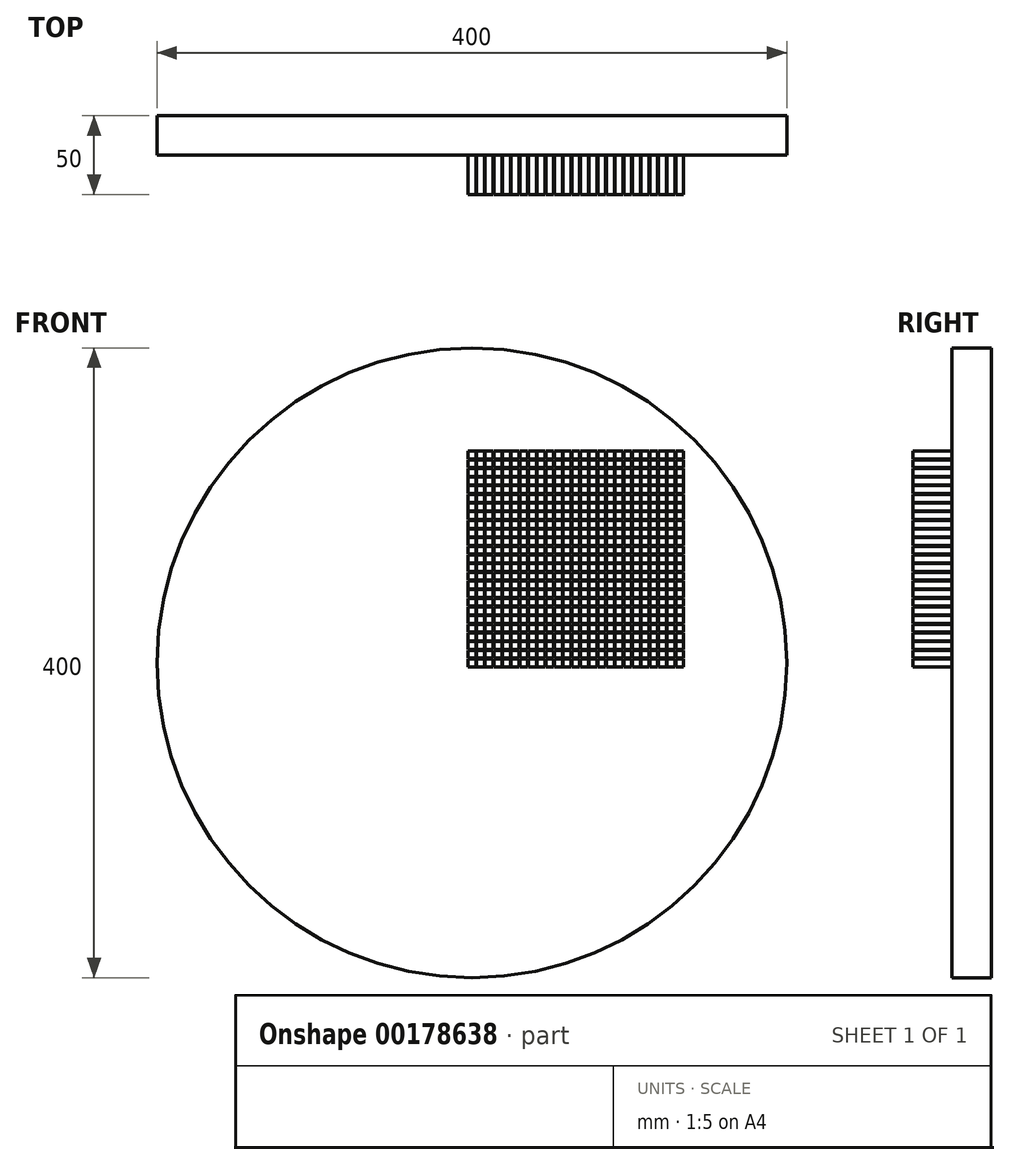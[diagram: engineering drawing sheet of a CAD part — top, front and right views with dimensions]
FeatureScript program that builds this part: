
annotation { "Feature Type Name" : "Feature", "Feature Type Description" : "" }
export const myFeature = defineFeature(function(context is Context, id is Id, definition is map)
    precondition{}
    {
        {
            var Q0;
            Q0=qCreatedBy(makeId("Front.planeOp"),FACE);
            var sketch = newSketch(context, id + "F0", { "sketchPlane" : qUnion([Q0])});
            skCircle(sketch, "E0", {"center": v(0, 0) * mm, "radius": 200 * mm});
            skLineSegment(sketch, "E1.bottom", {"start": v(141.42, 141.42) * mm, "end": v(-141.42, 141.42) * mm});
            skLineSegment(sketch, "E1.top", {"start": v(141.42, -141.42) * mm, "end": v(-141.42, -141.42) * mm});
            skLineSegment(sketch, "E1.left", {"start": v(141.42, 141.42) * mm, "end": v(141.42, -141.42) * mm});
            skLineSegment(sketch, "E1.right", {"start": v(-141.42, 141.42) * mm, "end": v(-141.42, -141.42) * mm});
            skSolve(sketch);
        }
        {
            var Q0;
            {var subQ0=sQuery(id+"F0.wireOp",EDGE,"E1.bottom");Q0=makeQuery(id+"F0.imprint","IMPRINT",FACE,{"disambiguationData":[TD([[makeQuery(id+"F0.imprint","IMPRINT",EDGE,{"derivedFrom":subQ0}),-1.0]])]});}
            var Q1;
            {var subQ0=sQuery(id+"F0.wireOp",EDGE,"E1.right");Q1=makeQuery(id+"F0.imprint","IMPRINT",FACE,{"disambiguationData":[TD([[makeQuery(id+"F0.imprint","IMPRINT",EDGE,{"derivedFrom":subQ0}),-1.0]])]});}
            var Q2;
            {var subQ0=sQuery(id+"F0.wireOp",EDGE,"E1.left");Q2=makeQuery(id+"F0.imprint","IMPRINT",FACE,{"disambiguationData":[TD([[makeQuery(id+"F0.imprint","IMPRINT",EDGE,{"derivedFrom":subQ0}),1.0]])]});}
            var Q3;
            {var subQ0=sQuery(id+"F0.wireOp",EDGE,"E1.top");Q3=makeQuery(id+"F0.imprint","IMPRINT",FACE,{"disambiguationData":[TD([[makeQuery(id+"F0.imprint","IMPRINT",EDGE,{"derivedFrom":subQ0}),1.0]])]});}
            var Q4;
            Q4=makeQuery(id+"F0.imprint","IMPRINT",FACE,{"disambiguationData":[TD([[makeQuery(id+"F0.imprint","IMPRINT",EDGE,{"derivedFrom":sQuery(id+"F0.wireOp",EDGE,"E1.bottom")}),1.0]])]});
            extrude(context, id + "F1", {"entities" : qUnion([Q0, Q1, Q2, Q3, Q4]), "depth" : 25 * mm});
        }
        {
            var Q0;
            Q0=makeQuery(id+"F1.opExtrude","CAP_FACE",FACE,{"disambiguationData":[OSD([sQuery(id+"F0.wireOp",EDGE,"E0")])],"isStart":false});
            var sketch = newSketch(context, id + "F2", { "sketchPlane" : qUnion([Q0])});
            skLineSegment(sketch, "E2.bottom", {"start": v(2.5, 2.5) * mm, "end": v(-2.5, 2.5) * mm});
            skLineSegment(sketch, "E2.top", {"start": v(2.5, -2.5) * mm, "end": v(-2.5, -2.5) * mm});
            skLineSegment(sketch, "E2.left", {"start": v(2.5, 2.5) * mm, "end": v(2.5, -2.5) * mm});
            skLineSegment(sketch, "E2.right", {"start": v(-2.5, 2.5) * mm, "end": v(-2.5, -2.5) * mm});
            skPoint(sketch, "E2.middle", {"position": v(0, 0) * mm});
            skLineSegment(sketch, "E3.0.1.0", {"start": v(2.5, 8) * mm, "end": v(-2.5, 8) * mm});
            skLineSegment(sketch, "E3.0.1.1", {"start": v(2.5, 8) * mm, "end": v(2.5, 3) * mm});
            skLineSegment(sketch, "E3.0.1.2", {"start": v(2.5, 3) * mm, "end": v(-2.5, 3) * mm});
            skLineSegment(sketch, "E3.0.1.3", {"start": v(-2.5, 8) * mm, "end": v(-2.5, 3) * mm});
            skPoint(sketch, "E3.0.1.4", {"position": v(0, 5.5) * mm});
            skLineSegment(sketch, "E3.0.2.0", {"start": v(2.5, 13.5) * mm, "end": v(-2.5, 13.5) * mm});
            skLineSegment(sketch, "E3.0.2.1", {"start": v(2.5, 13.5) * mm, "end": v(2.5, 8.5) * mm});
            skLineSegment(sketch, "E3.0.2.2", {"start": v(2.5, 8.5) * mm, "end": v(-2.5, 8.5) * mm});
            skLineSegment(sketch, "E3.0.2.3", {"start": v(-2.5, 13.5) * mm, "end": v(-2.5, 8.5) * mm});
            skPoint(sketch, "E3.0.2.4", {"position": v(0, 11) * mm});
            skLineSegment(sketch, "E3.0.3.0", {"start": v(2.5, 19) * mm, "end": v(-2.5, 19) * mm});
            skLineSegment(sketch, "E3.0.3.1", {"start": v(2.5, 19) * mm, "end": v(2.5, 14) * mm});
            skLineSegment(sketch, "E3.0.3.2", {"start": v(2.5, 14) * mm, "end": v(-2.5, 14) * mm});
            skLineSegment(sketch, "E3.0.3.3", {"start": v(-2.5, 19) * mm, "end": v(-2.5, 14) * mm});
            skPoint(sketch, "E3.0.3.4", {"position": v(0, 16.5) * mm});
            skLineSegment(sketch, "E3.0.4.0", {"start": v(2.5, 24.5) * mm, "end": v(-2.5, 24.5) * mm});
            skLineSegment(sketch, "E3.0.4.1", {"start": v(2.5, 24.5) * mm, "end": v(2.5, 19.5) * mm});
            skLineSegment(sketch, "E3.0.4.2", {"start": v(2.5, 19.5) * mm, "end": v(-2.5, 19.5) * mm});
            skLineSegment(sketch, "E3.0.4.3", {"start": v(-2.5, 24.5) * mm, "end": v(-2.5, 19.5) * mm});
            skPoint(sketch, "E3.0.4.4", {"position": v(0, 22) * mm});
            skLineSegment(sketch, "E3.0.5.0", {"start": v(2.5, 30) * mm, "end": v(-2.5, 30) * mm});
            skLineSegment(sketch, "E3.0.5.1", {"start": v(2.5, 30) * mm, "end": v(2.5, 25) * mm});
            skLineSegment(sketch, "E3.0.5.2", {"start": v(2.5, 25) * mm, "end": v(-2.5, 25) * mm});
            skLineSegment(sketch, "E3.0.5.3", {"start": v(-2.5, 30) * mm, "end": v(-2.5, 25) * mm});
            skPoint(sketch, "E3.0.5.4", {"position": v(0, 27.5) * mm});
            skLineSegment(sketch, "E3.0.6.0", {"start": v(2.5, 35.5) * mm, "end": v(-2.5, 35.5) * mm});
            skLineSegment(sketch, "E3.0.6.1", {"start": v(2.5, 35.5) * mm, "end": v(2.5, 30.5) * mm});
            skLineSegment(sketch, "E3.0.6.2", {"start": v(2.5, 30.5) * mm, "end": v(-2.5, 30.5) * mm});
            skLineSegment(sketch, "E3.0.6.3", {"start": v(-2.5, 35.5) * mm, "end": v(-2.5, 30.5) * mm});
            skPoint(sketch, "E3.0.6.4", {"position": v(0, 33) * mm});
            skLineSegment(sketch, "E3.0.7.0", {"start": v(2.5, 41) * mm, "end": v(-2.5, 41) * mm});
            skLineSegment(sketch, "E3.0.7.1", {"start": v(2.5, 41) * mm, "end": v(2.5, 36) * mm});
            skLineSegment(sketch, "E3.0.7.2", {"start": v(2.5, 36) * mm, "end": v(-2.5, 36) * mm});
            skLineSegment(sketch, "E3.0.7.3", {"start": v(-2.5, 41) * mm, "end": v(-2.5, 36) * mm});
            skPoint(sketch, "E3.0.7.4", {"position": v(0, 38.5) * mm});
            skLineSegment(sketch, "E3.0.8.0", {"start": v(2.5, 46.5) * mm, "end": v(-2.5, 46.5) * mm});
            skLineSegment(sketch, "E3.0.8.1", {"start": v(2.5, 46.5) * mm, "end": v(2.5, 41.5) * mm});
            skLineSegment(sketch, "E3.0.8.2", {"start": v(2.5, 41.5) * mm, "end": v(-2.5, 41.5) * mm});
            skLineSegment(sketch, "E3.0.8.3", {"start": v(-2.5, 46.5) * mm, "end": v(-2.5, 41.5) * mm});
            skPoint(sketch, "E3.0.8.4", {"position": v(0, 44) * mm});
            skLineSegment(sketch, "E3.0.9.0", {"start": v(2.5, 52) * mm, "end": v(-2.5, 52) * mm});
            skLineSegment(sketch, "E3.0.9.1", {"start": v(2.5, 52) * mm, "end": v(2.5, 47) * mm});
            skLineSegment(sketch, "E3.0.9.2", {"start": v(2.5, 47) * mm, "end": v(-2.5, 47) * mm});
            skLineSegment(sketch, "E3.0.9.3", {"start": v(-2.5, 52) * mm, "end": v(-2.5, 47) * mm});
            skPoint(sketch, "E3.0.9.4", {"position": v(0, 49.5) * mm});
            skLineSegment(sketch, "E3.0.10.0", {"start": v(2.5, 57.5) * mm, "end": v(-2.5, 57.5) * mm});
            skLineSegment(sketch, "E3.0.10.1", {"start": v(2.5, 57.5) * mm, "end": v(2.5, 52.5) * mm});
            skLineSegment(sketch, "E3.0.10.2", {"start": v(2.5, 52.5) * mm, "end": v(-2.5, 52.5) * mm});
            skLineSegment(sketch, "E3.0.10.3", {"start": v(-2.5, 57.5) * mm, "end": v(-2.5, 52.5) * mm});
            skPoint(sketch, "E3.0.10.4", {"position": v(0, 55) * mm});
            skLineSegment(sketch, "E3.0.11.0", {"start": v(2.5, 63) * mm, "end": v(-2.5, 63) * mm});
            skLineSegment(sketch, "E3.0.11.1", {"start": v(2.5, 63) * mm, "end": v(2.5, 58) * mm});
            skLineSegment(sketch, "E3.0.11.2", {"start": v(2.5, 58) * mm, "end": v(-2.5, 58) * mm});
            skLineSegment(sketch, "E3.0.11.3", {"start": v(-2.5, 63) * mm, "end": v(-2.5, 58) * mm});
            skPoint(sketch, "E3.0.11.4", {"position": v(0, 60.5) * mm});
            skLineSegment(sketch, "E3.0.12.0", {"start": v(2.5, 68.5) * mm, "end": v(-2.5, 68.5) * mm});
            skLineSegment(sketch, "E3.0.12.1", {"start": v(2.5, 68.5) * mm, "end": v(2.5, 63.5) * mm});
            skLineSegment(sketch, "E3.0.12.2", {"start": v(2.5, 63.5) * mm, "end": v(-2.5, 63.5) * mm});
            skLineSegment(sketch, "E3.0.12.3", {"start": v(-2.5, 68.5) * mm, "end": v(-2.5, 63.5) * mm});
            skPoint(sketch, "E3.0.12.4", {"position": v(0, 66) * mm});
            skLineSegment(sketch, "E3.0.13.0", {"start": v(2.5, 74) * mm, "end": v(-2.5, 74) * mm});
            skLineSegment(sketch, "E3.0.13.1", {"start": v(2.5, 74) * mm, "end": v(2.5, 69) * mm});
            skLineSegment(sketch, "E3.0.13.2", {"start": v(2.5, 69) * mm, "end": v(-2.5, 69) * mm});
            skLineSegment(sketch, "E3.0.13.3", {"start": v(-2.5, 74) * mm, "end": v(-2.5, 69) * mm});
            skPoint(sketch, "E3.0.13.4", {"position": v(0, 71.5) * mm});
            skLineSegment(sketch, "E3.0.14.0", {"start": v(2.5, 79.5) * mm, "end": v(-2.5, 79.5) * mm});
            skLineSegment(sketch, "E3.0.14.1", {"start": v(2.5, 79.5) * mm, "end": v(2.5, 74.5) * mm});
            skLineSegment(sketch, "E3.0.14.2", {"start": v(2.5, 74.5) * mm, "end": v(-2.5, 74.5) * mm});
            skLineSegment(sketch, "E3.0.14.3", {"start": v(-2.5, 79.5) * mm, "end": v(-2.5, 74.5) * mm});
            skPoint(sketch, "E3.0.14.4", {"position": v(0, 77) * mm});
            skLineSegment(sketch, "E3.0.15.0", {"start": v(2.5, 85) * mm, "end": v(-2.5, 85) * mm});
            skLineSegment(sketch, "E3.0.15.1", {"start": v(2.5, 85) * mm, "end": v(2.5, 80) * mm});
            skLineSegment(sketch, "E3.0.15.2", {"start": v(2.5, 80) * mm, "end": v(-2.5, 80) * mm});
            skLineSegment(sketch, "E3.0.15.3", {"start": v(-2.5, 85) * mm, "end": v(-2.5, 80) * mm});
            skPoint(sketch, "E3.0.15.4", {"position": v(0, 82.5) * mm});
            skLineSegment(sketch, "E3.0.16.0", {"start": v(2.5, 90.5) * mm, "end": v(-2.5, 90.5) * mm});
            skLineSegment(sketch, "E3.0.16.1", {"start": v(2.5, 90.5) * mm, "end": v(2.5, 85.5) * mm});
            skLineSegment(sketch, "E3.0.16.2", {"start": v(2.5, 85.5) * mm, "end": v(-2.5, 85.5) * mm});
            skLineSegment(sketch, "E3.0.16.3", {"start": v(-2.5, 90.5) * mm, "end": v(-2.5, 85.5) * mm});
            skPoint(sketch, "E3.0.16.4", {"position": v(0, 88) * mm});
            skLineSegment(sketch, "E3.0.17.0", {"start": v(2.5, 96) * mm, "end": v(-2.5, 96) * mm});
            skLineSegment(sketch, "E3.0.17.1", {"start": v(2.5, 96) * mm, "end": v(2.5, 91) * mm});
            skLineSegment(sketch, "E3.0.17.2", {"start": v(2.5, 91) * mm, "end": v(-2.5, 91) * mm});
            skLineSegment(sketch, "E3.0.17.3", {"start": v(-2.5, 96) * mm, "end": v(-2.5, 91) * mm});
            skPoint(sketch, "E3.0.17.4", {"position": v(0, 93.5) * mm});
            skLineSegment(sketch, "E3.0.18.0", {"start": v(2.5, 101.5) * mm, "end": v(-2.5, 101.5) * mm});
            skLineSegment(sketch, "E3.0.18.1", {"start": v(2.5, 101.5) * mm, "end": v(2.5, 96.5) * mm});
            skLineSegment(sketch, "E3.0.18.2", {"start": v(2.5, 96.5) * mm, "end": v(-2.5, 96.5) * mm});
            skLineSegment(sketch, "E3.0.18.3", {"start": v(-2.5, 101.5) * mm, "end": v(-2.5, 96.5) * mm});
            skPoint(sketch, "E3.0.18.4", {"position": v(0, 99) * mm});
            skLineSegment(sketch, "E3.0.19.0", {"start": v(2.5, 107) * mm, "end": v(-2.5, 107) * mm});
            skLineSegment(sketch, "E3.0.19.1", {"start": v(2.5, 107) * mm, "end": v(2.5, 102) * mm});
            skLineSegment(sketch, "E3.0.19.2", {"start": v(2.5, 102) * mm, "end": v(-2.5, 102) * mm});
            skLineSegment(sketch, "E3.0.19.3", {"start": v(-2.5, 107) * mm, "end": v(-2.5, 102) * mm});
            skPoint(sketch, "E3.0.19.4", {"position": v(0, 104.5) * mm});
            skLineSegment(sketch, "E3.0.20.0", {"start": v(2.5, 112.5) * mm, "end": v(-2.5, 112.5) * mm});
            skLineSegment(sketch, "E3.0.20.1", {"start": v(2.5, 112.5) * mm, "end": v(2.5, 107.5) * mm});
            skLineSegment(sketch, "E3.0.20.2", {"start": v(2.5, 107.5) * mm, "end": v(-2.5, 107.5) * mm});
            skLineSegment(sketch, "E3.0.20.3", {"start": v(-2.5, 112.5) * mm, "end": v(-2.5, 107.5) * mm});
            skPoint(sketch, "E3.0.20.4", {"position": v(0, 110) * mm});
            skLineSegment(sketch, "E3.0.21.0", {"start": v(2.5, 118) * mm, "end": v(-2.5, 118) * mm});
            skLineSegment(sketch, "E3.0.21.1", {"start": v(2.5, 118) * mm, "end": v(2.5, 113) * mm});
            skLineSegment(sketch, "E3.0.21.2", {"start": v(2.5, 113) * mm, "end": v(-2.5, 113) * mm});
            skLineSegment(sketch, "E3.0.21.3", {"start": v(-2.5, 118) * mm, "end": v(-2.5, 113) * mm});
            skPoint(sketch, "E3.0.21.4", {"position": v(0, 115.5) * mm});
            skLineSegment(sketch, "E3.0.22.0", {"start": v(2.5, 123.5) * mm, "end": v(-2.5, 123.5) * mm});
            skLineSegment(sketch, "E3.0.22.1", {"start": v(2.5, 123.5) * mm, "end": v(2.5, 118.5) * mm});
            skLineSegment(sketch, "E3.0.22.2", {"start": v(2.5, 118.5) * mm, "end": v(-2.5, 118.5) * mm});
            skLineSegment(sketch, "E3.0.22.3", {"start": v(-2.5, 123.5) * mm, "end": v(-2.5, 118.5) * mm});
            skPoint(sketch, "E3.0.22.4", {"position": v(0, 121) * mm});
            skLineSegment(sketch, "E3.0.23.0", {"start": v(2.5, 129) * mm, "end": v(-2.5, 129) * mm});
            skLineSegment(sketch, "E3.0.23.1", {"start": v(2.5, 129) * mm, "end": v(2.5, 124) * mm});
            skLineSegment(sketch, "E3.0.23.2", {"start": v(2.5, 124) * mm, "end": v(-2.5, 124) * mm});
            skLineSegment(sketch, "E3.0.23.3", {"start": v(-2.5, 129) * mm, "end": v(-2.5, 124) * mm});
            skPoint(sketch, "E3.0.23.4", {"position": v(0, 126.5) * mm});
            skLineSegment(sketch, "E3.0.24.0", {"start": v(2.5, 134.5) * mm, "end": v(-2.5, 134.5) * mm});
            skLineSegment(sketch, "E3.0.24.1", {"start": v(2.5, 134.5) * mm, "end": v(2.5, 129.5) * mm});
            skLineSegment(sketch, "E3.0.24.2", {"start": v(2.5, 129.5) * mm, "end": v(-2.5, 129.5) * mm});
            skLineSegment(sketch, "E3.0.24.3", {"start": v(-2.5, 134.5) * mm, "end": v(-2.5, 129.5) * mm});
            skPoint(sketch, "E3.0.24.4", {"position": v(0, 132) * mm});
            skLineSegment(sketch, "E3.1.0.0", {"start": v(8, 2.5) * mm, "end": v(3, 2.5) * mm});
            skLineSegment(sketch, "E3.1.0.1", {"start": v(8, 2.5) * mm, "end": v(8, -2.5) * mm});
            skLineSegment(sketch, "E3.1.0.2", {"start": v(8, -2.5) * mm, "end": v(3, -2.5) * mm});
            skLineSegment(sketch, "E3.1.0.3", {"start": v(3, 2.5) * mm, "end": v(3, -2.5) * mm});
            skPoint(sketch, "E3.1.0.4", {"position": v(5.5, 0) * mm});
            skLineSegment(sketch, "E3.1.1.0", {"start": v(8, 8) * mm, "end": v(3, 8) * mm});
            skLineSegment(sketch, "E3.1.1.1", {"start": v(8, 8) * mm, "end": v(8, 3) * mm});
            skLineSegment(sketch, "E3.1.1.2", {"start": v(8, 3) * mm, "end": v(3, 3) * mm});
            skLineSegment(sketch, "E3.1.1.3", {"start": v(3, 8) * mm, "end": v(3, 3) * mm});
            skPoint(sketch, "E3.1.1.4", {"position": v(5.5, 5.5) * mm});
            skLineSegment(sketch, "E3.1.2.0", {"start": v(8, 13.5) * mm, "end": v(3, 13.5) * mm});
            skLineSegment(sketch, "E3.1.2.1", {"start": v(8, 13.5) * mm, "end": v(8, 8.5) * mm});
            skLineSegment(sketch, "E3.1.2.2", {"start": v(8, 8.5) * mm, "end": v(3, 8.5) * mm});
            skLineSegment(sketch, "E3.1.2.3", {"start": v(3, 13.5) * mm, "end": v(3, 8.5) * mm});
            skPoint(sketch, "E3.1.2.4", {"position": v(5.5, 11) * mm});
            skLineSegment(sketch, "E3.1.3.0", {"start": v(8, 19) * mm, "end": v(3, 19) * mm});
            skLineSegment(sketch, "E3.1.3.1", {"start": v(8, 19) * mm, "end": v(8, 14) * mm});
            skLineSegment(sketch, "E3.1.3.2", {"start": v(8, 14) * mm, "end": v(3, 14) * mm});
            skLineSegment(sketch, "E3.1.3.3", {"start": v(3, 19) * mm, "end": v(3, 14) * mm});
            skPoint(sketch, "E3.1.3.4", {"position": v(5.5, 16.5) * mm});
            skLineSegment(sketch, "E3.1.4.0", {"start": v(8, 24.5) * mm, "end": v(3, 24.5) * mm});
            skLineSegment(sketch, "E3.1.4.1", {"start": v(8, 24.5) * mm, "end": v(8, 19.5) * mm});
            skLineSegment(sketch, "E3.1.4.2", {"start": v(8, 19.5) * mm, "end": v(3, 19.5) * mm});
            skLineSegment(sketch, "E3.1.4.3", {"start": v(3, 24.5) * mm, "end": v(3, 19.5) * mm});
            skPoint(sketch, "E3.1.4.4", {"position": v(5.5, 22) * mm});
            skLineSegment(sketch, "E3.1.5.0", {"start": v(8, 30) * mm, "end": v(3, 30) * mm});
            skLineSegment(sketch, "E3.1.5.1", {"start": v(8, 30) * mm, "end": v(8, 25) * mm});
            skLineSegment(sketch, "E3.1.5.2", {"start": v(8, 25) * mm, "end": v(3, 25) * mm});
            skLineSegment(sketch, "E3.1.5.3", {"start": v(3, 30) * mm, "end": v(3, 25) * mm});
            skPoint(sketch, "E3.1.5.4", {"position": v(5.5, 27.5) * mm});
            skLineSegment(sketch, "E3.1.6.0", {"start": v(8, 35.5) * mm, "end": v(3, 35.5) * mm});
            skLineSegment(sketch, "E3.1.6.1", {"start": v(8, 35.5) * mm, "end": v(8, 30.5) * mm});
            skLineSegment(sketch, "E3.1.6.2", {"start": v(8, 30.5) * mm, "end": v(3, 30.5) * mm});
            skLineSegment(sketch, "E3.1.6.3", {"start": v(3, 35.5) * mm, "end": v(3, 30.5) * mm});
            skPoint(sketch, "E3.1.6.4", {"position": v(5.5, 33) * mm});
            skLineSegment(sketch, "E3.1.7.0", {"start": v(8, 41) * mm, "end": v(3, 41) * mm});
            skLineSegment(sketch, "E3.1.7.1", {"start": v(8, 41) * mm, "end": v(8, 36) * mm});
            skLineSegment(sketch, "E3.1.7.2", {"start": v(8, 36) * mm, "end": v(3, 36) * mm});
            skLineSegment(sketch, "E3.1.7.3", {"start": v(3, 41) * mm, "end": v(3, 36) * mm});
            skPoint(sketch, "E3.1.7.4", {"position": v(5.5, 38.5) * mm});
            skLineSegment(sketch, "E3.1.8.0", {"start": v(8, 46.5) * mm, "end": v(3, 46.5) * mm});
            skLineSegment(sketch, "E3.1.8.1", {"start": v(8, 46.5) * mm, "end": v(8, 41.5) * mm});
            skLineSegment(sketch, "E3.1.8.2", {"start": v(8, 41.5) * mm, "end": v(3, 41.5) * mm});
            skLineSegment(sketch, "E3.1.8.3", {"start": v(3, 46.5) * mm, "end": v(3, 41.5) * mm});
            skPoint(sketch, "E3.1.8.4", {"position": v(5.5, 44) * mm});
            skLineSegment(sketch, "E3.1.9.0", {"start": v(8, 52) * mm, "end": v(3, 52) * mm});
            skLineSegment(sketch, "E3.1.9.1", {"start": v(8, 52) * mm, "end": v(8, 47) * mm});
            skLineSegment(sketch, "E3.1.9.2", {"start": v(8, 47) * mm, "end": v(3, 47) * mm});
            skLineSegment(sketch, "E3.1.9.3", {"start": v(3, 52) * mm, "end": v(3, 47) * mm});
            skPoint(sketch, "E3.1.9.4", {"position": v(5.5, 49.5) * mm});
            skLineSegment(sketch, "E3.1.10.0", {"start": v(8, 57.5) * mm, "end": v(3, 57.5) * mm});
            skLineSegment(sketch, "E3.1.10.1", {"start": v(8, 57.5) * mm, "end": v(8, 52.5) * mm});
            skLineSegment(sketch, "E3.1.10.2", {"start": v(8, 52.5) * mm, "end": v(3, 52.5) * mm});
            skLineSegment(sketch, "E3.1.10.3", {"start": v(3, 57.5) * mm, "end": v(3, 52.5) * mm});
            skPoint(sketch, "E3.1.10.4", {"position": v(5.5, 55) * mm});
            skLineSegment(sketch, "E3.1.11.0", {"start": v(8, 63) * mm, "end": v(3, 63) * mm});
            skLineSegment(sketch, "E3.1.11.1", {"start": v(8, 63) * mm, "end": v(8, 58) * mm});
            skLineSegment(sketch, "E3.1.11.2", {"start": v(8, 58) * mm, "end": v(3, 58) * mm});
            skLineSegment(sketch, "E3.1.11.3", {"start": v(3, 63) * mm, "end": v(3, 58) * mm});
            skPoint(sketch, "E3.1.11.4", {"position": v(5.5, 60.5) * mm});
            skLineSegment(sketch, "E3.1.12.0", {"start": v(8, 68.5) * mm, "end": v(3, 68.5) * mm});
            skLineSegment(sketch, "E3.1.12.1", {"start": v(8, 68.5) * mm, "end": v(8, 63.5) * mm});
            skLineSegment(sketch, "E3.1.12.2", {"start": v(8, 63.5) * mm, "end": v(3, 63.5) * mm});
            skLineSegment(sketch, "E3.1.12.3", {"start": v(3, 68.5) * mm, "end": v(3, 63.5) * mm});
            skPoint(sketch, "E3.1.12.4", {"position": v(5.5, 66) * mm});
            skLineSegment(sketch, "E3.1.13.0", {"start": v(8, 74) * mm, "end": v(3, 74) * mm});
            skLineSegment(sketch, "E3.1.13.1", {"start": v(8, 74) * mm, "end": v(8, 69) * mm});
            skLineSegment(sketch, "E3.1.13.2", {"start": v(8, 69) * mm, "end": v(3, 69) * mm});
            skLineSegment(sketch, "E3.1.13.3", {"start": v(3, 74) * mm, "end": v(3, 69) * mm});
            skPoint(sketch, "E3.1.13.4", {"position": v(5.5, 71.5) * mm});
            skLineSegment(sketch, "E3.1.14.0", {"start": v(8, 79.5) * mm, "end": v(3, 79.5) * mm});
            skLineSegment(sketch, "E3.1.14.1", {"start": v(8, 79.5) * mm, "end": v(8, 74.5) * mm});
            skLineSegment(sketch, "E3.1.14.2", {"start": v(8, 74.5) * mm, "end": v(3, 74.5) * mm});
            skLineSegment(sketch, "E3.1.14.3", {"start": v(3, 79.5) * mm, "end": v(3, 74.5) * mm});
            skPoint(sketch, "E3.1.14.4", {"position": v(5.5, 77) * mm});
            skLineSegment(sketch, "E3.1.15.0", {"start": v(8, 85) * mm, "end": v(3, 85) * mm});
            skLineSegment(sketch, "E3.1.15.1", {"start": v(8, 85) * mm, "end": v(8, 80) * mm});
            skLineSegment(sketch, "E3.1.15.2", {"start": v(8, 80) * mm, "end": v(3, 80) * mm});
            skLineSegment(sketch, "E3.1.15.3", {"start": v(3, 85) * mm, "end": v(3, 80) * mm});
            skPoint(sketch, "E3.1.15.4", {"position": v(5.5, 82.5) * mm});
            skLineSegment(sketch, "E3.1.16.0", {"start": v(8, 90.5) * mm, "end": v(3, 90.5) * mm});
            skLineSegment(sketch, "E3.1.16.1", {"start": v(8, 90.5) * mm, "end": v(8, 85.5) * mm});
            skLineSegment(sketch, "E3.1.16.2", {"start": v(8, 85.5) * mm, "end": v(3, 85.5) * mm});
            skLineSegment(sketch, "E3.1.16.3", {"start": v(3, 90.5) * mm, "end": v(3, 85.5) * mm});
            skPoint(sketch, "E3.1.16.4", {"position": v(5.5, 88) * mm});
            skLineSegment(sketch, "E3.1.17.0", {"start": v(8, 96) * mm, "end": v(3, 96) * mm});
            skLineSegment(sketch, "E3.1.17.1", {"start": v(8, 96) * mm, "end": v(8, 91) * mm});
            skLineSegment(sketch, "E3.1.17.2", {"start": v(8, 91) * mm, "end": v(3, 91) * mm});
            skLineSegment(sketch, "E3.1.17.3", {"start": v(3, 96) * mm, "end": v(3, 91) * mm});
            skPoint(sketch, "E3.1.17.4", {"position": v(5.5, 93.5) * mm});
            skLineSegment(sketch, "E3.1.18.0", {"start": v(8, 101.5) * mm, "end": v(3, 101.5) * mm});
            skLineSegment(sketch, "E3.1.18.1", {"start": v(8, 101.5) * mm, "end": v(8, 96.5) * mm});
            skLineSegment(sketch, "E3.1.18.2", {"start": v(8, 96.5) * mm, "end": v(3, 96.5) * mm});
            skLineSegment(sketch, "E3.1.18.3", {"start": v(3, 101.5) * mm, "end": v(3, 96.5) * mm});
            skPoint(sketch, "E3.1.18.4", {"position": v(5.5, 99) * mm});
            skLineSegment(sketch, "E3.1.19.0", {"start": v(8, 107) * mm, "end": v(3, 107) * mm});
            skLineSegment(sketch, "E3.1.19.1", {"start": v(8, 107) * mm, "end": v(8, 102) * mm});
            skLineSegment(sketch, "E3.1.19.2", {"start": v(8, 102) * mm, "end": v(3, 102) * mm});
            skLineSegment(sketch, "E3.1.19.3", {"start": v(3, 107) * mm, "end": v(3, 102) * mm});
            skPoint(sketch, "E3.1.19.4", {"position": v(5.5, 104.5) * mm});
            skLineSegment(sketch, "E3.1.20.0", {"start": v(8, 112.5) * mm, "end": v(3, 112.5) * mm});
            skLineSegment(sketch, "E3.1.20.1", {"start": v(8, 112.5) * mm, "end": v(8, 107.5) * mm});
            skLineSegment(sketch, "E3.1.20.2", {"start": v(8, 107.5) * mm, "end": v(3, 107.5) * mm});
            skLineSegment(sketch, "E3.1.20.3", {"start": v(3, 112.5) * mm, "end": v(3, 107.5) * mm});
            skPoint(sketch, "E3.1.20.4", {"position": v(5.5, 110) * mm});
            skLineSegment(sketch, "E3.1.21.0", {"start": v(8, 118) * mm, "end": v(3, 118) * mm});
            skLineSegment(sketch, "E3.1.21.1", {"start": v(8, 118) * mm, "end": v(8, 113) * mm});
            skLineSegment(sketch, "E3.1.21.2", {"start": v(8, 113) * mm, "end": v(3, 113) * mm});
            skLineSegment(sketch, "E3.1.21.3", {"start": v(3, 118) * mm, "end": v(3, 113) * mm});
            skPoint(sketch, "E3.1.21.4", {"position": v(5.5, 115.5) * mm});
            skLineSegment(sketch, "E3.1.22.0", {"start": v(8, 123.5) * mm, "end": v(3, 123.5) * mm});
            skLineSegment(sketch, "E3.1.22.1", {"start": v(8, 123.5) * mm, "end": v(8, 118.5) * mm});
            skLineSegment(sketch, "E3.1.22.2", {"start": v(8, 118.5) * mm, "end": v(3, 118.5) * mm});
            skLineSegment(sketch, "E3.1.22.3", {"start": v(3, 123.5) * mm, "end": v(3, 118.5) * mm});
            skPoint(sketch, "E3.1.22.4", {"position": v(5.5, 121) * mm});
            skLineSegment(sketch, "E3.1.23.0", {"start": v(8, 129) * mm, "end": v(3, 129) * mm});
            skLineSegment(sketch, "E3.1.23.1", {"start": v(8, 129) * mm, "end": v(8, 124) * mm});
            skLineSegment(sketch, "E3.1.23.2", {"start": v(8, 124) * mm, "end": v(3, 124) * mm});
            skLineSegment(sketch, "E3.1.23.3", {"start": v(3, 129) * mm, "end": v(3, 124) * mm});
            skPoint(sketch, "E3.1.23.4", {"position": v(5.5, 126.5) * mm});
            skLineSegment(sketch, "E3.1.24.0", {"start": v(8, 134.5) * mm, "end": v(3, 134.5) * mm});
            skLineSegment(sketch, "E3.1.24.1", {"start": v(8, 134.5) * mm, "end": v(8, 129.5) * mm});
            skLineSegment(sketch, "E3.1.24.2", {"start": v(8, 129.5) * mm, "end": v(3, 129.5) * mm});
            skLineSegment(sketch, "E3.1.24.3", {"start": v(3, 134.5) * mm, "end": v(3, 129.5) * mm});
            skPoint(sketch, "E3.1.24.4", {"position": v(5.5, 132) * mm});
            skLineSegment(sketch, "E3.2.0.0", {"start": v(13.5, 2.5) * mm, "end": v(8.5, 2.5) * mm});
            skLineSegment(sketch, "E3.2.0.1", {"start": v(13.5, 2.5) * mm, "end": v(13.5, -2.5) * mm});
            skLineSegment(sketch, "E3.2.0.2", {"start": v(13.5, -2.5) * mm, "end": v(8.5, -2.5) * mm});
            skLineSegment(sketch, "E3.2.0.3", {"start": v(8.5, 2.5) * mm, "end": v(8.5, -2.5) * mm});
            skPoint(sketch, "E3.2.0.4", {"position": v(11, 0) * mm});
            skLineSegment(sketch, "E3.2.1.0", {"start": v(13.5, 8) * mm, "end": v(8.5, 8) * mm});
            skLineSegment(sketch, "E3.2.1.1", {"start": v(13.5, 8) * mm, "end": v(13.5, 3) * mm});
            skLineSegment(sketch, "E3.2.1.2", {"start": v(13.5, 3) * mm, "end": v(8.5, 3) * mm});
            skLineSegment(sketch, "E3.2.1.3", {"start": v(8.5, 8) * mm, "end": v(8.5, 3) * mm});
            skPoint(sketch, "E3.2.1.4", {"position": v(11, 5.5) * mm});
            skLineSegment(sketch, "E3.2.2.0", {"start": v(13.5, 13.5) * mm, "end": v(8.5, 13.5) * mm});
            skLineSegment(sketch, "E3.2.2.1", {"start": v(13.5, 13.5) * mm, "end": v(13.5, 8.5) * mm});
            skLineSegment(sketch, "E3.2.2.2", {"start": v(13.5, 8.5) * mm, "end": v(8.5, 8.5) * mm});
            skLineSegment(sketch, "E3.2.2.3", {"start": v(8.5, 13.5) * mm, "end": v(8.5, 8.5) * mm});
            skPoint(sketch, "E3.2.2.4", {"position": v(11, 11) * mm});
            skLineSegment(sketch, "E3.2.3.0", {"start": v(13.5, 19) * mm, "end": v(8.5, 19) * mm});
            skLineSegment(sketch, "E3.2.3.1", {"start": v(13.5, 19) * mm, "end": v(13.5, 14) * mm});
            skLineSegment(sketch, "E3.2.3.2", {"start": v(13.5, 14) * mm, "end": v(8.5, 14) * mm});
            skLineSegment(sketch, "E3.2.3.3", {"start": v(8.5, 19) * mm, "end": v(8.5, 14) * mm});
            skPoint(sketch, "E3.2.3.4", {"position": v(11, 16.5) * mm});
            skLineSegment(sketch, "E3.2.4.0", {"start": v(13.5, 24.5) * mm, "end": v(8.5, 24.5) * mm});
            skLineSegment(sketch, "E3.2.4.1", {"start": v(13.5, 24.5) * mm, "end": v(13.5, 19.5) * mm});
            skLineSegment(sketch, "E3.2.4.2", {"start": v(13.5, 19.5) * mm, "end": v(8.5, 19.5) * mm});
            skLineSegment(sketch, "E3.2.4.3", {"start": v(8.5, 24.5) * mm, "end": v(8.5, 19.5) * mm});
            skPoint(sketch, "E3.2.4.4", {"position": v(11, 22) * mm});
            skLineSegment(sketch, "E3.2.5.0", {"start": v(13.5, 30) * mm, "end": v(8.5, 30) * mm});
            skLineSegment(sketch, "E3.2.5.1", {"start": v(13.5, 30) * mm, "end": v(13.5, 25) * mm});
            skLineSegment(sketch, "E3.2.5.2", {"start": v(13.5, 25) * mm, "end": v(8.5, 25) * mm});
            skLineSegment(sketch, "E3.2.5.3", {"start": v(8.5, 30) * mm, "end": v(8.5, 25) * mm});
            skPoint(sketch, "E3.2.5.4", {"position": v(11, 27.5) * mm});
            skLineSegment(sketch, "E3.2.6.0", {"start": v(13.5, 35.5) * mm, "end": v(8.5, 35.5) * mm});
            skLineSegment(sketch, "E3.2.6.1", {"start": v(13.5, 35.5) * mm, "end": v(13.5, 30.5) * mm});
            skLineSegment(sketch, "E3.2.6.2", {"start": v(13.5, 30.5) * mm, "end": v(8.5, 30.5) * mm});
            skLineSegment(sketch, "E3.2.6.3", {"start": v(8.5, 35.5) * mm, "end": v(8.5, 30.5) * mm});
            skPoint(sketch, "E3.2.6.4", {"position": v(11, 33) * mm});
            skLineSegment(sketch, "E3.2.7.0", {"start": v(13.5, 41) * mm, "end": v(8.5, 41) * mm});
            skLineSegment(sketch, "E3.2.7.1", {"start": v(13.5, 41) * mm, "end": v(13.5, 36) * mm});
            skLineSegment(sketch, "E3.2.7.2", {"start": v(13.5, 36) * mm, "end": v(8.5, 36) * mm});
            skLineSegment(sketch, "E3.2.7.3", {"start": v(8.5, 41) * mm, "end": v(8.5, 36) * mm});
            skPoint(sketch, "E3.2.7.4", {"position": v(11, 38.5) * mm});
            skLineSegment(sketch, "E3.2.8.0", {"start": v(13.5, 46.5) * mm, "end": v(8.5, 46.5) * mm});
            skLineSegment(sketch, "E3.2.8.1", {"start": v(13.5, 46.5) * mm, "end": v(13.5, 41.5) * mm});
            skLineSegment(sketch, "E3.2.8.2", {"start": v(13.5, 41.5) * mm, "end": v(8.5, 41.5) * mm});
            skLineSegment(sketch, "E3.2.8.3", {"start": v(8.5, 46.5) * mm, "end": v(8.5, 41.5) * mm});
            skPoint(sketch, "E3.2.8.4", {"position": v(11, 44) * mm});
            skLineSegment(sketch, "E3.2.9.0", {"start": v(13.5, 52) * mm, "end": v(8.5, 52) * mm});
            skLineSegment(sketch, "E3.2.9.1", {"start": v(13.5, 52) * mm, "end": v(13.5, 47) * mm});
            skLineSegment(sketch, "E3.2.9.2", {"start": v(13.5, 47) * mm, "end": v(8.5, 47) * mm});
            skLineSegment(sketch, "E3.2.9.3", {"start": v(8.5, 52) * mm, "end": v(8.5, 47) * mm});
            skPoint(sketch, "E3.2.9.4", {"position": v(11, 49.5) * mm});
            skLineSegment(sketch, "E3.2.10.0", {"start": v(13.5, 57.5) * mm, "end": v(8.5, 57.5) * mm});
            skLineSegment(sketch, "E3.2.10.1", {"start": v(13.5, 57.5) * mm, "end": v(13.5, 52.5) * mm});
            skLineSegment(sketch, "E3.2.10.2", {"start": v(13.5, 52.5) * mm, "end": v(8.5, 52.5) * mm});
            skLineSegment(sketch, "E3.2.10.3", {"start": v(8.5, 57.5) * mm, "end": v(8.5, 52.5) * mm});
            skPoint(sketch, "E3.2.10.4", {"position": v(11, 55) * mm});
            skLineSegment(sketch, "E3.2.11.0", {"start": v(13.5, 63) * mm, "end": v(8.5, 63) * mm});
            skLineSegment(sketch, "E3.2.11.1", {"start": v(13.5, 63) * mm, "end": v(13.5, 58) * mm});
            skLineSegment(sketch, "E3.2.11.2", {"start": v(13.5, 58) * mm, "end": v(8.5, 58) * mm});
            skLineSegment(sketch, "E3.2.11.3", {"start": v(8.5, 63) * mm, "end": v(8.5, 58) * mm});
            skPoint(sketch, "E3.2.11.4", {"position": v(11, 60.5) * mm});
            skLineSegment(sketch, "E3.2.12.0", {"start": v(13.5, 68.5) * mm, "end": v(8.5, 68.5) * mm});
            skLineSegment(sketch, "E3.2.12.1", {"start": v(13.5, 68.5) * mm, "end": v(13.5, 63.5) * mm});
            skLineSegment(sketch, "E3.2.12.2", {"start": v(13.5, 63.5) * mm, "end": v(8.5, 63.5) * mm});
            skLineSegment(sketch, "E3.2.12.3", {"start": v(8.5, 68.5) * mm, "end": v(8.5, 63.5) * mm});
            skPoint(sketch, "E3.2.12.4", {"position": v(11, 66) * mm});
            skLineSegment(sketch, "E3.2.13.0", {"start": v(13.5, 74) * mm, "end": v(8.5, 74) * mm});
            skLineSegment(sketch, "E3.2.13.1", {"start": v(13.5, 74) * mm, "end": v(13.5, 69) * mm});
            skLineSegment(sketch, "E3.2.13.2", {"start": v(13.5, 69) * mm, "end": v(8.5, 69) * mm});
            skLineSegment(sketch, "E3.2.13.3", {"start": v(8.5, 74) * mm, "end": v(8.5, 69) * mm});
            skPoint(sketch, "E3.2.13.4", {"position": v(11, 71.5) * mm});
            skLineSegment(sketch, "E3.2.14.0", {"start": v(13.5, 79.5) * mm, "end": v(8.5, 79.5) * mm});
            skLineSegment(sketch, "E3.2.14.1", {"start": v(13.5, 79.5) * mm, "end": v(13.5, 74.5) * mm});
            skLineSegment(sketch, "E3.2.14.2", {"start": v(13.5, 74.5) * mm, "end": v(8.5, 74.5) * mm});
            skLineSegment(sketch, "E3.2.14.3", {"start": v(8.5, 79.5) * mm, "end": v(8.5, 74.5) * mm});
            skPoint(sketch, "E3.2.14.4", {"position": v(11, 77) * mm});
            skLineSegment(sketch, "E3.2.15.0", {"start": v(13.5, 85) * mm, "end": v(8.5, 85) * mm});
            skLineSegment(sketch, "E3.2.15.1", {"start": v(13.5, 85) * mm, "end": v(13.5, 80) * mm});
            skLineSegment(sketch, "E3.2.15.2", {"start": v(13.5, 80) * mm, "end": v(8.5, 80) * mm});
            skLineSegment(sketch, "E3.2.15.3", {"start": v(8.5, 85) * mm, "end": v(8.5, 80) * mm});
            skPoint(sketch, "E3.2.15.4", {"position": v(11, 82.5) * mm});
            skLineSegment(sketch, "E3.2.16.0", {"start": v(13.5, 90.5) * mm, "end": v(8.5, 90.5) * mm});
            skLineSegment(sketch, "E3.2.16.1", {"start": v(13.5, 90.5) * mm, "end": v(13.5, 85.5) * mm});
            skLineSegment(sketch, "E3.2.16.2", {"start": v(13.5, 85.5) * mm, "end": v(8.5, 85.5) * mm});
            skLineSegment(sketch, "E3.2.16.3", {"start": v(8.5, 90.5) * mm, "end": v(8.5, 85.5) * mm});
            skPoint(sketch, "E3.2.16.4", {"position": v(11, 88) * mm});
            skLineSegment(sketch, "E3.2.17.0", {"start": v(13.5, 96) * mm, "end": v(8.5, 96) * mm});
            skLineSegment(sketch, "E3.2.17.1", {"start": v(13.5, 96) * mm, "end": v(13.5, 91) * mm});
            skLineSegment(sketch, "E3.2.17.2", {"start": v(13.5, 91) * mm, "end": v(8.5, 91) * mm});
            skLineSegment(sketch, "E3.2.17.3", {"start": v(8.5, 96) * mm, "end": v(8.5, 91) * mm});
            skPoint(sketch, "E3.2.17.4", {"position": v(11, 93.5) * mm});
            skLineSegment(sketch, "E3.2.18.0", {"start": v(13.5, 101.5) * mm, "end": v(8.5, 101.5) * mm});
            skLineSegment(sketch, "E3.2.18.1", {"start": v(13.5, 101.5) * mm, "end": v(13.5, 96.5) * mm});
            skLineSegment(sketch, "E3.2.18.2", {"start": v(13.5, 96.5) * mm, "end": v(8.5, 96.5) * mm});
            skLineSegment(sketch, "E3.2.18.3", {"start": v(8.5, 101.5) * mm, "end": v(8.5, 96.5) * mm});
            skPoint(sketch, "E3.2.18.4", {"position": v(11, 99) * mm});
            skLineSegment(sketch, "E3.2.19.0", {"start": v(13.5, 107) * mm, "end": v(8.5, 107) * mm});
            skLineSegment(sketch, "E3.2.19.1", {"start": v(13.5, 107) * mm, "end": v(13.5, 102) * mm});
            skLineSegment(sketch, "E3.2.19.2", {"start": v(13.5, 102) * mm, "end": v(8.5, 102) * mm});
            skLineSegment(sketch, "E3.2.19.3", {"start": v(8.5, 107) * mm, "end": v(8.5, 102) * mm});
            skPoint(sketch, "E3.2.19.4", {"position": v(11, 104.5) * mm});
            skLineSegment(sketch, "E3.2.20.0", {"start": v(13.5, 112.5) * mm, "end": v(8.5, 112.5) * mm});
            skLineSegment(sketch, "E3.2.20.1", {"start": v(13.5, 112.5) * mm, "end": v(13.5, 107.5) * mm});
            skLineSegment(sketch, "E3.2.20.2", {"start": v(13.5, 107.5) * mm, "end": v(8.5, 107.5) * mm});
            skLineSegment(sketch, "E3.2.20.3", {"start": v(8.5, 112.5) * mm, "end": v(8.5, 107.5) * mm});
            skPoint(sketch, "E3.2.20.4", {"position": v(11, 110) * mm});
            skLineSegment(sketch, "E3.2.21.0", {"start": v(13.5, 118) * mm, "end": v(8.5, 118) * mm});
            skLineSegment(sketch, "E3.2.21.1", {"start": v(13.5, 118) * mm, "end": v(13.5, 113) * mm});
            skLineSegment(sketch, "E3.2.21.2", {"start": v(13.5, 113) * mm, "end": v(8.5, 113) * mm});
            skLineSegment(sketch, "E3.2.21.3", {"start": v(8.5, 118) * mm, "end": v(8.5, 113) * mm});
            skPoint(sketch, "E3.2.21.4", {"position": v(11, 115.5) * mm});
            skLineSegment(sketch, "E3.2.22.0", {"start": v(13.5, 123.5) * mm, "end": v(8.5, 123.5) * mm});
            skLineSegment(sketch, "E3.2.22.1", {"start": v(13.5, 123.5) * mm, "end": v(13.5, 118.5) * mm});
            skLineSegment(sketch, "E3.2.22.2", {"start": v(13.5, 118.5) * mm, "end": v(8.5, 118.5) * mm});
            skLineSegment(sketch, "E3.2.22.3", {"start": v(8.5, 123.5) * mm, "end": v(8.5, 118.5) * mm});
            skPoint(sketch, "E3.2.22.4", {"position": v(11, 121) * mm});
            skLineSegment(sketch, "E3.2.23.0", {"start": v(13.5, 129) * mm, "end": v(8.5, 129) * mm});
            skLineSegment(sketch, "E3.2.23.1", {"start": v(13.5, 129) * mm, "end": v(13.5, 124) * mm});
            skLineSegment(sketch, "E3.2.23.2", {"start": v(13.5, 124) * mm, "end": v(8.5, 124) * mm});
            skLineSegment(sketch, "E3.2.23.3", {"start": v(8.5, 129) * mm, "end": v(8.5, 124) * mm});
            skPoint(sketch, "E3.2.23.4", {"position": v(11, 126.5) * mm});
            skLineSegment(sketch, "E3.2.24.0", {"start": v(13.5, 134.5) * mm, "end": v(8.5, 134.5) * mm});
            skLineSegment(sketch, "E3.2.24.1", {"start": v(13.5, 134.5) * mm, "end": v(13.5, 129.5) * mm});
            skLineSegment(sketch, "E3.2.24.2", {"start": v(13.5, 129.5) * mm, "end": v(8.5, 129.5) * mm});
            skLineSegment(sketch, "E3.2.24.3", {"start": v(8.5, 134.5) * mm, "end": v(8.5, 129.5) * mm});
            skPoint(sketch, "E3.2.24.4", {"position": v(11, 132) * mm});
            skLineSegment(sketch, "E3.3.0.0", {"start": v(19, 2.5) * mm, "end": v(14, 2.5) * mm});
            skLineSegment(sketch, "E3.3.0.1", {"start": v(19, 2.5) * mm, "end": v(19, -2.5) * mm});
            skLineSegment(sketch, "E3.3.0.2", {"start": v(19, -2.5) * mm, "end": v(14, -2.5) * mm});
            skLineSegment(sketch, "E3.3.0.3", {"start": v(14, 2.5) * mm, "end": v(14, -2.5) * mm});
            skPoint(sketch, "E3.3.0.4", {"position": v(16.5, 0) * mm});
            skLineSegment(sketch, "E3.3.1.0", {"start": v(19, 8) * mm, "end": v(14, 8) * mm});
            skLineSegment(sketch, "E3.3.1.1", {"start": v(19, 8) * mm, "end": v(19, 3) * mm});
            skLineSegment(sketch, "E3.3.1.2", {"start": v(19, 3) * mm, "end": v(14, 3) * mm});
            skLineSegment(sketch, "E3.3.1.3", {"start": v(14, 8) * mm, "end": v(14, 3) * mm});
            skPoint(sketch, "E3.3.1.4", {"position": v(16.5, 5.5) * mm});
            skLineSegment(sketch, "E3.3.2.0", {"start": v(19, 13.5) * mm, "end": v(14, 13.5) * mm});
            skLineSegment(sketch, "E3.3.2.1", {"start": v(19, 13.5) * mm, "end": v(19, 8.5) * mm});
            skLineSegment(sketch, "E3.3.2.2", {"start": v(19, 8.5) * mm, "end": v(14, 8.5) * mm});
            skLineSegment(sketch, "E3.3.2.3", {"start": v(14, 13.5) * mm, "end": v(14, 8.5) * mm});
            skPoint(sketch, "E3.3.2.4", {"position": v(16.5, 11) * mm});
            skLineSegment(sketch, "E3.3.3.0", {"start": v(19, 19) * mm, "end": v(14, 19) * mm});
            skLineSegment(sketch, "E3.3.3.1", {"start": v(19, 19) * mm, "end": v(19, 14) * mm});
            skLineSegment(sketch, "E3.3.3.2", {"start": v(19, 14) * mm, "end": v(14, 14) * mm});
            skLineSegment(sketch, "E3.3.3.3", {"start": v(14, 19) * mm, "end": v(14, 14) * mm});
            skPoint(sketch, "E3.3.3.4", {"position": v(16.5, 16.5) * mm});
            skLineSegment(sketch, "E3.3.4.0", {"start": v(19, 24.5) * mm, "end": v(14, 24.5) * mm});
            skLineSegment(sketch, "E3.3.4.1", {"start": v(19, 24.5) * mm, "end": v(19, 19.5) * mm});
            skLineSegment(sketch, "E3.3.4.2", {"start": v(19, 19.5) * mm, "end": v(14, 19.5) * mm});
            skLineSegment(sketch, "E3.3.4.3", {"start": v(14, 24.5) * mm, "end": v(14, 19.5) * mm});
            skPoint(sketch, "E3.3.4.4", {"position": v(16.5, 22) * mm});
            skLineSegment(sketch, "E3.3.5.0", {"start": v(19, 30) * mm, "end": v(14, 30) * mm});
            skLineSegment(sketch, "E3.3.5.1", {"start": v(19, 30) * mm, "end": v(19, 25) * mm});
            skLineSegment(sketch, "E3.3.5.2", {"start": v(19, 25) * mm, "end": v(14, 25) * mm});
            skLineSegment(sketch, "E3.3.5.3", {"start": v(14, 30) * mm, "end": v(14, 25) * mm});
            skPoint(sketch, "E3.3.5.4", {"position": v(16.5, 27.5) * mm});
            skLineSegment(sketch, "E3.3.6.0", {"start": v(19, 35.5) * mm, "end": v(14, 35.5) * mm});
            skLineSegment(sketch, "E3.3.6.1", {"start": v(19, 35.5) * mm, "end": v(19, 30.5) * mm});
            skLineSegment(sketch, "E3.3.6.2", {"start": v(19, 30.5) * mm, "end": v(14, 30.5) * mm});
            skLineSegment(sketch, "E3.3.6.3", {"start": v(14, 35.5) * mm, "end": v(14, 30.5) * mm});
            skPoint(sketch, "E3.3.6.4", {"position": v(16.5, 33) * mm});
            skLineSegment(sketch, "E3.3.7.0", {"start": v(19, 41) * mm, "end": v(14, 41) * mm});
            skLineSegment(sketch, "E3.3.7.1", {"start": v(19, 41) * mm, "end": v(19, 36) * mm});
            skLineSegment(sketch, "E3.3.7.2", {"start": v(19, 36) * mm, "end": v(14, 36) * mm});
            skLineSegment(sketch, "E3.3.7.3", {"start": v(14, 41) * mm, "end": v(14, 36) * mm});
            skPoint(sketch, "E3.3.7.4", {"position": v(16.5, 38.5) * mm});
            skLineSegment(sketch, "E3.3.8.0", {"start": v(19, 46.5) * mm, "end": v(14, 46.5) * mm});
            skLineSegment(sketch, "E3.3.8.1", {"start": v(19, 46.5) * mm, "end": v(19, 41.5) * mm});
            skLineSegment(sketch, "E3.3.8.2", {"start": v(19, 41.5) * mm, "end": v(14, 41.5) * mm});
            skLineSegment(sketch, "E3.3.8.3", {"start": v(14, 46.5) * mm, "end": v(14, 41.5) * mm});
            skPoint(sketch, "E3.3.8.4", {"position": v(16.5, 44) * mm});
            skLineSegment(sketch, "E3.3.9.0", {"start": v(19, 52) * mm, "end": v(14, 52) * mm});
            skLineSegment(sketch, "E3.3.9.1", {"start": v(19, 52) * mm, "end": v(19, 47) * mm});
            skLineSegment(sketch, "E3.3.9.2", {"start": v(19, 47) * mm, "end": v(14, 47) * mm});
            skLineSegment(sketch, "E3.3.9.3", {"start": v(14, 52) * mm, "end": v(14, 47) * mm});
            skPoint(sketch, "E3.3.9.4", {"position": v(16.5, 49.5) * mm});
            skLineSegment(sketch, "E3.3.10.0", {"start": v(19, 57.5) * mm, "end": v(14, 57.5) * mm});
            skLineSegment(sketch, "E3.3.10.1", {"start": v(19, 57.5) * mm, "end": v(19, 52.5) * mm});
            skLineSegment(sketch, "E3.3.10.2", {"start": v(19, 52.5) * mm, "end": v(14, 52.5) * mm});
            skLineSegment(sketch, "E3.3.10.3", {"start": v(14, 57.5) * mm, "end": v(14, 52.5) * mm});
            skPoint(sketch, "E3.3.10.4", {"position": v(16.5, 55) * mm});
            skLineSegment(sketch, "E3.3.11.0", {"start": v(19, 63) * mm, "end": v(14, 63) * mm});
            skLineSegment(sketch, "E3.3.11.1", {"start": v(19, 63) * mm, "end": v(19, 58) * mm});
            skLineSegment(sketch, "E3.3.11.2", {"start": v(19, 58) * mm, "end": v(14, 58) * mm});
            skLineSegment(sketch, "E3.3.11.3", {"start": v(14, 63) * mm, "end": v(14, 58) * mm});
            skPoint(sketch, "E3.3.11.4", {"position": v(16.5, 60.5) * mm});
            skLineSegment(sketch, "E3.3.12.0", {"start": v(19, 68.5) * mm, "end": v(14, 68.5) * mm});
            skLineSegment(sketch, "E3.3.12.1", {"start": v(19, 68.5) * mm, "end": v(19, 63.5) * mm});
            skLineSegment(sketch, "E3.3.12.2", {"start": v(19, 63.5) * mm, "end": v(14, 63.5) * mm});
            skLineSegment(sketch, "E3.3.12.3", {"start": v(14, 68.5) * mm, "end": v(14, 63.5) * mm});
            skPoint(sketch, "E3.3.12.4", {"position": v(16.5, 66) * mm});
            skLineSegment(sketch, "E3.3.13.0", {"start": v(19, 74) * mm, "end": v(14, 74) * mm});
            skLineSegment(sketch, "E3.3.13.1", {"start": v(19, 74) * mm, "end": v(19, 69) * mm});
            skLineSegment(sketch, "E3.3.13.2", {"start": v(19, 69) * mm, "end": v(14, 69) * mm});
            skLineSegment(sketch, "E3.3.13.3", {"start": v(14, 74) * mm, "end": v(14, 69) * mm});
            skPoint(sketch, "E3.3.13.4", {"position": v(16.5, 71.5) * mm});
            skLineSegment(sketch, "E3.3.14.0", {"start": v(19, 79.5) * mm, "end": v(14, 79.5) * mm});
            skLineSegment(sketch, "E3.3.14.1", {"start": v(19, 79.5) * mm, "end": v(19, 74.5) * mm});
            skLineSegment(sketch, "E3.3.14.2", {"start": v(19, 74.5) * mm, "end": v(14, 74.5) * mm});
            skLineSegment(sketch, "E3.3.14.3", {"start": v(14, 79.5) * mm, "end": v(14, 74.5) * mm});
            skPoint(sketch, "E3.3.14.4", {"position": v(16.5, 77) * mm});
            skLineSegment(sketch, "E3.3.15.0", {"start": v(19, 85) * mm, "end": v(14, 85) * mm});
            skLineSegment(sketch, "E3.3.15.1", {"start": v(19, 85) * mm, "end": v(19, 80) * mm});
            skLineSegment(sketch, "E3.3.15.2", {"start": v(19, 80) * mm, "end": v(14, 80) * mm});
            skLineSegment(sketch, "E3.3.15.3", {"start": v(14, 85) * mm, "end": v(14, 80) * mm});
            skPoint(sketch, "E3.3.15.4", {"position": v(16.5, 82.5) * mm});
            skLineSegment(sketch, "E3.3.16.0", {"start": v(19, 90.5) * mm, "end": v(14, 90.5) * mm});
            skLineSegment(sketch, "E3.3.16.1", {"start": v(19, 90.5) * mm, "end": v(19, 85.5) * mm});
            skLineSegment(sketch, "E3.3.16.2", {"start": v(19, 85.5) * mm, "end": v(14, 85.5) * mm});
            skLineSegment(sketch, "E3.3.16.3", {"start": v(14, 90.5) * mm, "end": v(14, 85.5) * mm});
            skPoint(sketch, "E3.3.16.4", {"position": v(16.5, 88) * mm});
            skLineSegment(sketch, "E3.3.17.0", {"start": v(19, 96) * mm, "end": v(14, 96) * mm});
            skLineSegment(sketch, "E3.3.17.1", {"start": v(19, 96) * mm, "end": v(19, 91) * mm});
            skLineSegment(sketch, "E3.3.17.2", {"start": v(19, 91) * mm, "end": v(14, 91) * mm});
            skLineSegment(sketch, "E3.3.17.3", {"start": v(14, 96) * mm, "end": v(14, 91) * mm});
            skPoint(sketch, "E3.3.17.4", {"position": v(16.5, 93.5) * mm});
            skLineSegment(sketch, "E3.3.18.0", {"start": v(19, 101.5) * mm, "end": v(14, 101.5) * mm});
            skLineSegment(sketch, "E3.3.18.1", {"start": v(19, 101.5) * mm, "end": v(19, 96.5) * mm});
            skLineSegment(sketch, "E3.3.18.2", {"start": v(19, 96.5) * mm, "end": v(14, 96.5) * mm});
            skLineSegment(sketch, "E3.3.18.3", {"start": v(14, 101.5) * mm, "end": v(14, 96.5) * mm});
            skPoint(sketch, "E3.3.18.4", {"position": v(16.5, 99) * mm});
            skLineSegment(sketch, "E3.3.19.0", {"start": v(19, 107) * mm, "end": v(14, 107) * mm});
            skLineSegment(sketch, "E3.3.19.1", {"start": v(19, 107) * mm, "end": v(19, 102) * mm});
            skLineSegment(sketch, "E3.3.19.2", {"start": v(19, 102) * mm, "end": v(14, 102) * mm});
            skLineSegment(sketch, "E3.3.19.3", {"start": v(14, 107) * mm, "end": v(14, 102) * mm});
            skPoint(sketch, "E3.3.19.4", {"position": v(16.5, 104.5) * mm});
            skLineSegment(sketch, "E3.3.20.0", {"start": v(19, 112.5) * mm, "end": v(14, 112.5) * mm});
            skLineSegment(sketch, "E3.3.20.1", {"start": v(19, 112.5) * mm, "end": v(19, 107.5) * mm});
            skLineSegment(sketch, "E3.3.20.2", {"start": v(19, 107.5) * mm, "end": v(14, 107.5) * mm});
            skLineSegment(sketch, "E3.3.20.3", {"start": v(14, 112.5) * mm, "end": v(14, 107.5) * mm});
            skPoint(sketch, "E3.3.20.4", {"position": v(16.5, 110) * mm});
            skLineSegment(sketch, "E3.3.21.0", {"start": v(19, 118) * mm, "end": v(14, 118) * mm});
            skLineSegment(sketch, "E3.3.21.1", {"start": v(19, 118) * mm, "end": v(19, 113) * mm});
            skLineSegment(sketch, "E3.3.21.2", {"start": v(19, 113) * mm, "end": v(14, 113) * mm});
            skLineSegment(sketch, "E3.3.21.3", {"start": v(14, 118) * mm, "end": v(14, 113) * mm});
            skPoint(sketch, "E3.3.21.4", {"position": v(16.5, 115.5) * mm});
            skLineSegment(sketch, "E3.3.22.0", {"start": v(19, 123.5) * mm, "end": v(14, 123.5) * mm});
            skLineSegment(sketch, "E3.3.22.1", {"start": v(19, 123.5) * mm, "end": v(19, 118.5) * mm});
            skLineSegment(sketch, "E3.3.22.2", {"start": v(19, 118.5) * mm, "end": v(14, 118.5) * mm});
            skLineSegment(sketch, "E3.3.22.3", {"start": v(14, 123.5) * mm, "end": v(14, 118.5) * mm});
            skPoint(sketch, "E3.3.22.4", {"position": v(16.5, 121) * mm});
            skLineSegment(sketch, "E3.3.23.0", {"start": v(19, 129) * mm, "end": v(14, 129) * mm});
            skLineSegment(sketch, "E3.3.23.1", {"start": v(19, 129) * mm, "end": v(19, 124) * mm});
            skLineSegment(sketch, "E3.3.23.2", {"start": v(19, 124) * mm, "end": v(14, 124) * mm});
            skLineSegment(sketch, "E3.3.23.3", {"start": v(14, 129) * mm, "end": v(14, 124) * mm});
            skPoint(sketch, "E3.3.23.4", {"position": v(16.5, 126.5) * mm});
            skLineSegment(sketch, "E3.3.24.0", {"start": v(19, 134.5) * mm, "end": v(14, 134.5) * mm});
            skLineSegment(sketch, "E3.3.24.1", {"start": v(19, 134.5) * mm, "end": v(19, 129.5) * mm});
            skLineSegment(sketch, "E3.3.24.2", {"start": v(19, 129.5) * mm, "end": v(14, 129.5) * mm});
            skLineSegment(sketch, "E3.3.24.3", {"start": v(14, 134.5) * mm, "end": v(14, 129.5) * mm});
            skPoint(sketch, "E3.3.24.4", {"position": v(16.5, 132) * mm});
            skLineSegment(sketch, "E3.4.0.0", {"start": v(24.5, 2.5) * mm, "end": v(19.5, 2.5) * mm});
            skLineSegment(sketch, "E3.4.0.1", {"start": v(24.5, 2.5) * mm, "end": v(24.5, -2.5) * mm});
            skLineSegment(sketch, "E3.4.0.2", {"start": v(24.5, -2.5) * mm, "end": v(19.5, -2.5) * mm});
            skLineSegment(sketch, "E3.4.0.3", {"start": v(19.5, 2.5) * mm, "end": v(19.5, -2.5) * mm});
            skPoint(sketch, "E3.4.0.4", {"position": v(22, 0) * mm});
            skLineSegment(sketch, "E3.4.1.0", {"start": v(24.5, 8) * mm, "end": v(19.5, 8) * mm});
            skLineSegment(sketch, "E3.4.1.1", {"start": v(24.5, 8) * mm, "end": v(24.5, 3) * mm});
            skLineSegment(sketch, "E3.4.1.2", {"start": v(24.5, 3) * mm, "end": v(19.5, 3) * mm});
            skLineSegment(sketch, "E3.4.1.3", {"start": v(19.5, 8) * mm, "end": v(19.5, 3) * mm});
            skPoint(sketch, "E3.4.1.4", {"position": v(22, 5.5) * mm});
            skLineSegment(sketch, "E3.4.2.0", {"start": v(24.5, 13.5) * mm, "end": v(19.5, 13.5) * mm});
            skLineSegment(sketch, "E3.4.2.1", {"start": v(24.5, 13.5) * mm, "end": v(24.5, 8.5) * mm});
            skLineSegment(sketch, "E3.4.2.2", {"start": v(24.5, 8.5) * mm, "end": v(19.5, 8.5) * mm});
            skLineSegment(sketch, "E3.4.2.3", {"start": v(19.5, 13.5) * mm, "end": v(19.5, 8.5) * mm});
            skPoint(sketch, "E3.4.2.4", {"position": v(22, 11) * mm});
            skLineSegment(sketch, "E3.4.3.0", {"start": v(24.5, 19) * mm, "end": v(19.5, 19) * mm});
            skLineSegment(sketch, "E3.4.3.1", {"start": v(24.5, 19) * mm, "end": v(24.5, 14) * mm});
            skLineSegment(sketch, "E3.4.3.2", {"start": v(24.5, 14) * mm, "end": v(19.5, 14) * mm});
            skLineSegment(sketch, "E3.4.3.3", {"start": v(19.5, 19) * mm, "end": v(19.5, 14) * mm});
            skPoint(sketch, "E3.4.3.4", {"position": v(22, 16.5) * mm});
            skLineSegment(sketch, "E3.4.4.0", {"start": v(24.5, 24.5) * mm, "end": v(19.5, 24.5) * mm});
            skLineSegment(sketch, "E3.4.4.1", {"start": v(24.5, 24.5) * mm, "end": v(24.5, 19.5) * mm});
            skLineSegment(sketch, "E3.4.4.2", {"start": v(24.5, 19.5) * mm, "end": v(19.5, 19.5) * mm});
            skLineSegment(sketch, "E3.4.4.3", {"start": v(19.5, 24.5) * mm, "end": v(19.5, 19.5) * mm});
            skPoint(sketch, "E3.4.4.4", {"position": v(22, 22) * mm});
            skLineSegment(sketch, "E3.4.5.0", {"start": v(24.5, 30) * mm, "end": v(19.5, 30) * mm});
            skLineSegment(sketch, "E3.4.5.1", {"start": v(24.5, 30) * mm, "end": v(24.5, 25) * mm});
            skLineSegment(sketch, "E3.4.5.2", {"start": v(24.5, 25) * mm, "end": v(19.5, 25) * mm});
            skLineSegment(sketch, "E3.4.5.3", {"start": v(19.5, 30) * mm, "end": v(19.5, 25) * mm});
            skPoint(sketch, "E3.4.5.4", {"position": v(22, 27.5) * mm});
            skLineSegment(sketch, "E3.4.6.0", {"start": v(24.5, 35.5) * mm, "end": v(19.5, 35.5) * mm});
            skLineSegment(sketch, "E3.4.6.1", {"start": v(24.5, 35.5) * mm, "end": v(24.5, 30.5) * mm});
            skLineSegment(sketch, "E3.4.6.2", {"start": v(24.5, 30.5) * mm, "end": v(19.5, 30.5) * mm});
            skLineSegment(sketch, "E3.4.6.3", {"start": v(19.5, 35.5) * mm, "end": v(19.5, 30.5) * mm});
            skPoint(sketch, "E3.4.6.4", {"position": v(22, 33) * mm});
            skLineSegment(sketch, "E3.4.7.0", {"start": v(24.5, 41) * mm, "end": v(19.5, 41) * mm});
            skLineSegment(sketch, "E3.4.7.1", {"start": v(24.5, 41) * mm, "end": v(24.5, 36) * mm});
            skLineSegment(sketch, "E3.4.7.2", {"start": v(24.5, 36) * mm, "end": v(19.5, 36) * mm});
            skLineSegment(sketch, "E3.4.7.3", {"start": v(19.5, 41) * mm, "end": v(19.5, 36) * mm});
            skPoint(sketch, "E3.4.7.4", {"position": v(22, 38.5) * mm});
            skLineSegment(sketch, "E3.4.8.0", {"start": v(24.5, 46.5) * mm, "end": v(19.5, 46.5) * mm});
            skLineSegment(sketch, "E3.4.8.1", {"start": v(24.5, 46.5) * mm, "end": v(24.5, 41.5) * mm});
            skLineSegment(sketch, "E3.4.8.2", {"start": v(24.5, 41.5) * mm, "end": v(19.5, 41.5) * mm});
            skLineSegment(sketch, "E3.4.8.3", {"start": v(19.5, 46.5) * mm, "end": v(19.5, 41.5) * mm});
            skPoint(sketch, "E3.4.8.4", {"position": v(22, 44) * mm});
            skLineSegment(sketch, "E3.4.9.0", {"start": v(24.5, 52) * mm, "end": v(19.5, 52) * mm});
            skLineSegment(sketch, "E3.4.9.1", {"start": v(24.5, 52) * mm, "end": v(24.5, 47) * mm});
            skLineSegment(sketch, "E3.4.9.2", {"start": v(24.5, 47) * mm, "end": v(19.5, 47) * mm});
            skLineSegment(sketch, "E3.4.9.3", {"start": v(19.5, 52) * mm, "end": v(19.5, 47) * mm});
            skPoint(sketch, "E3.4.9.4", {"position": v(22, 49.5) * mm});
            skLineSegment(sketch, "E3.4.10.0", {"start": v(24.5, 57.5) * mm, "end": v(19.5, 57.5) * mm});
            skLineSegment(sketch, "E3.4.10.1", {"start": v(24.5, 57.5) * mm, "end": v(24.5, 52.5) * mm});
            skLineSegment(sketch, "E3.4.10.2", {"start": v(24.5, 52.5) * mm, "end": v(19.5, 52.5) * mm});
            skLineSegment(sketch, "E3.4.10.3", {"start": v(19.5, 57.5) * mm, "end": v(19.5, 52.5) * mm});
            skPoint(sketch, "E3.4.10.4", {"position": v(22, 55) * mm});
            skLineSegment(sketch, "E3.4.11.0", {"start": v(24.5, 63) * mm, "end": v(19.5, 63) * mm});
            skLineSegment(sketch, "E3.4.11.1", {"start": v(24.5, 63) * mm, "end": v(24.5, 58) * mm});
            skLineSegment(sketch, "E3.4.11.2", {"start": v(24.5, 58) * mm, "end": v(19.5, 58) * mm});
            skLineSegment(sketch, "E3.4.11.3", {"start": v(19.5, 63) * mm, "end": v(19.5, 58) * mm});
            skPoint(sketch, "E3.4.11.4", {"position": v(22, 60.5) * mm});
            skLineSegment(sketch, "E3.4.12.0", {"start": v(24.5, 68.5) * mm, "end": v(19.5, 68.5) * mm});
            skLineSegment(sketch, "E3.4.12.1", {"start": v(24.5, 68.5) * mm, "end": v(24.5, 63.5) * mm});
            skLineSegment(sketch, "E3.4.12.2", {"start": v(24.5, 63.5) * mm, "end": v(19.5, 63.5) * mm});
            skLineSegment(sketch, "E3.4.12.3", {"start": v(19.5, 68.5) * mm, "end": v(19.5, 63.5) * mm});
            skPoint(sketch, "E3.4.12.4", {"position": v(22, 66) * mm});
            skLineSegment(sketch, "E3.4.13.0", {"start": v(24.5, 74) * mm, "end": v(19.5, 74) * mm});
            skLineSegment(sketch, "E3.4.13.1", {"start": v(24.5, 74) * mm, "end": v(24.5, 69) * mm});
            skLineSegment(sketch, "E3.4.13.2", {"start": v(24.5, 69) * mm, "end": v(19.5, 69) * mm});
            skLineSegment(sketch, "E3.4.13.3", {"start": v(19.5, 74) * mm, "end": v(19.5, 69) * mm});
            skPoint(sketch, "E3.4.13.4", {"position": v(22, 71.5) * mm});
            skLineSegment(sketch, "E3.4.14.0", {"start": v(24.5, 79.5) * mm, "end": v(19.5, 79.5) * mm});
            skLineSegment(sketch, "E3.4.14.1", {"start": v(24.5, 79.5) * mm, "end": v(24.5, 74.5) * mm});
            skLineSegment(sketch, "E3.4.14.2", {"start": v(24.5, 74.5) * mm, "end": v(19.5, 74.5) * mm});
            skLineSegment(sketch, "E3.4.14.3", {"start": v(19.5, 79.5) * mm, "end": v(19.5, 74.5) * mm});
            skPoint(sketch, "E3.4.14.4", {"position": v(22, 77) * mm});
            skLineSegment(sketch, "E3.4.15.0", {"start": v(24.5, 85) * mm, "end": v(19.5, 85) * mm});
            skLineSegment(sketch, "E3.4.15.1", {"start": v(24.5, 85) * mm, "end": v(24.5, 80) * mm});
            skLineSegment(sketch, "E3.4.15.2", {"start": v(24.5, 80) * mm, "end": v(19.5, 80) * mm});
            skLineSegment(sketch, "E3.4.15.3", {"start": v(19.5, 85) * mm, "end": v(19.5, 80) * mm});
            skPoint(sketch, "E3.4.15.4", {"position": v(22, 82.5) * mm});
            skLineSegment(sketch, "E3.4.16.0", {"start": v(24.5, 90.5) * mm, "end": v(19.5, 90.5) * mm});
            skLineSegment(sketch, "E3.4.16.1", {"start": v(24.5, 90.5) * mm, "end": v(24.5, 85.5) * mm});
            skLineSegment(sketch, "E3.4.16.2", {"start": v(24.5, 85.5) * mm, "end": v(19.5, 85.5) * mm});
            skLineSegment(sketch, "E3.4.16.3", {"start": v(19.5, 90.5) * mm, "end": v(19.5, 85.5) * mm});
            skPoint(sketch, "E3.4.16.4", {"position": v(22, 88) * mm});
            skLineSegment(sketch, "E3.4.17.0", {"start": v(24.5, 96) * mm, "end": v(19.5, 96) * mm});
            skLineSegment(sketch, "E3.4.17.1", {"start": v(24.5, 96) * mm, "end": v(24.5, 91) * mm});
            skLineSegment(sketch, "E3.4.17.2", {"start": v(24.5, 91) * mm, "end": v(19.5, 91) * mm});
            skLineSegment(sketch, "E3.4.17.3", {"start": v(19.5, 96) * mm, "end": v(19.5, 91) * mm});
            skPoint(sketch, "E3.4.17.4", {"position": v(22, 93.5) * mm});
            skLineSegment(sketch, "E3.4.18.0", {"start": v(24.5, 101.5) * mm, "end": v(19.5, 101.5) * mm});
            skLineSegment(sketch, "E3.4.18.1", {"start": v(24.5, 101.5) * mm, "end": v(24.5, 96.5) * mm});
            skLineSegment(sketch, "E3.4.18.2", {"start": v(24.5, 96.5) * mm, "end": v(19.5, 96.5) * mm});
            skLineSegment(sketch, "E3.4.18.3", {"start": v(19.5, 101.5) * mm, "end": v(19.5, 96.5) * mm});
            skPoint(sketch, "E3.4.18.4", {"position": v(22, 99) * mm});
            skLineSegment(sketch, "E3.4.19.0", {"start": v(24.5, 107) * mm, "end": v(19.5, 107) * mm});
            skLineSegment(sketch, "E3.4.19.1", {"start": v(24.5, 107) * mm, "end": v(24.5, 102) * mm});
            skLineSegment(sketch, "E3.4.19.2", {"start": v(24.5, 102) * mm, "end": v(19.5, 102) * mm});
            skLineSegment(sketch, "E3.4.19.3", {"start": v(19.5, 107) * mm, "end": v(19.5, 102) * mm});
            skPoint(sketch, "E3.4.19.4", {"position": v(22, 104.5) * mm});
            skLineSegment(sketch, "E3.4.20.0", {"start": v(24.5, 112.5) * mm, "end": v(19.5, 112.5) * mm});
            skLineSegment(sketch, "E3.4.20.1", {"start": v(24.5, 112.5) * mm, "end": v(24.5, 107.5) * mm});
            skLineSegment(sketch, "E3.4.20.2", {"start": v(24.5, 107.5) * mm, "end": v(19.5, 107.5) * mm});
            skLineSegment(sketch, "E3.4.20.3", {"start": v(19.5, 112.5) * mm, "end": v(19.5, 107.5) * mm});
            skPoint(sketch, "E3.4.20.4", {"position": v(22, 110) * mm});
            skLineSegment(sketch, "E3.4.21.0", {"start": v(24.5, 118) * mm, "end": v(19.5, 118) * mm});
            skLineSegment(sketch, "E3.4.21.1", {"start": v(24.5, 118) * mm, "end": v(24.5, 113) * mm});
            skLineSegment(sketch, "E3.4.21.2", {"start": v(24.5, 113) * mm, "end": v(19.5, 113) * mm});
            skLineSegment(sketch, "E3.4.21.3", {"start": v(19.5, 118) * mm, "end": v(19.5, 113) * mm});
            skPoint(sketch, "E3.4.21.4", {"position": v(22, 115.5) * mm});
            skLineSegment(sketch, "E3.4.22.0", {"start": v(24.5, 123.5) * mm, "end": v(19.5, 123.5) * mm});
            skLineSegment(sketch, "E3.4.22.1", {"start": v(24.5, 123.5) * mm, "end": v(24.5, 118.5) * mm});
            skLineSegment(sketch, "E3.4.22.2", {"start": v(24.5, 118.5) * mm, "end": v(19.5, 118.5) * mm});
            skLineSegment(sketch, "E3.4.22.3", {"start": v(19.5, 123.5) * mm, "end": v(19.5, 118.5) * mm});
            skPoint(sketch, "E3.4.22.4", {"position": v(22, 121) * mm});
            skLineSegment(sketch, "E3.4.23.0", {"start": v(24.5, 129) * mm, "end": v(19.5, 129) * mm});
            skLineSegment(sketch, "E3.4.23.1", {"start": v(24.5, 129) * mm, "end": v(24.5, 124) * mm});
            skLineSegment(sketch, "E3.4.23.2", {"start": v(24.5, 124) * mm, "end": v(19.5, 124) * mm});
            skLineSegment(sketch, "E3.4.23.3", {"start": v(19.5, 129) * mm, "end": v(19.5, 124) * mm});
            skPoint(sketch, "E3.4.23.4", {"position": v(22, 126.5) * mm});
            skLineSegment(sketch, "E3.4.24.0", {"start": v(24.5, 134.5) * mm, "end": v(19.5, 134.5) * mm});
            skLineSegment(sketch, "E3.4.24.1", {"start": v(24.5, 134.5) * mm, "end": v(24.5, 129.5) * mm});
            skLineSegment(sketch, "E3.4.24.2", {"start": v(24.5, 129.5) * mm, "end": v(19.5, 129.5) * mm});
            skLineSegment(sketch, "E3.4.24.3", {"start": v(19.5, 134.5) * mm, "end": v(19.5, 129.5) * mm});
            skPoint(sketch, "E3.4.24.4", {"position": v(22, 132) * mm});
            skLineSegment(sketch, "E3.5.0.0", {"start": v(30, 2.5) * mm, "end": v(25, 2.5) * mm});
            skLineSegment(sketch, "E3.5.0.1", {"start": v(30, 2.5) * mm, "end": v(30, -2.5) * mm});
            skLineSegment(sketch, "E3.5.0.2", {"start": v(30, -2.5) * mm, "end": v(25, -2.5) * mm});
            skLineSegment(sketch, "E3.5.0.3", {"start": v(25, 2.5) * mm, "end": v(25, -2.5) * mm});
            skPoint(sketch, "E3.5.0.4", {"position": v(27.5, 0) * mm});
            skLineSegment(sketch, "E3.5.1.0", {"start": v(30, 8) * mm, "end": v(25, 8) * mm});
            skLineSegment(sketch, "E3.5.1.1", {"start": v(30, 8) * mm, "end": v(30, 3) * mm});
            skLineSegment(sketch, "E3.5.1.2", {"start": v(30, 3) * mm, "end": v(25, 3) * mm});
            skLineSegment(sketch, "E3.5.1.3", {"start": v(25, 8) * mm, "end": v(25, 3) * mm});
            skPoint(sketch, "E3.5.1.4", {"position": v(27.5, 5.5) * mm});
            skLineSegment(sketch, "E3.5.2.0", {"start": v(30, 13.5) * mm, "end": v(25, 13.5) * mm});
            skLineSegment(sketch, "E3.5.2.1", {"start": v(30, 13.5) * mm, "end": v(30, 8.5) * mm});
            skLineSegment(sketch, "E3.5.2.2", {"start": v(30, 8.5) * mm, "end": v(25, 8.5) * mm});
            skLineSegment(sketch, "E3.5.2.3", {"start": v(25, 13.5) * mm, "end": v(25, 8.5) * mm});
            skPoint(sketch, "E3.5.2.4", {"position": v(27.5, 11) * mm});
            skLineSegment(sketch, "E3.5.3.0", {"start": v(30, 19) * mm, "end": v(25, 19) * mm});
            skLineSegment(sketch, "E3.5.3.1", {"start": v(30, 19) * mm, "end": v(30, 14) * mm});
            skLineSegment(sketch, "E3.5.3.2", {"start": v(30, 14) * mm, "end": v(25, 14) * mm});
            skLineSegment(sketch, "E3.5.3.3", {"start": v(25, 19) * mm, "end": v(25, 14) * mm});
            skPoint(sketch, "E3.5.3.4", {"position": v(27.5, 16.5) * mm});
            skLineSegment(sketch, "E3.5.4.0", {"start": v(30, 24.5) * mm, "end": v(25, 24.5) * mm});
            skLineSegment(sketch, "E3.5.4.1", {"start": v(30, 24.5) * mm, "end": v(30, 19.5) * mm});
            skLineSegment(sketch, "E3.5.4.2", {"start": v(30, 19.5) * mm, "end": v(25, 19.5) * mm});
            skLineSegment(sketch, "E3.5.4.3", {"start": v(25, 24.5) * mm, "end": v(25, 19.5) * mm});
            skPoint(sketch, "E3.5.4.4", {"position": v(27.5, 22) * mm});
            skLineSegment(sketch, "E3.5.5.0", {"start": v(30, 30) * mm, "end": v(25, 30) * mm});
            skLineSegment(sketch, "E3.5.5.1", {"start": v(30, 30) * mm, "end": v(30, 25) * mm});
            skLineSegment(sketch, "E3.5.5.2", {"start": v(30, 25) * mm, "end": v(25, 25) * mm});
            skLineSegment(sketch, "E3.5.5.3", {"start": v(25, 30) * mm, "end": v(25, 25) * mm});
            skPoint(sketch, "E3.5.5.4", {"position": v(27.5, 27.5) * mm});
            skLineSegment(sketch, "E3.5.6.0", {"start": v(30, 35.5) * mm, "end": v(25, 35.5) * mm});
            skLineSegment(sketch, "E3.5.6.1", {"start": v(30, 35.5) * mm, "end": v(30, 30.5) * mm});
            skLineSegment(sketch, "E3.5.6.2", {"start": v(30, 30.5) * mm, "end": v(25, 30.5) * mm});
            skLineSegment(sketch, "E3.5.6.3", {"start": v(25, 35.5) * mm, "end": v(25, 30.5) * mm});
            skPoint(sketch, "E3.5.6.4", {"position": v(27.5, 33) * mm});
            skLineSegment(sketch, "E3.5.7.0", {"start": v(30, 41) * mm, "end": v(25, 41) * mm});
            skLineSegment(sketch, "E3.5.7.1", {"start": v(30, 41) * mm, "end": v(30, 36) * mm});
            skLineSegment(sketch, "E3.5.7.2", {"start": v(30, 36) * mm, "end": v(25, 36) * mm});
            skLineSegment(sketch, "E3.5.7.3", {"start": v(25, 41) * mm, "end": v(25, 36) * mm});
            skPoint(sketch, "E3.5.7.4", {"position": v(27.5, 38.5) * mm});
            skLineSegment(sketch, "E3.5.8.0", {"start": v(30, 46.5) * mm, "end": v(25, 46.5) * mm});
            skLineSegment(sketch, "E3.5.8.1", {"start": v(30, 46.5) * mm, "end": v(30, 41.5) * mm});
            skLineSegment(sketch, "E3.5.8.2", {"start": v(30, 41.5) * mm, "end": v(25, 41.5) * mm});
            skLineSegment(sketch, "E3.5.8.3", {"start": v(25, 46.5) * mm, "end": v(25, 41.5) * mm});
            skPoint(sketch, "E3.5.8.4", {"position": v(27.5, 44) * mm});
            skLineSegment(sketch, "E3.5.9.0", {"start": v(30, 52) * mm, "end": v(25, 52) * mm});
            skLineSegment(sketch, "E3.5.9.1", {"start": v(30, 52) * mm, "end": v(30, 47) * mm});
            skLineSegment(sketch, "E3.5.9.2", {"start": v(30, 47) * mm, "end": v(25, 47) * mm});
            skLineSegment(sketch, "E3.5.9.3", {"start": v(25, 52) * mm, "end": v(25, 47) * mm});
            skPoint(sketch, "E3.5.9.4", {"position": v(27.5, 49.5) * mm});
            skLineSegment(sketch, "E3.5.10.0", {"start": v(30, 57.5) * mm, "end": v(25, 57.5) * mm});
            skLineSegment(sketch, "E3.5.10.1", {"start": v(30, 57.5) * mm, "end": v(30, 52.5) * mm});
            skLineSegment(sketch, "E3.5.10.2", {"start": v(30, 52.5) * mm, "end": v(25, 52.5) * mm});
            skLineSegment(sketch, "E3.5.10.3", {"start": v(25, 57.5) * mm, "end": v(25, 52.5) * mm});
            skPoint(sketch, "E3.5.10.4", {"position": v(27.5, 55) * mm});
            skLineSegment(sketch, "E3.5.11.0", {"start": v(30, 63) * mm, "end": v(25, 63) * mm});
            skLineSegment(sketch, "E3.5.11.1", {"start": v(30, 63) * mm, "end": v(30, 58) * mm});
            skLineSegment(sketch, "E3.5.11.2", {"start": v(30, 58) * mm, "end": v(25, 58) * mm});
            skLineSegment(sketch, "E3.5.11.3", {"start": v(25, 63) * mm, "end": v(25, 58) * mm});
            skPoint(sketch, "E3.5.11.4", {"position": v(27.5, 60.5) * mm});
            skLineSegment(sketch, "E3.5.12.0", {"start": v(30, 68.5) * mm, "end": v(25, 68.5) * mm});
            skLineSegment(sketch, "E3.5.12.1", {"start": v(30, 68.5) * mm, "end": v(30, 63.5) * mm});
            skLineSegment(sketch, "E3.5.12.2", {"start": v(30, 63.5) * mm, "end": v(25, 63.5) * mm});
            skLineSegment(sketch, "E3.5.12.3", {"start": v(25, 68.5) * mm, "end": v(25, 63.5) * mm});
            skPoint(sketch, "E3.5.12.4", {"position": v(27.5, 66) * mm});
            skLineSegment(sketch, "E3.5.13.0", {"start": v(30, 74) * mm, "end": v(25, 74) * mm});
            skLineSegment(sketch, "E3.5.13.1", {"start": v(30, 74) * mm, "end": v(30, 69) * mm});
            skLineSegment(sketch, "E3.5.13.2", {"start": v(30, 69) * mm, "end": v(25, 69) * mm});
            skLineSegment(sketch, "E3.5.13.3", {"start": v(25, 74) * mm, "end": v(25, 69) * mm});
            skPoint(sketch, "E3.5.13.4", {"position": v(27.5, 71.5) * mm});
            skLineSegment(sketch, "E3.5.14.0", {"start": v(30, 79.5) * mm, "end": v(25, 79.5) * mm});
            skLineSegment(sketch, "E3.5.14.1", {"start": v(30, 79.5) * mm, "end": v(30, 74.5) * mm});
            skLineSegment(sketch, "E3.5.14.2", {"start": v(30, 74.5) * mm, "end": v(25, 74.5) * mm});
            skLineSegment(sketch, "E3.5.14.3", {"start": v(25, 79.5) * mm, "end": v(25, 74.5) * mm});
            skPoint(sketch, "E3.5.14.4", {"position": v(27.5, 77) * mm});
            skLineSegment(sketch, "E3.5.15.0", {"start": v(30, 85) * mm, "end": v(25, 85) * mm});
            skLineSegment(sketch, "E3.5.15.1", {"start": v(30, 85) * mm, "end": v(30, 80) * mm});
            skLineSegment(sketch, "E3.5.15.2", {"start": v(30, 80) * mm, "end": v(25, 80) * mm});
            skLineSegment(sketch, "E3.5.15.3", {"start": v(25, 85) * mm, "end": v(25, 80) * mm});
            skPoint(sketch, "E3.5.15.4", {"position": v(27.5, 82.5) * mm});
            skLineSegment(sketch, "E3.5.16.0", {"start": v(30, 90.5) * mm, "end": v(25, 90.5) * mm});
            skLineSegment(sketch, "E3.5.16.1", {"start": v(30, 90.5) * mm, "end": v(30, 85.5) * mm});
            skLineSegment(sketch, "E3.5.16.2", {"start": v(30, 85.5) * mm, "end": v(25, 85.5) * mm});
            skLineSegment(sketch, "E3.5.16.3", {"start": v(25, 90.5) * mm, "end": v(25, 85.5) * mm});
            skPoint(sketch, "E3.5.16.4", {"position": v(27.5, 88) * mm});
            skLineSegment(sketch, "E3.5.17.0", {"start": v(30, 96) * mm, "end": v(25, 96) * mm});
            skLineSegment(sketch, "E3.5.17.1", {"start": v(30, 96) * mm, "end": v(30, 91) * mm});
            skLineSegment(sketch, "E3.5.17.2", {"start": v(30, 91) * mm, "end": v(25, 91) * mm});
            skLineSegment(sketch, "E3.5.17.3", {"start": v(25, 96) * mm, "end": v(25, 91) * mm});
            skPoint(sketch, "E3.5.17.4", {"position": v(27.5, 93.5) * mm});
            skLineSegment(sketch, "E3.5.18.0", {"start": v(30, 101.5) * mm, "end": v(25, 101.5) * mm});
            skLineSegment(sketch, "E3.5.18.1", {"start": v(30, 101.5) * mm, "end": v(30, 96.5) * mm});
            skLineSegment(sketch, "E3.5.18.2", {"start": v(30, 96.5) * mm, "end": v(25, 96.5) * mm});
            skLineSegment(sketch, "E3.5.18.3", {"start": v(25, 101.5) * mm, "end": v(25, 96.5) * mm});
            skPoint(sketch, "E3.5.18.4", {"position": v(27.5, 99) * mm});
            skLineSegment(sketch, "E3.5.19.0", {"start": v(30, 107) * mm, "end": v(25, 107) * mm});
            skLineSegment(sketch, "E3.5.19.1", {"start": v(30, 107) * mm, "end": v(30, 102) * mm});
            skLineSegment(sketch, "E3.5.19.2", {"start": v(30, 102) * mm, "end": v(25, 102) * mm});
            skLineSegment(sketch, "E3.5.19.3", {"start": v(25, 107) * mm, "end": v(25, 102) * mm});
            skPoint(sketch, "E3.5.19.4", {"position": v(27.5, 104.5) * mm});
            skLineSegment(sketch, "E3.5.20.0", {"start": v(30, 112.5) * mm, "end": v(25, 112.5) * mm});
            skLineSegment(sketch, "E3.5.20.1", {"start": v(30, 112.5) * mm, "end": v(30, 107.5) * mm});
            skLineSegment(sketch, "E3.5.20.2", {"start": v(30, 107.5) * mm, "end": v(25, 107.5) * mm});
            skLineSegment(sketch, "E3.5.20.3", {"start": v(25, 112.5) * mm, "end": v(25, 107.5) * mm});
            skPoint(sketch, "E3.5.20.4", {"position": v(27.5, 110) * mm});
            skLineSegment(sketch, "E3.5.21.0", {"start": v(30, 118) * mm, "end": v(25, 118) * mm});
            skLineSegment(sketch, "E3.5.21.1", {"start": v(30, 118) * mm, "end": v(30, 113) * mm});
            skLineSegment(sketch, "E3.5.21.2", {"start": v(30, 113) * mm, "end": v(25, 113) * mm});
            skLineSegment(sketch, "E3.5.21.3", {"start": v(25, 118) * mm, "end": v(25, 113) * mm});
            skPoint(sketch, "E3.5.21.4", {"position": v(27.5, 115.5) * mm});
            skLineSegment(sketch, "E3.5.22.0", {"start": v(30, 123.5) * mm, "end": v(25, 123.5) * mm});
            skLineSegment(sketch, "E3.5.22.1", {"start": v(30, 123.5) * mm, "end": v(30, 118.5) * mm});
            skLineSegment(sketch, "E3.5.22.2", {"start": v(30, 118.5) * mm, "end": v(25, 118.5) * mm});
            skLineSegment(sketch, "E3.5.22.3", {"start": v(25, 123.5) * mm, "end": v(25, 118.5) * mm});
            skPoint(sketch, "E3.5.22.4", {"position": v(27.5, 121) * mm});
            skLineSegment(sketch, "E3.5.23.0", {"start": v(30, 129) * mm, "end": v(25, 129) * mm});
            skLineSegment(sketch, "E3.5.23.1", {"start": v(30, 129) * mm, "end": v(30, 124) * mm});
            skLineSegment(sketch, "E3.5.23.2", {"start": v(30, 124) * mm, "end": v(25, 124) * mm});
            skLineSegment(sketch, "E3.5.23.3", {"start": v(25, 129) * mm, "end": v(25, 124) * mm});
            skPoint(sketch, "E3.5.23.4", {"position": v(27.5, 126.5) * mm});
            skLineSegment(sketch, "E3.5.24.0", {"start": v(30, 134.5) * mm, "end": v(25, 134.5) * mm});
            skLineSegment(sketch, "E3.5.24.1", {"start": v(30, 134.5) * mm, "end": v(30, 129.5) * mm});
            skLineSegment(sketch, "E3.5.24.2", {"start": v(30, 129.5) * mm, "end": v(25, 129.5) * mm});
            skLineSegment(sketch, "E3.5.24.3", {"start": v(25, 134.5) * mm, "end": v(25, 129.5) * mm});
            skPoint(sketch, "E3.5.24.4", {"position": v(27.5, 132) * mm});
            skLineSegment(sketch, "E3.6.0.0", {"start": v(35.5, 2.5) * mm, "end": v(30.5, 2.5) * mm});
            skLineSegment(sketch, "E3.6.0.1", {"start": v(35.5, 2.5) * mm, "end": v(35.5, -2.5) * mm});
            skLineSegment(sketch, "E3.6.0.2", {"start": v(35.5, -2.5) * mm, "end": v(30.5, -2.5) * mm});
            skLineSegment(sketch, "E3.6.0.3", {"start": v(30.5, 2.5) * mm, "end": v(30.5, -2.5) * mm});
            skPoint(sketch, "E3.6.0.4", {"position": v(33, 0) * mm});
            skLineSegment(sketch, "E3.6.1.0", {"start": v(35.5, 8) * mm, "end": v(30.5, 8) * mm});
            skLineSegment(sketch, "E3.6.1.1", {"start": v(35.5, 8) * mm, "end": v(35.5, 3) * mm});
            skLineSegment(sketch, "E3.6.1.2", {"start": v(35.5, 3) * mm, "end": v(30.5, 3) * mm});
            skLineSegment(sketch, "E3.6.1.3", {"start": v(30.5, 8) * mm, "end": v(30.5, 3) * mm});
            skPoint(sketch, "E3.6.1.4", {"position": v(33, 5.5) * mm});
            skLineSegment(sketch, "E3.6.2.0", {"start": v(35.5, 13.5) * mm, "end": v(30.5, 13.5) * mm});
            skLineSegment(sketch, "E3.6.2.1", {"start": v(35.5, 13.5) * mm, "end": v(35.5, 8.5) * mm});
            skLineSegment(sketch, "E3.6.2.2", {"start": v(35.5, 8.5) * mm, "end": v(30.5, 8.5) * mm});
            skLineSegment(sketch, "E3.6.2.3", {"start": v(30.5, 13.5) * mm, "end": v(30.5, 8.5) * mm});
            skPoint(sketch, "E3.6.2.4", {"position": v(33, 11) * mm});
            skLineSegment(sketch, "E3.6.3.0", {"start": v(35.5, 19) * mm, "end": v(30.5, 19) * mm});
            skLineSegment(sketch, "E3.6.3.1", {"start": v(35.5, 19) * mm, "end": v(35.5, 14) * mm});
            skLineSegment(sketch, "E3.6.3.2", {"start": v(35.5, 14) * mm, "end": v(30.5, 14) * mm});
            skLineSegment(sketch, "E3.6.3.3", {"start": v(30.5, 19) * mm, "end": v(30.5, 14) * mm});
            skPoint(sketch, "E3.6.3.4", {"position": v(33, 16.5) * mm});
            skLineSegment(sketch, "E3.6.4.0", {"start": v(35.5, 24.5) * mm, "end": v(30.5, 24.5) * mm});
            skLineSegment(sketch, "E3.6.4.1", {"start": v(35.5, 24.5) * mm, "end": v(35.5, 19.5) * mm});
            skLineSegment(sketch, "E3.6.4.2", {"start": v(35.5, 19.5) * mm, "end": v(30.5, 19.5) * mm});
            skLineSegment(sketch, "E3.6.4.3", {"start": v(30.5, 24.5) * mm, "end": v(30.5, 19.5) * mm});
            skPoint(sketch, "E3.6.4.4", {"position": v(33, 22) * mm});
            skLineSegment(sketch, "E3.6.5.0", {"start": v(35.5, 30) * mm, "end": v(30.5, 30) * mm});
            skLineSegment(sketch, "E3.6.5.1", {"start": v(35.5, 30) * mm, "end": v(35.5, 25) * mm});
            skLineSegment(sketch, "E3.6.5.2", {"start": v(35.5, 25) * mm, "end": v(30.5, 25) * mm});
            skLineSegment(sketch, "E3.6.5.3", {"start": v(30.5, 30) * mm, "end": v(30.5, 25) * mm});
            skPoint(sketch, "E3.6.5.4", {"position": v(33, 27.5) * mm});
            skLineSegment(sketch, "E3.6.6.0", {"start": v(35.5, 35.5) * mm, "end": v(30.5, 35.5) * mm});
            skLineSegment(sketch, "E3.6.6.1", {"start": v(35.5, 35.5) * mm, "end": v(35.5, 30.5) * mm});
            skLineSegment(sketch, "E3.6.6.2", {"start": v(35.5, 30.5) * mm, "end": v(30.5, 30.5) * mm});
            skLineSegment(sketch, "E3.6.6.3", {"start": v(30.5, 35.5) * mm, "end": v(30.5, 30.5) * mm});
            skPoint(sketch, "E3.6.6.4", {"position": v(33, 33) * mm});
            skLineSegment(sketch, "E3.6.7.0", {"start": v(35.5, 41) * mm, "end": v(30.5, 41) * mm});
            skLineSegment(sketch, "E3.6.7.1", {"start": v(35.5, 41) * mm, "end": v(35.5, 36) * mm});
            skLineSegment(sketch, "E3.6.7.2", {"start": v(35.5, 36) * mm, "end": v(30.5, 36) * mm});
            skLineSegment(sketch, "E3.6.7.3", {"start": v(30.5, 41) * mm, "end": v(30.5, 36) * mm});
            skPoint(sketch, "E3.6.7.4", {"position": v(33, 38.5) * mm});
            skLineSegment(sketch, "E3.6.8.0", {"start": v(35.5, 46.5) * mm, "end": v(30.5, 46.5) * mm});
            skLineSegment(sketch, "E3.6.8.1", {"start": v(35.5, 46.5) * mm, "end": v(35.5, 41.5) * mm});
            skLineSegment(sketch, "E3.6.8.2", {"start": v(35.5, 41.5) * mm, "end": v(30.5, 41.5) * mm});
            skLineSegment(sketch, "E3.6.8.3", {"start": v(30.5, 46.5) * mm, "end": v(30.5, 41.5) * mm});
            skPoint(sketch, "E3.6.8.4", {"position": v(33, 44) * mm});
            skLineSegment(sketch, "E3.6.9.0", {"start": v(35.5, 52) * mm, "end": v(30.5, 52) * mm});
            skLineSegment(sketch, "E3.6.9.1", {"start": v(35.5, 52) * mm, "end": v(35.5, 47) * mm});
            skLineSegment(sketch, "E3.6.9.2", {"start": v(35.5, 47) * mm, "end": v(30.5, 47) * mm});
            skLineSegment(sketch, "E3.6.9.3", {"start": v(30.5, 52) * mm, "end": v(30.5, 47) * mm});
            skPoint(sketch, "E3.6.9.4", {"position": v(33, 49.5) * mm});
            skLineSegment(sketch, "E3.6.10.0", {"start": v(35.5, 57.5) * mm, "end": v(30.5, 57.5) * mm});
            skLineSegment(sketch, "E3.6.10.1", {"start": v(35.5, 57.5) * mm, "end": v(35.5, 52.5) * mm});
            skLineSegment(sketch, "E3.6.10.2", {"start": v(35.5, 52.5) * mm, "end": v(30.5, 52.5) * mm});
            skLineSegment(sketch, "E3.6.10.3", {"start": v(30.5, 57.5) * mm, "end": v(30.5, 52.5) * mm});
            skPoint(sketch, "E3.6.10.4", {"position": v(33, 55) * mm});
            skLineSegment(sketch, "E3.6.11.0", {"start": v(35.5, 63) * mm, "end": v(30.5, 63) * mm});
            skLineSegment(sketch, "E3.6.11.1", {"start": v(35.5, 63) * mm, "end": v(35.5, 58) * mm});
            skLineSegment(sketch, "E3.6.11.2", {"start": v(35.5, 58) * mm, "end": v(30.5, 58) * mm});
            skLineSegment(sketch, "E3.6.11.3", {"start": v(30.5, 63) * mm, "end": v(30.5, 58) * mm});
            skPoint(sketch, "E3.6.11.4", {"position": v(33, 60.5) * mm});
            skLineSegment(sketch, "E3.6.12.0", {"start": v(35.5, 68.5) * mm, "end": v(30.5, 68.5) * mm});
            skLineSegment(sketch, "E3.6.12.1", {"start": v(35.5, 68.5) * mm, "end": v(35.5, 63.5) * mm});
            skLineSegment(sketch, "E3.6.12.2", {"start": v(35.5, 63.5) * mm, "end": v(30.5, 63.5) * mm});
            skLineSegment(sketch, "E3.6.12.3", {"start": v(30.5, 68.5) * mm, "end": v(30.5, 63.5) * mm});
            skPoint(sketch, "E3.6.12.4", {"position": v(33, 66) * mm});
            skLineSegment(sketch, "E3.6.13.0", {"start": v(35.5, 74) * mm, "end": v(30.5, 74) * mm});
            skLineSegment(sketch, "E3.6.13.1", {"start": v(35.5, 74) * mm, "end": v(35.5, 69) * mm});
            skLineSegment(sketch, "E3.6.13.2", {"start": v(35.5, 69) * mm, "end": v(30.5, 69) * mm});
            skLineSegment(sketch, "E3.6.13.3", {"start": v(30.5, 74) * mm, "end": v(30.5, 69) * mm});
            skPoint(sketch, "E3.6.13.4", {"position": v(33, 71.5) * mm});
            skLineSegment(sketch, "E3.6.14.0", {"start": v(35.5, 79.5) * mm, "end": v(30.5, 79.5) * mm});
            skLineSegment(sketch, "E3.6.14.1", {"start": v(35.5, 79.5) * mm, "end": v(35.5, 74.5) * mm});
            skLineSegment(sketch, "E3.6.14.2", {"start": v(35.5, 74.5) * mm, "end": v(30.5, 74.5) * mm});
            skLineSegment(sketch, "E3.6.14.3", {"start": v(30.5, 79.5) * mm, "end": v(30.5, 74.5) * mm});
            skPoint(sketch, "E3.6.14.4", {"position": v(33, 77) * mm});
            skLineSegment(sketch, "E3.6.15.0", {"start": v(35.5, 85) * mm, "end": v(30.5, 85) * mm});
            skLineSegment(sketch, "E3.6.15.1", {"start": v(35.5, 85) * mm, "end": v(35.5, 80) * mm});
            skLineSegment(sketch, "E3.6.15.2", {"start": v(35.5, 80) * mm, "end": v(30.5, 80) * mm});
            skLineSegment(sketch, "E3.6.15.3", {"start": v(30.5, 85) * mm, "end": v(30.5, 80) * mm});
            skPoint(sketch, "E3.6.15.4", {"position": v(33, 82.5) * mm});
            skLineSegment(sketch, "E3.6.16.0", {"start": v(35.5, 90.5) * mm, "end": v(30.5, 90.5) * mm});
            skLineSegment(sketch, "E3.6.16.1", {"start": v(35.5, 90.5) * mm, "end": v(35.5, 85.5) * mm});
            skLineSegment(sketch, "E3.6.16.2", {"start": v(35.5, 85.5) * mm, "end": v(30.5, 85.5) * mm});
            skLineSegment(sketch, "E3.6.16.3", {"start": v(30.5, 90.5) * mm, "end": v(30.5, 85.5) * mm});
            skPoint(sketch, "E3.6.16.4", {"position": v(33, 88) * mm});
            skLineSegment(sketch, "E3.6.17.0", {"start": v(35.5, 96) * mm, "end": v(30.5, 96) * mm});
            skLineSegment(sketch, "E3.6.17.1", {"start": v(35.5, 96) * mm, "end": v(35.5, 91) * mm});
            skLineSegment(sketch, "E3.6.17.2", {"start": v(35.5, 91) * mm, "end": v(30.5, 91) * mm});
            skLineSegment(sketch, "E3.6.17.3", {"start": v(30.5, 96) * mm, "end": v(30.5, 91) * mm});
            skPoint(sketch, "E3.6.17.4", {"position": v(33, 93.5) * mm});
            skLineSegment(sketch, "E3.6.18.0", {"start": v(35.5, 101.5) * mm, "end": v(30.5, 101.5) * mm});
            skLineSegment(sketch, "E3.6.18.1", {"start": v(35.5, 101.5) * mm, "end": v(35.5, 96.5) * mm});
            skLineSegment(sketch, "E3.6.18.2", {"start": v(35.5, 96.5) * mm, "end": v(30.5, 96.5) * mm});
            skLineSegment(sketch, "E3.6.18.3", {"start": v(30.5, 101.5) * mm, "end": v(30.5, 96.5) * mm});
            skPoint(sketch, "E3.6.18.4", {"position": v(33, 99) * mm});
            skLineSegment(sketch, "E3.6.19.0", {"start": v(35.5, 107) * mm, "end": v(30.5, 107) * mm});
            skLineSegment(sketch, "E3.6.19.1", {"start": v(35.5, 107) * mm, "end": v(35.5, 102) * mm});
            skLineSegment(sketch, "E3.6.19.2", {"start": v(35.5, 102) * mm, "end": v(30.5, 102) * mm});
            skLineSegment(sketch, "E3.6.19.3", {"start": v(30.5, 107) * mm, "end": v(30.5, 102) * mm});
            skPoint(sketch, "E3.6.19.4", {"position": v(33, 104.5) * mm});
            skLineSegment(sketch, "E3.6.20.0", {"start": v(35.5, 112.5) * mm, "end": v(30.5, 112.5) * mm});
            skLineSegment(sketch, "E3.6.20.1", {"start": v(35.5, 112.5) * mm, "end": v(35.5, 107.5) * mm});
            skLineSegment(sketch, "E3.6.20.2", {"start": v(35.5, 107.5) * mm, "end": v(30.5, 107.5) * mm});
            skLineSegment(sketch, "E3.6.20.3", {"start": v(30.5, 112.5) * mm, "end": v(30.5, 107.5) * mm});
            skPoint(sketch, "E3.6.20.4", {"position": v(33, 110) * mm});
            skLineSegment(sketch, "E3.6.21.0", {"start": v(35.5, 118) * mm, "end": v(30.5, 118) * mm});
            skLineSegment(sketch, "E3.6.21.1", {"start": v(35.5, 118) * mm, "end": v(35.5, 113) * mm});
            skLineSegment(sketch, "E3.6.21.2", {"start": v(35.5, 113) * mm, "end": v(30.5, 113) * mm});
            skLineSegment(sketch, "E3.6.21.3", {"start": v(30.5, 118) * mm, "end": v(30.5, 113) * mm});
            skPoint(sketch, "E3.6.21.4", {"position": v(33, 115.5) * mm});
            skLineSegment(sketch, "E3.6.22.0", {"start": v(35.5, 123.5) * mm, "end": v(30.5, 123.5) * mm});
            skLineSegment(sketch, "E3.6.22.1", {"start": v(35.5, 123.5) * mm, "end": v(35.5, 118.5) * mm});
            skLineSegment(sketch, "E3.6.22.2", {"start": v(35.5, 118.5) * mm, "end": v(30.5, 118.5) * mm});
            skLineSegment(sketch, "E3.6.22.3", {"start": v(30.5, 123.5) * mm, "end": v(30.5, 118.5) * mm});
            skPoint(sketch, "E3.6.22.4", {"position": v(33, 121) * mm});
            skLineSegment(sketch, "E3.6.23.0", {"start": v(35.5, 129) * mm, "end": v(30.5, 129) * mm});
            skLineSegment(sketch, "E3.6.23.1", {"start": v(35.5, 129) * mm, "end": v(35.5, 124) * mm});
            skLineSegment(sketch, "E3.6.23.2", {"start": v(35.5, 124) * mm, "end": v(30.5, 124) * mm});
            skLineSegment(sketch, "E3.6.23.3", {"start": v(30.5, 129) * mm, "end": v(30.5, 124) * mm});
            skPoint(sketch, "E3.6.23.4", {"position": v(33, 126.5) * mm});
            skLineSegment(sketch, "E3.6.24.0", {"start": v(35.5, 134.5) * mm, "end": v(30.5, 134.5) * mm});
            skLineSegment(sketch, "E3.6.24.1", {"start": v(35.5, 134.5) * mm, "end": v(35.5, 129.5) * mm});
            skLineSegment(sketch, "E3.6.24.2", {"start": v(35.5, 129.5) * mm, "end": v(30.5, 129.5) * mm});
            skLineSegment(sketch, "E3.6.24.3", {"start": v(30.5, 134.5) * mm, "end": v(30.5, 129.5) * mm});
            skPoint(sketch, "E3.6.24.4", {"position": v(33, 132) * mm});
            skLineSegment(sketch, "E3.7.0.0", {"start": v(41, 2.5) * mm, "end": v(36, 2.5) * mm});
            skLineSegment(sketch, "E3.7.0.1", {"start": v(41, 2.5) * mm, "end": v(41, -2.5) * mm});
            skLineSegment(sketch, "E3.7.0.2", {"start": v(41, -2.5) * mm, "end": v(36, -2.5) * mm});
            skLineSegment(sketch, "E3.7.0.3", {"start": v(36, 2.5) * mm, "end": v(36, -2.5) * mm});
            skPoint(sketch, "E3.7.0.4", {"position": v(38.5, 0) * mm});
            skLineSegment(sketch, "E3.7.1.0", {"start": v(41, 8) * mm, "end": v(36, 8) * mm});
            skLineSegment(sketch, "E3.7.1.1", {"start": v(41, 8) * mm, "end": v(41, 3) * mm});
            skLineSegment(sketch, "E3.7.1.2", {"start": v(41, 3) * mm, "end": v(36, 3) * mm});
            skLineSegment(sketch, "E3.7.1.3", {"start": v(36, 8) * mm, "end": v(36, 3) * mm});
            skPoint(sketch, "E3.7.1.4", {"position": v(38.5, 5.5) * mm});
            skLineSegment(sketch, "E3.7.2.0", {"start": v(41, 13.5) * mm, "end": v(36, 13.5) * mm});
            skLineSegment(sketch, "E3.7.2.1", {"start": v(41, 13.5) * mm, "end": v(41, 8.5) * mm});
            skLineSegment(sketch, "E3.7.2.2", {"start": v(41, 8.5) * mm, "end": v(36, 8.5) * mm});
            skLineSegment(sketch, "E3.7.2.3", {"start": v(36, 13.5) * mm, "end": v(36, 8.5) * mm});
            skPoint(sketch, "E3.7.2.4", {"position": v(38.5, 11) * mm});
            skLineSegment(sketch, "E3.7.3.0", {"start": v(41, 19) * mm, "end": v(36, 19) * mm});
            skLineSegment(sketch, "E3.7.3.1", {"start": v(41, 19) * mm, "end": v(41, 14) * mm});
            skLineSegment(sketch, "E3.7.3.2", {"start": v(41, 14) * mm, "end": v(36, 14) * mm});
            skLineSegment(sketch, "E3.7.3.3", {"start": v(36, 19) * mm, "end": v(36, 14) * mm});
            skPoint(sketch, "E3.7.3.4", {"position": v(38.5, 16.5) * mm});
            skLineSegment(sketch, "E3.7.4.0", {"start": v(41, 24.5) * mm, "end": v(36, 24.5) * mm});
            skLineSegment(sketch, "E3.7.4.1", {"start": v(41, 24.5) * mm, "end": v(41, 19.5) * mm});
            skLineSegment(sketch, "E3.7.4.2", {"start": v(41, 19.5) * mm, "end": v(36, 19.5) * mm});
            skLineSegment(sketch, "E3.7.4.3", {"start": v(36, 24.5) * mm, "end": v(36, 19.5) * mm});
            skPoint(sketch, "E3.7.4.4", {"position": v(38.5, 22) * mm});
            skLineSegment(sketch, "E3.7.5.0", {"start": v(41, 30) * mm, "end": v(36, 30) * mm});
            skLineSegment(sketch, "E3.7.5.1", {"start": v(41, 30) * mm, "end": v(41, 25) * mm});
            skLineSegment(sketch, "E3.7.5.2", {"start": v(41, 25) * mm, "end": v(36, 25) * mm});
            skLineSegment(sketch, "E3.7.5.3", {"start": v(36, 30) * mm, "end": v(36, 25) * mm});
            skPoint(sketch, "E3.7.5.4", {"position": v(38.5, 27.5) * mm});
            skLineSegment(sketch, "E3.7.6.0", {"start": v(41, 35.5) * mm, "end": v(36, 35.5) * mm});
            skLineSegment(sketch, "E3.7.6.1", {"start": v(41, 35.5) * mm, "end": v(41, 30.5) * mm});
            skLineSegment(sketch, "E3.7.6.2", {"start": v(41, 30.5) * mm, "end": v(36, 30.5) * mm});
            skLineSegment(sketch, "E3.7.6.3", {"start": v(36, 35.5) * mm, "end": v(36, 30.5) * mm});
            skPoint(sketch, "E3.7.6.4", {"position": v(38.5, 33) * mm});
            skLineSegment(sketch, "E3.7.7.0", {"start": v(41, 41) * mm, "end": v(36, 41) * mm});
            skLineSegment(sketch, "E3.7.7.1", {"start": v(41, 41) * mm, "end": v(41, 36) * mm});
            skLineSegment(sketch, "E3.7.7.2", {"start": v(41, 36) * mm, "end": v(36, 36) * mm});
            skLineSegment(sketch, "E3.7.7.3", {"start": v(36, 41) * mm, "end": v(36, 36) * mm});
            skPoint(sketch, "E3.7.7.4", {"position": v(38.5, 38.5) * mm});
            skLineSegment(sketch, "E3.7.8.0", {"start": v(41, 46.5) * mm, "end": v(36, 46.5) * mm});
            skLineSegment(sketch, "E3.7.8.1", {"start": v(41, 46.5) * mm, "end": v(41, 41.5) * mm});
            skLineSegment(sketch, "E3.7.8.2", {"start": v(41, 41.5) * mm, "end": v(36, 41.5) * mm});
            skLineSegment(sketch, "E3.7.8.3", {"start": v(36, 46.5) * mm, "end": v(36, 41.5) * mm});
            skPoint(sketch, "E3.7.8.4", {"position": v(38.5, 44) * mm});
            skLineSegment(sketch, "E3.7.9.0", {"start": v(41, 52) * mm, "end": v(36, 52) * mm});
            skLineSegment(sketch, "E3.7.9.1", {"start": v(41, 52) * mm, "end": v(41, 47) * mm});
            skLineSegment(sketch, "E3.7.9.2", {"start": v(41, 47) * mm, "end": v(36, 47) * mm});
            skLineSegment(sketch, "E3.7.9.3", {"start": v(36, 52) * mm, "end": v(36, 47) * mm});
            skPoint(sketch, "E3.7.9.4", {"position": v(38.5, 49.5) * mm});
            skLineSegment(sketch, "E3.7.10.0", {"start": v(41, 57.5) * mm, "end": v(36, 57.5) * mm});
            skLineSegment(sketch, "E3.7.10.1", {"start": v(41, 57.5) * mm, "end": v(41, 52.5) * mm});
            skLineSegment(sketch, "E3.7.10.2", {"start": v(41, 52.5) * mm, "end": v(36, 52.5) * mm});
            skLineSegment(sketch, "E3.7.10.3", {"start": v(36, 57.5) * mm, "end": v(36, 52.5) * mm});
            skPoint(sketch, "E3.7.10.4", {"position": v(38.5, 55) * mm});
            skLineSegment(sketch, "E3.7.11.0", {"start": v(41, 63) * mm, "end": v(36, 63) * mm});
            skLineSegment(sketch, "E3.7.11.1", {"start": v(41, 63) * mm, "end": v(41, 58) * mm});
            skLineSegment(sketch, "E3.7.11.2", {"start": v(41, 58) * mm, "end": v(36, 58) * mm});
            skLineSegment(sketch, "E3.7.11.3", {"start": v(36, 63) * mm, "end": v(36, 58) * mm});
            skPoint(sketch, "E3.7.11.4", {"position": v(38.5, 60.5) * mm});
            skLineSegment(sketch, "E3.7.12.0", {"start": v(41, 68.5) * mm, "end": v(36, 68.5) * mm});
            skLineSegment(sketch, "E3.7.12.1", {"start": v(41, 68.5) * mm, "end": v(41, 63.5) * mm});
            skLineSegment(sketch, "E3.7.12.2", {"start": v(41, 63.5) * mm, "end": v(36, 63.5) * mm});
            skLineSegment(sketch, "E3.7.12.3", {"start": v(36, 68.5) * mm, "end": v(36, 63.5) * mm});
            skPoint(sketch, "E3.7.12.4", {"position": v(38.5, 66) * mm});
            skLineSegment(sketch, "E3.7.13.0", {"start": v(41, 74) * mm, "end": v(36, 74) * mm});
            skLineSegment(sketch, "E3.7.13.1", {"start": v(41, 74) * mm, "end": v(41, 69) * mm});
            skLineSegment(sketch, "E3.7.13.2", {"start": v(41, 69) * mm, "end": v(36, 69) * mm});
            skLineSegment(sketch, "E3.7.13.3", {"start": v(36, 74) * mm, "end": v(36, 69) * mm});
            skPoint(sketch, "E3.7.13.4", {"position": v(38.5, 71.5) * mm});
            skLineSegment(sketch, "E3.7.14.0", {"start": v(41, 79.5) * mm, "end": v(36, 79.5) * mm});
            skLineSegment(sketch, "E3.7.14.1", {"start": v(41, 79.5) * mm, "end": v(41, 74.5) * mm});
            skLineSegment(sketch, "E3.7.14.2", {"start": v(41, 74.5) * mm, "end": v(36, 74.5) * mm});
            skLineSegment(sketch, "E3.7.14.3", {"start": v(36, 79.5) * mm, "end": v(36, 74.5) * mm});
            skPoint(sketch, "E3.7.14.4", {"position": v(38.5, 77) * mm});
            skLineSegment(sketch, "E3.7.15.0", {"start": v(41, 85) * mm, "end": v(36, 85) * mm});
            skLineSegment(sketch, "E3.7.15.1", {"start": v(41, 85) * mm, "end": v(41, 80) * mm});
            skLineSegment(sketch, "E3.7.15.2", {"start": v(41, 80) * mm, "end": v(36, 80) * mm});
            skLineSegment(sketch, "E3.7.15.3", {"start": v(36, 85) * mm, "end": v(36, 80) * mm});
            skPoint(sketch, "E3.7.15.4", {"position": v(38.5, 82.5) * mm});
            skLineSegment(sketch, "E3.7.16.0", {"start": v(41, 90.5) * mm, "end": v(36, 90.5) * mm});
            skLineSegment(sketch, "E3.7.16.1", {"start": v(41, 90.5) * mm, "end": v(41, 85.5) * mm});
            skLineSegment(sketch, "E3.7.16.2", {"start": v(41, 85.5) * mm, "end": v(36, 85.5) * mm});
            skLineSegment(sketch, "E3.7.16.3", {"start": v(36, 90.5) * mm, "end": v(36, 85.5) * mm});
            skPoint(sketch, "E3.7.16.4", {"position": v(38.5, 88) * mm});
            skLineSegment(sketch, "E3.7.17.0", {"start": v(41, 96) * mm, "end": v(36, 96) * mm});
            skLineSegment(sketch, "E3.7.17.1", {"start": v(41, 96) * mm, "end": v(41, 91) * mm});
            skLineSegment(sketch, "E3.7.17.2", {"start": v(41, 91) * mm, "end": v(36, 91) * mm});
            skLineSegment(sketch, "E3.7.17.3", {"start": v(36, 96) * mm, "end": v(36, 91) * mm});
            skPoint(sketch, "E3.7.17.4", {"position": v(38.5, 93.5) * mm});
            skLineSegment(sketch, "E3.7.18.0", {"start": v(41, 101.5) * mm, "end": v(36, 101.5) * mm});
            skLineSegment(sketch, "E3.7.18.1", {"start": v(41, 101.5) * mm, "end": v(41, 96.5) * mm});
            skLineSegment(sketch, "E3.7.18.2", {"start": v(41, 96.5) * mm, "end": v(36, 96.5) * mm});
            skLineSegment(sketch, "E3.7.18.3", {"start": v(36, 101.5) * mm, "end": v(36, 96.5) * mm});
            skPoint(sketch, "E3.7.18.4", {"position": v(38.5, 99) * mm});
            skLineSegment(sketch, "E3.7.19.0", {"start": v(41, 107) * mm, "end": v(36, 107) * mm});
            skLineSegment(sketch, "E3.7.19.1", {"start": v(41, 107) * mm, "end": v(41, 102) * mm});
            skLineSegment(sketch, "E3.7.19.2", {"start": v(41, 102) * mm, "end": v(36, 102) * mm});
            skLineSegment(sketch, "E3.7.19.3", {"start": v(36, 107) * mm, "end": v(36, 102) * mm});
            skPoint(sketch, "E3.7.19.4", {"position": v(38.5, 104.5) * mm});
            skLineSegment(sketch, "E3.7.20.0", {"start": v(41, 112.5) * mm, "end": v(36, 112.5) * mm});
            skLineSegment(sketch, "E3.7.20.1", {"start": v(41, 112.5) * mm, "end": v(41, 107.5) * mm});
            skLineSegment(sketch, "E3.7.20.2", {"start": v(41, 107.5) * mm, "end": v(36, 107.5) * mm});
            skLineSegment(sketch, "E3.7.20.3", {"start": v(36, 112.5) * mm, "end": v(36, 107.5) * mm});
            skPoint(sketch, "E3.7.20.4", {"position": v(38.5, 110) * mm});
            skLineSegment(sketch, "E3.7.21.0", {"start": v(41, 118) * mm, "end": v(36, 118) * mm});
            skLineSegment(sketch, "E3.7.21.1", {"start": v(41, 118) * mm, "end": v(41, 113) * mm});
            skLineSegment(sketch, "E3.7.21.2", {"start": v(41, 113) * mm, "end": v(36, 113) * mm});
            skLineSegment(sketch, "E3.7.21.3", {"start": v(36, 118) * mm, "end": v(36, 113) * mm});
            skPoint(sketch, "E3.7.21.4", {"position": v(38.5, 115.5) * mm});
            skLineSegment(sketch, "E3.7.22.0", {"start": v(41, 123.5) * mm, "end": v(36, 123.5) * mm});
            skLineSegment(sketch, "E3.7.22.1", {"start": v(41, 123.5) * mm, "end": v(41, 118.5) * mm});
            skLineSegment(sketch, "E3.7.22.2", {"start": v(41, 118.5) * mm, "end": v(36, 118.5) * mm});
            skLineSegment(sketch, "E3.7.22.3", {"start": v(36, 123.5) * mm, "end": v(36, 118.5) * mm});
            skPoint(sketch, "E3.7.22.4", {"position": v(38.5, 121) * mm});
            skLineSegment(sketch, "E3.7.23.0", {"start": v(41, 129) * mm, "end": v(36, 129) * mm});
            skLineSegment(sketch, "E3.7.23.1", {"start": v(41, 129) * mm, "end": v(41, 124) * mm});
            skLineSegment(sketch, "E3.7.23.2", {"start": v(41, 124) * mm, "end": v(36, 124) * mm});
            skLineSegment(sketch, "E3.7.23.3", {"start": v(36, 129) * mm, "end": v(36, 124) * mm});
            skPoint(sketch, "E3.7.23.4", {"position": v(38.5, 126.5) * mm});
            skLineSegment(sketch, "E3.7.24.0", {"start": v(41, 134.5) * mm, "end": v(36, 134.5) * mm});
            skLineSegment(sketch, "E3.7.24.1", {"start": v(41, 134.5) * mm, "end": v(41, 129.5) * mm});
            skLineSegment(sketch, "E3.7.24.2", {"start": v(41, 129.5) * mm, "end": v(36, 129.5) * mm});
            skLineSegment(sketch, "E3.7.24.3", {"start": v(36, 134.5) * mm, "end": v(36, 129.5) * mm});
            skPoint(sketch, "E3.7.24.4", {"position": v(38.5, 132) * mm});
            skLineSegment(sketch, "E3.8.0.0", {"start": v(46.5, 2.5) * mm, "end": v(41.5, 2.5) * mm});
            skLineSegment(sketch, "E3.8.0.1", {"start": v(46.5, 2.5) * mm, "end": v(46.5, -2.5) * mm});
            skLineSegment(sketch, "E3.8.0.2", {"start": v(46.5, -2.5) * mm, "end": v(41.5, -2.5) * mm});
            skLineSegment(sketch, "E3.8.0.3", {"start": v(41.5, 2.5) * mm, "end": v(41.5, -2.5) * mm});
            skPoint(sketch, "E3.8.0.4", {"position": v(44, 0) * mm});
            skLineSegment(sketch, "E3.8.1.0", {"start": v(46.5, 8) * mm, "end": v(41.5, 8) * mm});
            skLineSegment(sketch, "E3.8.1.1", {"start": v(46.5, 8) * mm, "end": v(46.5, 3) * mm});
            skLineSegment(sketch, "E3.8.1.2", {"start": v(46.5, 3) * mm, "end": v(41.5, 3) * mm});
            skLineSegment(sketch, "E3.8.1.3", {"start": v(41.5, 8) * mm, "end": v(41.5, 3) * mm});
            skPoint(sketch, "E3.8.1.4", {"position": v(44, 5.5) * mm});
            skLineSegment(sketch, "E3.8.2.0", {"start": v(46.5, 13.5) * mm, "end": v(41.5, 13.5) * mm});
            skLineSegment(sketch, "E3.8.2.1", {"start": v(46.5, 13.5) * mm, "end": v(46.5, 8.5) * mm});
            skLineSegment(sketch, "E3.8.2.2", {"start": v(46.5, 8.5) * mm, "end": v(41.5, 8.5) * mm});
            skLineSegment(sketch, "E3.8.2.3", {"start": v(41.5, 13.5) * mm, "end": v(41.5, 8.5) * mm});
            skPoint(sketch, "E3.8.2.4", {"position": v(44, 11) * mm});
            skLineSegment(sketch, "E3.8.3.0", {"start": v(46.5, 19) * mm, "end": v(41.5, 19) * mm});
            skLineSegment(sketch, "E3.8.3.1", {"start": v(46.5, 19) * mm, "end": v(46.5, 14) * mm});
            skLineSegment(sketch, "E3.8.3.2", {"start": v(46.5, 14) * mm, "end": v(41.5, 14) * mm});
            skLineSegment(sketch, "E3.8.3.3", {"start": v(41.5, 19) * mm, "end": v(41.5, 14) * mm});
            skPoint(sketch, "E3.8.3.4", {"position": v(44, 16.5) * mm});
            skLineSegment(sketch, "E3.8.4.0", {"start": v(46.5, 24.5) * mm, "end": v(41.5, 24.5) * mm});
            skLineSegment(sketch, "E3.8.4.1", {"start": v(46.5, 24.5) * mm, "end": v(46.5, 19.5) * mm});
            skLineSegment(sketch, "E3.8.4.2", {"start": v(46.5, 19.5) * mm, "end": v(41.5, 19.5) * mm});
            skLineSegment(sketch, "E3.8.4.3", {"start": v(41.5, 24.5) * mm, "end": v(41.5, 19.5) * mm});
            skPoint(sketch, "E3.8.4.4", {"position": v(44, 22) * mm});
            skLineSegment(sketch, "E3.8.5.0", {"start": v(46.5, 30) * mm, "end": v(41.5, 30) * mm});
            skLineSegment(sketch, "E3.8.5.1", {"start": v(46.5, 30) * mm, "end": v(46.5, 25) * mm});
            skLineSegment(sketch, "E3.8.5.2", {"start": v(46.5, 25) * mm, "end": v(41.5, 25) * mm});
            skLineSegment(sketch, "E3.8.5.3", {"start": v(41.5, 30) * mm, "end": v(41.5, 25) * mm});
            skPoint(sketch, "E3.8.5.4", {"position": v(44, 27.5) * mm});
            skLineSegment(sketch, "E3.8.6.0", {"start": v(46.5, 35.5) * mm, "end": v(41.5, 35.5) * mm});
            skLineSegment(sketch, "E3.8.6.1", {"start": v(46.5, 35.5) * mm, "end": v(46.5, 30.5) * mm});
            skLineSegment(sketch, "E3.8.6.2", {"start": v(46.5, 30.5) * mm, "end": v(41.5, 30.5) * mm});
            skLineSegment(sketch, "E3.8.6.3", {"start": v(41.5, 35.5) * mm, "end": v(41.5, 30.5) * mm});
            skPoint(sketch, "E3.8.6.4", {"position": v(44, 33) * mm});
            skLineSegment(sketch, "E3.8.7.0", {"start": v(46.5, 41) * mm, "end": v(41.5, 41) * mm});
            skLineSegment(sketch, "E3.8.7.1", {"start": v(46.5, 41) * mm, "end": v(46.5, 36) * mm});
            skLineSegment(sketch, "E3.8.7.2", {"start": v(46.5, 36) * mm, "end": v(41.5, 36) * mm});
            skLineSegment(sketch, "E3.8.7.3", {"start": v(41.5, 41) * mm, "end": v(41.5, 36) * mm});
            skPoint(sketch, "E3.8.7.4", {"position": v(44, 38.5) * mm});
            skLineSegment(sketch, "E3.8.8.0", {"start": v(46.5, 46.5) * mm, "end": v(41.5, 46.5) * mm});
            skLineSegment(sketch, "E3.8.8.1", {"start": v(46.5, 46.5) * mm, "end": v(46.5, 41.5) * mm});
            skLineSegment(sketch, "E3.8.8.2", {"start": v(46.5, 41.5) * mm, "end": v(41.5, 41.5) * mm});
            skLineSegment(sketch, "E3.8.8.3", {"start": v(41.5, 46.5) * mm, "end": v(41.5, 41.5) * mm});
            skPoint(sketch, "E3.8.8.4", {"position": v(44, 44) * mm});
            skLineSegment(sketch, "E3.8.9.0", {"start": v(46.5, 52) * mm, "end": v(41.5, 52) * mm});
            skLineSegment(sketch, "E3.8.9.1", {"start": v(46.5, 52) * mm, "end": v(46.5, 47) * mm});
            skLineSegment(sketch, "E3.8.9.2", {"start": v(46.5, 47) * mm, "end": v(41.5, 47) * mm});
            skLineSegment(sketch, "E3.8.9.3", {"start": v(41.5, 52) * mm, "end": v(41.5, 47) * mm});
            skPoint(sketch, "E3.8.9.4", {"position": v(44, 49.5) * mm});
            skLineSegment(sketch, "E3.8.10.0", {"start": v(46.5, 57.5) * mm, "end": v(41.5, 57.5) * mm});
            skLineSegment(sketch, "E3.8.10.1", {"start": v(46.5, 57.5) * mm, "end": v(46.5, 52.5) * mm});
            skLineSegment(sketch, "E3.8.10.2", {"start": v(46.5, 52.5) * mm, "end": v(41.5, 52.5) * mm});
            skLineSegment(sketch, "E3.8.10.3", {"start": v(41.5, 57.5) * mm, "end": v(41.5, 52.5) * mm});
            skPoint(sketch, "E3.8.10.4", {"position": v(44, 55) * mm});
            skLineSegment(sketch, "E3.8.11.0", {"start": v(46.5, 63) * mm, "end": v(41.5, 63) * mm});
            skLineSegment(sketch, "E3.8.11.1", {"start": v(46.5, 63) * mm, "end": v(46.5, 58) * mm});
            skLineSegment(sketch, "E3.8.11.2", {"start": v(46.5, 58) * mm, "end": v(41.5, 58) * mm});
            skLineSegment(sketch, "E3.8.11.3", {"start": v(41.5, 63) * mm, "end": v(41.5, 58) * mm});
            skPoint(sketch, "E3.8.11.4", {"position": v(44, 60.5) * mm});
            skLineSegment(sketch, "E3.8.12.0", {"start": v(46.5, 68.5) * mm, "end": v(41.5, 68.5) * mm});
            skLineSegment(sketch, "E3.8.12.1", {"start": v(46.5, 68.5) * mm, "end": v(46.5, 63.5) * mm});
            skLineSegment(sketch, "E3.8.12.2", {"start": v(46.5, 63.5) * mm, "end": v(41.5, 63.5) * mm});
            skLineSegment(sketch, "E3.8.12.3", {"start": v(41.5, 68.5) * mm, "end": v(41.5, 63.5) * mm});
            skPoint(sketch, "E3.8.12.4", {"position": v(44, 66) * mm});
            skLineSegment(sketch, "E3.8.13.0", {"start": v(46.5, 74) * mm, "end": v(41.5, 74) * mm});
            skLineSegment(sketch, "E3.8.13.1", {"start": v(46.5, 74) * mm, "end": v(46.5, 69) * mm});
            skLineSegment(sketch, "E3.8.13.2", {"start": v(46.5, 69) * mm, "end": v(41.5, 69) * mm});
            skLineSegment(sketch, "E3.8.13.3", {"start": v(41.5, 74) * mm, "end": v(41.5, 69) * mm});
            skPoint(sketch, "E3.8.13.4", {"position": v(44, 71.5) * mm});
            skLineSegment(sketch, "E3.8.14.0", {"start": v(46.5, 79.5) * mm, "end": v(41.5, 79.5) * mm});
            skLineSegment(sketch, "E3.8.14.1", {"start": v(46.5, 79.5) * mm, "end": v(46.5, 74.5) * mm});
            skLineSegment(sketch, "E3.8.14.2", {"start": v(46.5, 74.5) * mm, "end": v(41.5, 74.5) * mm});
            skLineSegment(sketch, "E3.8.14.3", {"start": v(41.5, 79.5) * mm, "end": v(41.5, 74.5) * mm});
            skPoint(sketch, "E3.8.14.4", {"position": v(44, 77) * mm});
            skLineSegment(sketch, "E3.8.15.0", {"start": v(46.5, 85) * mm, "end": v(41.5, 85) * mm});
            skLineSegment(sketch, "E3.8.15.1", {"start": v(46.5, 85) * mm, "end": v(46.5, 80) * mm});
            skLineSegment(sketch, "E3.8.15.2", {"start": v(46.5, 80) * mm, "end": v(41.5, 80) * mm});
            skLineSegment(sketch, "E3.8.15.3", {"start": v(41.5, 85) * mm, "end": v(41.5, 80) * mm});
            skPoint(sketch, "E3.8.15.4", {"position": v(44, 82.5) * mm});
            skLineSegment(sketch, "E3.8.16.0", {"start": v(46.5, 90.5) * mm, "end": v(41.5, 90.5) * mm});
            skLineSegment(sketch, "E3.8.16.1", {"start": v(46.5, 90.5) * mm, "end": v(46.5, 85.5) * mm});
            skLineSegment(sketch, "E3.8.16.2", {"start": v(46.5, 85.5) * mm, "end": v(41.5, 85.5) * mm});
            skLineSegment(sketch, "E3.8.16.3", {"start": v(41.5, 90.5) * mm, "end": v(41.5, 85.5) * mm});
            skPoint(sketch, "E3.8.16.4", {"position": v(44, 88) * mm});
            skLineSegment(sketch, "E3.8.17.0", {"start": v(46.5, 96) * mm, "end": v(41.5, 96) * mm});
            skLineSegment(sketch, "E3.8.17.1", {"start": v(46.5, 96) * mm, "end": v(46.5, 91) * mm});
            skLineSegment(sketch, "E3.8.17.2", {"start": v(46.5, 91) * mm, "end": v(41.5, 91) * mm});
            skLineSegment(sketch, "E3.8.17.3", {"start": v(41.5, 96) * mm, "end": v(41.5, 91) * mm});
            skPoint(sketch, "E3.8.17.4", {"position": v(44, 93.5) * mm});
            skLineSegment(sketch, "E3.8.18.0", {"start": v(46.5, 101.5) * mm, "end": v(41.5, 101.5) * mm});
            skLineSegment(sketch, "E3.8.18.1", {"start": v(46.5, 101.5) * mm, "end": v(46.5, 96.5) * mm});
            skLineSegment(sketch, "E3.8.18.2", {"start": v(46.5, 96.5) * mm, "end": v(41.5, 96.5) * mm});
            skLineSegment(sketch, "E3.8.18.3", {"start": v(41.5, 101.5) * mm, "end": v(41.5, 96.5) * mm});
            skPoint(sketch, "E3.8.18.4", {"position": v(44, 99) * mm});
            skLineSegment(sketch, "E3.8.19.0", {"start": v(46.5, 107) * mm, "end": v(41.5, 107) * mm});
            skLineSegment(sketch, "E3.8.19.1", {"start": v(46.5, 107) * mm, "end": v(46.5, 102) * mm});
            skLineSegment(sketch, "E3.8.19.2", {"start": v(46.5, 102) * mm, "end": v(41.5, 102) * mm});
            skLineSegment(sketch, "E3.8.19.3", {"start": v(41.5, 107) * mm, "end": v(41.5, 102) * mm});
            skPoint(sketch, "E3.8.19.4", {"position": v(44, 104.5) * mm});
            skLineSegment(sketch, "E3.8.20.0", {"start": v(46.5, 112.5) * mm, "end": v(41.5, 112.5) * mm});
            skLineSegment(sketch, "E3.8.20.1", {"start": v(46.5, 112.5) * mm, "end": v(46.5, 107.5) * mm});
            skLineSegment(sketch, "E3.8.20.2", {"start": v(46.5, 107.5) * mm, "end": v(41.5, 107.5) * mm});
            skLineSegment(sketch, "E3.8.20.3", {"start": v(41.5, 112.5) * mm, "end": v(41.5, 107.5) * mm});
            skPoint(sketch, "E3.8.20.4", {"position": v(44, 110) * mm});
            skLineSegment(sketch, "E3.8.21.0", {"start": v(46.5, 118) * mm, "end": v(41.5, 118) * mm});
            skLineSegment(sketch, "E3.8.21.1", {"start": v(46.5, 118) * mm, "end": v(46.5, 113) * mm});
            skLineSegment(sketch, "E3.8.21.2", {"start": v(46.5, 113) * mm, "end": v(41.5, 113) * mm});
            skLineSegment(sketch, "E3.8.21.3", {"start": v(41.5, 118) * mm, "end": v(41.5, 113) * mm});
            skPoint(sketch, "E3.8.21.4", {"position": v(44, 115.5) * mm});
            skLineSegment(sketch, "E3.8.22.0", {"start": v(46.5, 123.5) * mm, "end": v(41.5, 123.5) * mm});
            skLineSegment(sketch, "E3.8.22.1", {"start": v(46.5, 123.5) * mm, "end": v(46.5, 118.5) * mm});
            skLineSegment(sketch, "E3.8.22.2", {"start": v(46.5, 118.5) * mm, "end": v(41.5, 118.5) * mm});
            skLineSegment(sketch, "E3.8.22.3", {"start": v(41.5, 123.5) * mm, "end": v(41.5, 118.5) * mm});
            skPoint(sketch, "E3.8.22.4", {"position": v(44, 121) * mm});
            skLineSegment(sketch, "E3.8.23.0", {"start": v(46.5, 129) * mm, "end": v(41.5, 129) * mm});
            skLineSegment(sketch, "E3.8.23.1", {"start": v(46.5, 129) * mm, "end": v(46.5, 124) * mm});
            skLineSegment(sketch, "E3.8.23.2", {"start": v(46.5, 124) * mm, "end": v(41.5, 124) * mm});
            skLineSegment(sketch, "E3.8.23.3", {"start": v(41.5, 129) * mm, "end": v(41.5, 124) * mm});
            skPoint(sketch, "E3.8.23.4", {"position": v(44, 126.5) * mm});
            skLineSegment(sketch, "E3.8.24.0", {"start": v(46.5, 134.5) * mm, "end": v(41.5, 134.5) * mm});
            skLineSegment(sketch, "E3.8.24.1", {"start": v(46.5, 134.5) * mm, "end": v(46.5, 129.5) * mm});
            skLineSegment(sketch, "E3.8.24.2", {"start": v(46.5, 129.5) * mm, "end": v(41.5, 129.5) * mm});
            skLineSegment(sketch, "E3.8.24.3", {"start": v(41.5, 134.5) * mm, "end": v(41.5, 129.5) * mm});
            skPoint(sketch, "E3.8.24.4", {"position": v(44, 132) * mm});
            skLineSegment(sketch, "E3.9.0.0", {"start": v(52, 2.5) * mm, "end": v(47, 2.5) * mm});
            skLineSegment(sketch, "E3.9.0.1", {"start": v(52, 2.5) * mm, "end": v(52, -2.5) * mm});
            skLineSegment(sketch, "E3.9.0.2", {"start": v(52, -2.5) * mm, "end": v(47, -2.5) * mm});
            skLineSegment(sketch, "E3.9.0.3", {"start": v(47, 2.5) * mm, "end": v(47, -2.5) * mm});
            skPoint(sketch, "E3.9.0.4", {"position": v(49.5, 0) * mm});
            skLineSegment(sketch, "E3.9.1.0", {"start": v(52, 8) * mm, "end": v(47, 8) * mm});
            skLineSegment(sketch, "E3.9.1.1", {"start": v(52, 8) * mm, "end": v(52, 3) * mm});
            skLineSegment(sketch, "E3.9.1.2", {"start": v(52, 3) * mm, "end": v(47, 3) * mm});
            skLineSegment(sketch, "E3.9.1.3", {"start": v(47, 8) * mm, "end": v(47, 3) * mm});
            skPoint(sketch, "E3.9.1.4", {"position": v(49.5, 5.5) * mm});
            skLineSegment(sketch, "E3.9.2.0", {"start": v(52, 13.5) * mm, "end": v(47, 13.5) * mm});
            skLineSegment(sketch, "E3.9.2.1", {"start": v(52, 13.5) * mm, "end": v(52, 8.5) * mm});
            skLineSegment(sketch, "E3.9.2.2", {"start": v(52, 8.5) * mm, "end": v(47, 8.5) * mm});
            skLineSegment(sketch, "E3.9.2.3", {"start": v(47, 13.5) * mm, "end": v(47, 8.5) * mm});
            skPoint(sketch, "E3.9.2.4", {"position": v(49.5, 11) * mm});
            skLineSegment(sketch, "E3.9.3.0", {"start": v(52, 19) * mm, "end": v(47, 19) * mm});
            skLineSegment(sketch, "E3.9.3.1", {"start": v(52, 19) * mm, "end": v(52, 14) * mm});
            skLineSegment(sketch, "E3.9.3.2", {"start": v(52, 14) * mm, "end": v(47, 14) * mm});
            skLineSegment(sketch, "E3.9.3.3", {"start": v(47, 19) * mm, "end": v(47, 14) * mm});
            skPoint(sketch, "E3.9.3.4", {"position": v(49.5, 16.5) * mm});
            skLineSegment(sketch, "E3.9.4.0", {"start": v(52, 24.5) * mm, "end": v(47, 24.5) * mm});
            skLineSegment(sketch, "E3.9.4.1", {"start": v(52, 24.5) * mm, "end": v(52, 19.5) * mm});
            skLineSegment(sketch, "E3.9.4.2", {"start": v(52, 19.5) * mm, "end": v(47, 19.5) * mm});
            skLineSegment(sketch, "E3.9.4.3", {"start": v(47, 24.5) * mm, "end": v(47, 19.5) * mm});
            skPoint(sketch, "E3.9.4.4", {"position": v(49.5, 22) * mm});
            skLineSegment(sketch, "E3.9.5.0", {"start": v(52, 30) * mm, "end": v(47, 30) * mm});
            skLineSegment(sketch, "E3.9.5.1", {"start": v(52, 30) * mm, "end": v(52, 25) * mm});
            skLineSegment(sketch, "E3.9.5.2", {"start": v(52, 25) * mm, "end": v(47, 25) * mm});
            skLineSegment(sketch, "E3.9.5.3", {"start": v(47, 30) * mm, "end": v(47, 25) * mm});
            skPoint(sketch, "E3.9.5.4", {"position": v(49.5, 27.5) * mm});
            skLineSegment(sketch, "E3.9.6.0", {"start": v(52, 35.5) * mm, "end": v(47, 35.5) * mm});
            skLineSegment(sketch, "E3.9.6.1", {"start": v(52, 35.5) * mm, "end": v(52, 30.5) * mm});
            skLineSegment(sketch, "E3.9.6.2", {"start": v(52, 30.5) * mm, "end": v(47, 30.5) * mm});
            skLineSegment(sketch, "E3.9.6.3", {"start": v(47, 35.5) * mm, "end": v(47, 30.5) * mm});
            skPoint(sketch, "E3.9.6.4", {"position": v(49.5, 33) * mm});
            skLineSegment(sketch, "E3.9.7.0", {"start": v(52, 41) * mm, "end": v(47, 41) * mm});
            skLineSegment(sketch, "E3.9.7.1", {"start": v(52, 41) * mm, "end": v(52, 36) * mm});
            skLineSegment(sketch, "E3.9.7.2", {"start": v(52, 36) * mm, "end": v(47, 36) * mm});
            skLineSegment(sketch, "E3.9.7.3", {"start": v(47, 41) * mm, "end": v(47, 36) * mm});
            skPoint(sketch, "E3.9.7.4", {"position": v(49.5, 38.5) * mm});
            skLineSegment(sketch, "E3.9.8.0", {"start": v(52, 46.5) * mm, "end": v(47, 46.5) * mm});
            skLineSegment(sketch, "E3.9.8.1", {"start": v(52, 46.5) * mm, "end": v(52, 41.5) * mm});
            skLineSegment(sketch, "E3.9.8.2", {"start": v(52, 41.5) * mm, "end": v(47, 41.5) * mm});
            skLineSegment(sketch, "E3.9.8.3", {"start": v(47, 46.5) * mm, "end": v(47, 41.5) * mm});
            skPoint(sketch, "E3.9.8.4", {"position": v(49.5, 44) * mm});
            skLineSegment(sketch, "E3.9.9.0", {"start": v(52, 52) * mm, "end": v(47, 52) * mm});
            skLineSegment(sketch, "E3.9.9.1", {"start": v(52, 52) * mm, "end": v(52, 47) * mm});
            skLineSegment(sketch, "E3.9.9.2", {"start": v(52, 47) * mm, "end": v(47, 47) * mm});
            skLineSegment(sketch, "E3.9.9.3", {"start": v(47, 52) * mm, "end": v(47, 47) * mm});
            skPoint(sketch, "E3.9.9.4", {"position": v(49.5, 49.5) * mm});
            skLineSegment(sketch, "E3.9.10.0", {"start": v(52, 57.5) * mm, "end": v(47, 57.5) * mm});
            skLineSegment(sketch, "E3.9.10.1", {"start": v(52, 57.5) * mm, "end": v(52, 52.5) * mm});
            skLineSegment(sketch, "E3.9.10.2", {"start": v(52, 52.5) * mm, "end": v(47, 52.5) * mm});
            skLineSegment(sketch, "E3.9.10.3", {"start": v(47, 57.5) * mm, "end": v(47, 52.5) * mm});
            skPoint(sketch, "E3.9.10.4", {"position": v(49.5, 55) * mm});
            skLineSegment(sketch, "E3.9.11.0", {"start": v(52, 63) * mm, "end": v(47, 63) * mm});
            skLineSegment(sketch, "E3.9.11.1", {"start": v(52, 63) * mm, "end": v(52, 58) * mm});
            skLineSegment(sketch, "E3.9.11.2", {"start": v(52, 58) * mm, "end": v(47, 58) * mm});
            skLineSegment(sketch, "E3.9.11.3", {"start": v(47, 63) * mm, "end": v(47, 58) * mm});
            skPoint(sketch, "E3.9.11.4", {"position": v(49.5, 60.5) * mm});
            skLineSegment(sketch, "E3.9.12.0", {"start": v(52, 68.5) * mm, "end": v(47, 68.5) * mm});
            skLineSegment(sketch, "E3.9.12.1", {"start": v(52, 68.5) * mm, "end": v(52, 63.5) * mm});
            skLineSegment(sketch, "E3.9.12.2", {"start": v(52, 63.5) * mm, "end": v(47, 63.5) * mm});
            skLineSegment(sketch, "E3.9.12.3", {"start": v(47, 68.5) * mm, "end": v(47, 63.5) * mm});
            skPoint(sketch, "E3.9.12.4", {"position": v(49.5, 66) * mm});
            skLineSegment(sketch, "E3.9.13.0", {"start": v(52, 74) * mm, "end": v(47, 74) * mm});
            skLineSegment(sketch, "E3.9.13.1", {"start": v(52, 74) * mm, "end": v(52, 69) * mm});
            skLineSegment(sketch, "E3.9.13.2", {"start": v(52, 69) * mm, "end": v(47, 69) * mm});
            skLineSegment(sketch, "E3.9.13.3", {"start": v(47, 74) * mm, "end": v(47, 69) * mm});
            skPoint(sketch, "E3.9.13.4", {"position": v(49.5, 71.5) * mm});
            skLineSegment(sketch, "E3.9.14.0", {"start": v(52, 79.5) * mm, "end": v(47, 79.5) * mm});
            skLineSegment(sketch, "E3.9.14.1", {"start": v(52, 79.5) * mm, "end": v(52, 74.5) * mm});
            skLineSegment(sketch, "E3.9.14.2", {"start": v(52, 74.5) * mm, "end": v(47, 74.5) * mm});
            skLineSegment(sketch, "E3.9.14.3", {"start": v(47, 79.5) * mm, "end": v(47, 74.5) * mm});
            skPoint(sketch, "E3.9.14.4", {"position": v(49.5, 77) * mm});
            skLineSegment(sketch, "E3.9.15.0", {"start": v(52, 85) * mm, "end": v(47, 85) * mm});
            skLineSegment(sketch, "E3.9.15.1", {"start": v(52, 85) * mm, "end": v(52, 80) * mm});
            skLineSegment(sketch, "E3.9.15.2", {"start": v(52, 80) * mm, "end": v(47, 80) * mm});
            skLineSegment(sketch, "E3.9.15.3", {"start": v(47, 85) * mm, "end": v(47, 80) * mm});
            skPoint(sketch, "E3.9.15.4", {"position": v(49.5, 82.5) * mm});
            skLineSegment(sketch, "E3.9.16.0", {"start": v(52, 90.5) * mm, "end": v(47, 90.5) * mm});
            skLineSegment(sketch, "E3.9.16.1", {"start": v(52, 90.5) * mm, "end": v(52, 85.5) * mm});
            skLineSegment(sketch, "E3.9.16.2", {"start": v(52, 85.5) * mm, "end": v(47, 85.5) * mm});
            skLineSegment(sketch, "E3.9.16.3", {"start": v(47, 90.5) * mm, "end": v(47, 85.5) * mm});
            skPoint(sketch, "E3.9.16.4", {"position": v(49.5, 88) * mm});
            skLineSegment(sketch, "E3.9.17.0", {"start": v(52, 96) * mm, "end": v(47, 96) * mm});
            skLineSegment(sketch, "E3.9.17.1", {"start": v(52, 96) * mm, "end": v(52, 91) * mm});
            skLineSegment(sketch, "E3.9.17.2", {"start": v(52, 91) * mm, "end": v(47, 91) * mm});
            skLineSegment(sketch, "E3.9.17.3", {"start": v(47, 96) * mm, "end": v(47, 91) * mm});
            skPoint(sketch, "E3.9.17.4", {"position": v(49.5, 93.5) * mm});
            skLineSegment(sketch, "E3.9.18.0", {"start": v(52, 101.5) * mm, "end": v(47, 101.5) * mm});
            skLineSegment(sketch, "E3.9.18.1", {"start": v(52, 101.5) * mm, "end": v(52, 96.5) * mm});
            skLineSegment(sketch, "E3.9.18.2", {"start": v(52, 96.5) * mm, "end": v(47, 96.5) * mm});
            skLineSegment(sketch, "E3.9.18.3", {"start": v(47, 101.5) * mm, "end": v(47, 96.5) * mm});
            skPoint(sketch, "E3.9.18.4", {"position": v(49.5, 99) * mm});
            skLineSegment(sketch, "E3.9.19.0", {"start": v(52, 107) * mm, "end": v(47, 107) * mm});
            skLineSegment(sketch, "E3.9.19.1", {"start": v(52, 107) * mm, "end": v(52, 102) * mm});
            skLineSegment(sketch, "E3.9.19.2", {"start": v(52, 102) * mm, "end": v(47, 102) * mm});
            skLineSegment(sketch, "E3.9.19.3", {"start": v(47, 107) * mm, "end": v(47, 102) * mm});
            skPoint(sketch, "E3.9.19.4", {"position": v(49.5, 104.5) * mm});
            skLineSegment(sketch, "E3.9.20.0", {"start": v(52, 112.5) * mm, "end": v(47, 112.5) * mm});
            skLineSegment(sketch, "E3.9.20.1", {"start": v(52, 112.5) * mm, "end": v(52, 107.5) * mm});
            skLineSegment(sketch, "E3.9.20.2", {"start": v(52, 107.5) * mm, "end": v(47, 107.5) * mm});
            skLineSegment(sketch, "E3.9.20.3", {"start": v(47, 112.5) * mm, "end": v(47, 107.5) * mm});
            skPoint(sketch, "E3.9.20.4", {"position": v(49.5, 110) * mm});
            skLineSegment(sketch, "E3.9.21.0", {"start": v(52, 118) * mm, "end": v(47, 118) * mm});
            skLineSegment(sketch, "E3.9.21.1", {"start": v(52, 118) * mm, "end": v(52, 113) * mm});
            skLineSegment(sketch, "E3.9.21.2", {"start": v(52, 113) * mm, "end": v(47, 113) * mm});
            skLineSegment(sketch, "E3.9.21.3", {"start": v(47, 118) * mm, "end": v(47, 113) * mm});
            skPoint(sketch, "E3.9.21.4", {"position": v(49.5, 115.5) * mm});
            skLineSegment(sketch, "E3.9.22.0", {"start": v(52, 123.5) * mm, "end": v(47, 123.5) * mm});
            skLineSegment(sketch, "E3.9.22.1", {"start": v(52, 123.5) * mm, "end": v(52, 118.5) * mm});
            skLineSegment(sketch, "E3.9.22.2", {"start": v(52, 118.5) * mm, "end": v(47, 118.5) * mm});
            skLineSegment(sketch, "E3.9.22.3", {"start": v(47, 123.5) * mm, "end": v(47, 118.5) * mm});
            skPoint(sketch, "E3.9.22.4", {"position": v(49.5, 121) * mm});
            skLineSegment(sketch, "E3.9.23.0", {"start": v(52, 129) * mm, "end": v(47, 129) * mm});
            skLineSegment(sketch, "E3.9.23.1", {"start": v(52, 129) * mm, "end": v(52, 124) * mm});
            skLineSegment(sketch, "E3.9.23.2", {"start": v(52, 124) * mm, "end": v(47, 124) * mm});
            skLineSegment(sketch, "E3.9.23.3", {"start": v(47, 129) * mm, "end": v(47, 124) * mm});
            skPoint(sketch, "E3.9.23.4", {"position": v(49.5, 126.5) * mm});
            skLineSegment(sketch, "E3.9.24.0", {"start": v(52, 134.5) * mm, "end": v(47, 134.5) * mm});
            skLineSegment(sketch, "E3.9.24.1", {"start": v(52, 134.5) * mm, "end": v(52, 129.5) * mm});
            skLineSegment(sketch, "E3.9.24.2", {"start": v(52, 129.5) * mm, "end": v(47, 129.5) * mm});
            skLineSegment(sketch, "E3.9.24.3", {"start": v(47, 134.5) * mm, "end": v(47, 129.5) * mm});
            skPoint(sketch, "E3.9.24.4", {"position": v(49.5, 132) * mm});
            skLineSegment(sketch, "E3.10.0.0", {"start": v(57.5, 2.5) * mm, "end": v(52.5, 2.5) * mm});
            skLineSegment(sketch, "E3.10.0.1", {"start": v(57.5, 2.5) * mm, "end": v(57.5, -2.5) * mm});
            skLineSegment(sketch, "E3.10.0.2", {"start": v(57.5, -2.5) * mm, "end": v(52.5, -2.5) * mm});
            skLineSegment(sketch, "E3.10.0.3", {"start": v(52.5, 2.5) * mm, "end": v(52.5, -2.5) * mm});
            skPoint(sketch, "E3.10.0.4", {"position": v(55, 0) * mm});
            skLineSegment(sketch, "E3.10.1.0", {"start": v(57.5, 8) * mm, "end": v(52.5, 8) * mm});
            skLineSegment(sketch, "E3.10.1.1", {"start": v(57.5, 8) * mm, "end": v(57.5, 3) * mm});
            skLineSegment(sketch, "E3.10.1.2", {"start": v(57.5, 3) * mm, "end": v(52.5, 3) * mm});
            skLineSegment(sketch, "E3.10.1.3", {"start": v(52.5, 8) * mm, "end": v(52.5, 3) * mm});
            skPoint(sketch, "E3.10.1.4", {"position": v(55, 5.5) * mm});
            skLineSegment(sketch, "E3.10.2.0", {"start": v(57.5, 13.5) * mm, "end": v(52.5, 13.5) * mm});
            skLineSegment(sketch, "E3.10.2.1", {"start": v(57.5, 13.5) * mm, "end": v(57.5, 8.5) * mm});
            skLineSegment(sketch, "E3.10.2.2", {"start": v(57.5, 8.5) * mm, "end": v(52.5, 8.5) * mm});
            skLineSegment(sketch, "E3.10.2.3", {"start": v(52.5, 13.5) * mm, "end": v(52.5, 8.5) * mm});
            skPoint(sketch, "E3.10.2.4", {"position": v(55, 11) * mm});
            skLineSegment(sketch, "E3.10.3.0", {"start": v(57.5, 19) * mm, "end": v(52.5, 19) * mm});
            skLineSegment(sketch, "E3.10.3.1", {"start": v(57.5, 19) * mm, "end": v(57.5, 14) * mm});
            skLineSegment(sketch, "E3.10.3.2", {"start": v(57.5, 14) * mm, "end": v(52.5, 14) * mm});
            skLineSegment(sketch, "E3.10.3.3", {"start": v(52.5, 19) * mm, "end": v(52.5, 14) * mm});
            skPoint(sketch, "E3.10.3.4", {"position": v(55, 16.5) * mm});
            skLineSegment(sketch, "E3.10.4.0", {"start": v(57.5, 24.5) * mm, "end": v(52.5, 24.5) * mm});
            skLineSegment(sketch, "E3.10.4.1", {"start": v(57.5, 24.5) * mm, "end": v(57.5, 19.5) * mm});
            skLineSegment(sketch, "E3.10.4.2", {"start": v(57.5, 19.5) * mm, "end": v(52.5, 19.5) * mm});
            skLineSegment(sketch, "E3.10.4.3", {"start": v(52.5, 24.5) * mm, "end": v(52.5, 19.5) * mm});
            skPoint(sketch, "E3.10.4.4", {"position": v(55, 22) * mm});
            skLineSegment(sketch, "E3.10.5.0", {"start": v(57.5, 30) * mm, "end": v(52.5, 30) * mm});
            skLineSegment(sketch, "E3.10.5.1", {"start": v(57.5, 30) * mm, "end": v(57.5, 25) * mm});
            skLineSegment(sketch, "E3.10.5.2", {"start": v(57.5, 25) * mm, "end": v(52.5, 25) * mm});
            skLineSegment(sketch, "E3.10.5.3", {"start": v(52.5, 30) * mm, "end": v(52.5, 25) * mm});
            skPoint(sketch, "E3.10.5.4", {"position": v(55, 27.5) * mm});
            skLineSegment(sketch, "E3.10.6.0", {"start": v(57.5, 35.5) * mm, "end": v(52.5, 35.5) * mm});
            skLineSegment(sketch, "E3.10.6.1", {"start": v(57.5, 35.5) * mm, "end": v(57.5, 30.5) * mm});
            skLineSegment(sketch, "E3.10.6.2", {"start": v(57.5, 30.5) * mm, "end": v(52.5, 30.5) * mm});
            skLineSegment(sketch, "E3.10.6.3", {"start": v(52.5, 35.5) * mm, "end": v(52.5, 30.5) * mm});
            skPoint(sketch, "E3.10.6.4", {"position": v(55, 33) * mm});
            skLineSegment(sketch, "E3.10.7.0", {"start": v(57.5, 41) * mm, "end": v(52.5, 41) * mm});
            skLineSegment(sketch, "E3.10.7.1", {"start": v(57.5, 41) * mm, "end": v(57.5, 36) * mm});
            skLineSegment(sketch, "E3.10.7.2", {"start": v(57.5, 36) * mm, "end": v(52.5, 36) * mm});
            skLineSegment(sketch, "E3.10.7.3", {"start": v(52.5, 41) * mm, "end": v(52.5, 36) * mm});
            skPoint(sketch, "E3.10.7.4", {"position": v(55, 38.5) * mm});
            skLineSegment(sketch, "E3.10.8.0", {"start": v(57.5, 46.5) * mm, "end": v(52.5, 46.5) * mm});
            skLineSegment(sketch, "E3.10.8.1", {"start": v(57.5, 46.5) * mm, "end": v(57.5, 41.5) * mm});
            skLineSegment(sketch, "E3.10.8.2", {"start": v(57.5, 41.5) * mm, "end": v(52.5, 41.5) * mm});
            skLineSegment(sketch, "E3.10.8.3", {"start": v(52.5, 46.5) * mm, "end": v(52.5, 41.5) * mm});
            skPoint(sketch, "E3.10.8.4", {"position": v(55, 44) * mm});
            skLineSegment(sketch, "E3.10.9.0", {"start": v(57.5, 52) * mm, "end": v(52.5, 52) * mm});
            skLineSegment(sketch, "E3.10.9.1", {"start": v(57.5, 52) * mm, "end": v(57.5, 47) * mm});
            skLineSegment(sketch, "E3.10.9.2", {"start": v(57.5, 47) * mm, "end": v(52.5, 47) * mm});
            skLineSegment(sketch, "E3.10.9.3", {"start": v(52.5, 52) * mm, "end": v(52.5, 47) * mm});
            skPoint(sketch, "E3.10.9.4", {"position": v(55, 49.5) * mm});
            skLineSegment(sketch, "E3.10.10.0", {"start": v(57.5, 57.5) * mm, "end": v(52.5, 57.5) * mm});
            skLineSegment(sketch, "E3.10.10.1", {"start": v(57.5, 57.5) * mm, "end": v(57.5, 52.5) * mm});
            skLineSegment(sketch, "E3.10.10.2", {"start": v(57.5, 52.5) * mm, "end": v(52.5, 52.5) * mm});
            skLineSegment(sketch, "E3.10.10.3", {"start": v(52.5, 57.5) * mm, "end": v(52.5, 52.5) * mm});
            skPoint(sketch, "E3.10.10.4", {"position": v(55, 55) * mm});
            skLineSegment(sketch, "E3.10.11.0", {"start": v(57.5, 63) * mm, "end": v(52.5, 63) * mm});
            skLineSegment(sketch, "E3.10.11.1", {"start": v(57.5, 63) * mm, "end": v(57.5, 58) * mm});
            skLineSegment(sketch, "E3.10.11.2", {"start": v(57.5, 58) * mm, "end": v(52.5, 58) * mm});
            skLineSegment(sketch, "E3.10.11.3", {"start": v(52.5, 63) * mm, "end": v(52.5, 58) * mm});
            skPoint(sketch, "E3.10.11.4", {"position": v(55, 60.5) * mm});
            skLineSegment(sketch, "E3.10.12.0", {"start": v(57.5, 68.5) * mm, "end": v(52.5, 68.5) * mm});
            skLineSegment(sketch, "E3.10.12.1", {"start": v(57.5, 68.5) * mm, "end": v(57.5, 63.5) * mm});
            skLineSegment(sketch, "E3.10.12.2", {"start": v(57.5, 63.5) * mm, "end": v(52.5, 63.5) * mm});
            skLineSegment(sketch, "E3.10.12.3", {"start": v(52.5, 68.5) * mm, "end": v(52.5, 63.5) * mm});
            skPoint(sketch, "E3.10.12.4", {"position": v(55, 66) * mm});
            skLineSegment(sketch, "E3.10.13.0", {"start": v(57.5, 74) * mm, "end": v(52.5, 74) * mm});
            skLineSegment(sketch, "E3.10.13.1", {"start": v(57.5, 74) * mm, "end": v(57.5, 69) * mm});
            skLineSegment(sketch, "E3.10.13.2", {"start": v(57.5, 69) * mm, "end": v(52.5, 69) * mm});
            skLineSegment(sketch, "E3.10.13.3", {"start": v(52.5, 74) * mm, "end": v(52.5, 69) * mm});
            skPoint(sketch, "E3.10.13.4", {"position": v(55, 71.5) * mm});
            skLineSegment(sketch, "E3.10.14.0", {"start": v(57.5, 79.5) * mm, "end": v(52.5, 79.5) * mm});
            skLineSegment(sketch, "E3.10.14.1", {"start": v(57.5, 79.5) * mm, "end": v(57.5, 74.5) * mm});
            skLineSegment(sketch, "E3.10.14.2", {"start": v(57.5, 74.5) * mm, "end": v(52.5, 74.5) * mm});
            skLineSegment(sketch, "E3.10.14.3", {"start": v(52.5, 79.5) * mm, "end": v(52.5, 74.5) * mm});
            skPoint(sketch, "E3.10.14.4", {"position": v(55, 77) * mm});
            skLineSegment(sketch, "E3.10.15.0", {"start": v(57.5, 85) * mm, "end": v(52.5, 85) * mm});
            skLineSegment(sketch, "E3.10.15.1", {"start": v(57.5, 85) * mm, "end": v(57.5, 80) * mm});
            skLineSegment(sketch, "E3.10.15.2", {"start": v(57.5, 80) * mm, "end": v(52.5, 80) * mm});
            skLineSegment(sketch, "E3.10.15.3", {"start": v(52.5, 85) * mm, "end": v(52.5, 80) * mm});
            skPoint(sketch, "E3.10.15.4", {"position": v(55, 82.5) * mm});
            skLineSegment(sketch, "E3.10.16.0", {"start": v(57.5, 90.5) * mm, "end": v(52.5, 90.5) * mm});
            skLineSegment(sketch, "E3.10.16.1", {"start": v(57.5, 90.5) * mm, "end": v(57.5, 85.5) * mm});
            skLineSegment(sketch, "E3.10.16.2", {"start": v(57.5, 85.5) * mm, "end": v(52.5, 85.5) * mm});
            skLineSegment(sketch, "E3.10.16.3", {"start": v(52.5, 90.5) * mm, "end": v(52.5, 85.5) * mm});
            skPoint(sketch, "E3.10.16.4", {"position": v(55, 88) * mm});
            skLineSegment(sketch, "E3.10.17.0", {"start": v(57.5, 96) * mm, "end": v(52.5, 96) * mm});
            skLineSegment(sketch, "E3.10.17.1", {"start": v(57.5, 96) * mm, "end": v(57.5, 91) * mm});
            skLineSegment(sketch, "E3.10.17.2", {"start": v(57.5, 91) * mm, "end": v(52.5, 91) * mm});
            skLineSegment(sketch, "E3.10.17.3", {"start": v(52.5, 96) * mm, "end": v(52.5, 91) * mm});
            skPoint(sketch, "E3.10.17.4", {"position": v(55, 93.5) * mm});
            skLineSegment(sketch, "E3.10.18.0", {"start": v(57.5, 101.5) * mm, "end": v(52.5, 101.5) * mm});
            skLineSegment(sketch, "E3.10.18.1", {"start": v(57.5, 101.5) * mm, "end": v(57.5, 96.5) * mm});
            skLineSegment(sketch, "E3.10.18.2", {"start": v(57.5, 96.5) * mm, "end": v(52.5, 96.5) * mm});
            skLineSegment(sketch, "E3.10.18.3", {"start": v(52.5, 101.5) * mm, "end": v(52.5, 96.5) * mm});
            skPoint(sketch, "E3.10.18.4", {"position": v(55, 99) * mm});
            skLineSegment(sketch, "E3.10.19.0", {"start": v(57.5, 107) * mm, "end": v(52.5, 107) * mm});
            skLineSegment(sketch, "E3.10.19.1", {"start": v(57.5, 107) * mm, "end": v(57.5, 102) * mm});
            skLineSegment(sketch, "E3.10.19.2", {"start": v(57.5, 102) * mm, "end": v(52.5, 102) * mm});
            skLineSegment(sketch, "E3.10.19.3", {"start": v(52.5, 107) * mm, "end": v(52.5, 102) * mm});
            skPoint(sketch, "E3.10.19.4", {"position": v(55, 104.5) * mm});
            skLineSegment(sketch, "E3.10.20.0", {"start": v(57.5, 112.5) * mm, "end": v(52.5, 112.5) * mm});
            skLineSegment(sketch, "E3.10.20.1", {"start": v(57.5, 112.5) * mm, "end": v(57.5, 107.5) * mm});
            skLineSegment(sketch, "E3.10.20.2", {"start": v(57.5, 107.5) * mm, "end": v(52.5, 107.5) * mm});
            skLineSegment(sketch, "E3.10.20.3", {"start": v(52.5, 112.5) * mm, "end": v(52.5, 107.5) * mm});
            skPoint(sketch, "E3.10.20.4", {"position": v(55, 110) * mm});
            skLineSegment(sketch, "E3.10.21.0", {"start": v(57.5, 118) * mm, "end": v(52.5, 118) * mm});
            skLineSegment(sketch, "E3.10.21.1", {"start": v(57.5, 118) * mm, "end": v(57.5, 113) * mm});
            skLineSegment(sketch, "E3.10.21.2", {"start": v(57.5, 113) * mm, "end": v(52.5, 113) * mm});
            skLineSegment(sketch, "E3.10.21.3", {"start": v(52.5, 118) * mm, "end": v(52.5, 113) * mm});
            skPoint(sketch, "E3.10.21.4", {"position": v(55, 115.5) * mm});
            skLineSegment(sketch, "E3.10.22.0", {"start": v(57.5, 123.5) * mm, "end": v(52.5, 123.5) * mm});
            skLineSegment(sketch, "E3.10.22.1", {"start": v(57.5, 123.5) * mm, "end": v(57.5, 118.5) * mm});
            skLineSegment(sketch, "E3.10.22.2", {"start": v(57.5, 118.5) * mm, "end": v(52.5, 118.5) * mm});
            skLineSegment(sketch, "E3.10.22.3", {"start": v(52.5, 123.5) * mm, "end": v(52.5, 118.5) * mm});
            skPoint(sketch, "E3.10.22.4", {"position": v(55, 121) * mm});
            skLineSegment(sketch, "E3.10.23.0", {"start": v(57.5, 129) * mm, "end": v(52.5, 129) * mm});
            skLineSegment(sketch, "E3.10.23.1", {"start": v(57.5, 129) * mm, "end": v(57.5, 124) * mm});
            skLineSegment(sketch, "E3.10.23.2", {"start": v(57.5, 124) * mm, "end": v(52.5, 124) * mm});
            skLineSegment(sketch, "E3.10.23.3", {"start": v(52.5, 129) * mm, "end": v(52.5, 124) * mm});
            skPoint(sketch, "E3.10.23.4", {"position": v(55, 126.5) * mm});
            skLineSegment(sketch, "E3.10.24.0", {"start": v(57.5, 134.5) * mm, "end": v(52.5, 134.5) * mm});
            skLineSegment(sketch, "E3.10.24.1", {"start": v(57.5, 134.5) * mm, "end": v(57.5, 129.5) * mm});
            skLineSegment(sketch, "E3.10.24.2", {"start": v(57.5, 129.5) * mm, "end": v(52.5, 129.5) * mm});
            skLineSegment(sketch, "E3.10.24.3", {"start": v(52.5, 134.5) * mm, "end": v(52.5, 129.5) * mm});
            skPoint(sketch, "E3.10.24.4", {"position": v(55, 132) * mm});
            skLineSegment(sketch, "E3.11.0.0", {"start": v(63, 2.5) * mm, "end": v(58, 2.5) * mm});
            skLineSegment(sketch, "E3.11.0.1", {"start": v(63, 2.5) * mm, "end": v(63, -2.5) * mm});
            skLineSegment(sketch, "E3.11.0.2", {"start": v(63, -2.5) * mm, "end": v(58, -2.5) * mm});
            skLineSegment(sketch, "E3.11.0.3", {"start": v(58, 2.5) * mm, "end": v(58, -2.5) * mm});
            skPoint(sketch, "E3.11.0.4", {"position": v(60.5, 0) * mm});
            skLineSegment(sketch, "E3.11.1.0", {"start": v(63, 8) * mm, "end": v(58, 8) * mm});
            skLineSegment(sketch, "E3.11.1.1", {"start": v(63, 8) * mm, "end": v(63, 3) * mm});
            skLineSegment(sketch, "E3.11.1.2", {"start": v(63, 3) * mm, "end": v(58, 3) * mm});
            skLineSegment(sketch, "E3.11.1.3", {"start": v(58, 8) * mm, "end": v(58, 3) * mm});
            skPoint(sketch, "E3.11.1.4", {"position": v(60.5, 5.5) * mm});
            skLineSegment(sketch, "E3.11.2.0", {"start": v(63, 13.5) * mm, "end": v(58, 13.5) * mm});
            skLineSegment(sketch, "E3.11.2.1", {"start": v(63, 13.5) * mm, "end": v(63, 8.5) * mm});
            skLineSegment(sketch, "E3.11.2.2", {"start": v(63, 8.5) * mm, "end": v(58, 8.5) * mm});
            skLineSegment(sketch, "E3.11.2.3", {"start": v(58, 13.5) * mm, "end": v(58, 8.5) * mm});
            skPoint(sketch, "E3.11.2.4", {"position": v(60.5, 11) * mm});
            skLineSegment(sketch, "E3.11.3.0", {"start": v(63, 19) * mm, "end": v(58, 19) * mm});
            skLineSegment(sketch, "E3.11.3.1", {"start": v(63, 19) * mm, "end": v(63, 14) * mm});
            skLineSegment(sketch, "E3.11.3.2", {"start": v(63, 14) * mm, "end": v(58, 14) * mm});
            skLineSegment(sketch, "E3.11.3.3", {"start": v(58, 19) * mm, "end": v(58, 14) * mm});
            skPoint(sketch, "E3.11.3.4", {"position": v(60.5, 16.5) * mm});
            skLineSegment(sketch, "E3.11.4.0", {"start": v(63, 24.5) * mm, "end": v(58, 24.5) * mm});
            skLineSegment(sketch, "E3.11.4.1", {"start": v(63, 24.5) * mm, "end": v(63, 19.5) * mm});
            skLineSegment(sketch, "E3.11.4.2", {"start": v(63, 19.5) * mm, "end": v(58, 19.5) * mm});
            skLineSegment(sketch, "E3.11.4.3", {"start": v(58, 24.5) * mm, "end": v(58, 19.5) * mm});
            skPoint(sketch, "E3.11.4.4", {"position": v(60.5, 22) * mm});
            skLineSegment(sketch, "E3.11.5.0", {"start": v(63, 30) * mm, "end": v(58, 30) * mm});
            skLineSegment(sketch, "E3.11.5.1", {"start": v(63, 30) * mm, "end": v(63, 25) * mm});
            skLineSegment(sketch, "E3.11.5.2", {"start": v(63, 25) * mm, "end": v(58, 25) * mm});
            skLineSegment(sketch, "E3.11.5.3", {"start": v(58, 30) * mm, "end": v(58, 25) * mm});
            skPoint(sketch, "E3.11.5.4", {"position": v(60.5, 27.5) * mm});
            skLineSegment(sketch, "E3.11.6.0", {"start": v(63, 35.5) * mm, "end": v(58, 35.5) * mm});
            skLineSegment(sketch, "E3.11.6.1", {"start": v(63, 35.5) * mm, "end": v(63, 30.5) * mm});
            skLineSegment(sketch, "E3.11.6.2", {"start": v(63, 30.5) * mm, "end": v(58, 30.5) * mm});
            skLineSegment(sketch, "E3.11.6.3", {"start": v(58, 35.5) * mm, "end": v(58, 30.5) * mm});
            skPoint(sketch, "E3.11.6.4", {"position": v(60.5, 33) * mm});
            skLineSegment(sketch, "E3.11.7.0", {"start": v(63, 41) * mm, "end": v(58, 41) * mm});
            skLineSegment(sketch, "E3.11.7.1", {"start": v(63, 41) * mm, "end": v(63, 36) * mm});
            skLineSegment(sketch, "E3.11.7.2", {"start": v(63, 36) * mm, "end": v(58, 36) * mm});
            skLineSegment(sketch, "E3.11.7.3", {"start": v(58, 41) * mm, "end": v(58, 36) * mm});
            skPoint(sketch, "E3.11.7.4", {"position": v(60.5, 38.5) * mm});
            skLineSegment(sketch, "E3.11.8.0", {"start": v(63, 46.5) * mm, "end": v(58, 46.5) * mm});
            skLineSegment(sketch, "E3.11.8.1", {"start": v(63, 46.5) * mm, "end": v(63, 41.5) * mm});
            skLineSegment(sketch, "E3.11.8.2", {"start": v(63, 41.5) * mm, "end": v(58, 41.5) * mm});
            skLineSegment(sketch, "E3.11.8.3", {"start": v(58, 46.5) * mm, "end": v(58, 41.5) * mm});
            skPoint(sketch, "E3.11.8.4", {"position": v(60.5, 44) * mm});
            skLineSegment(sketch, "E3.11.9.0", {"start": v(63, 52) * mm, "end": v(58, 52) * mm});
            skLineSegment(sketch, "E3.11.9.1", {"start": v(63, 52) * mm, "end": v(63, 47) * mm});
            skLineSegment(sketch, "E3.11.9.2", {"start": v(63, 47) * mm, "end": v(58, 47) * mm});
            skLineSegment(sketch, "E3.11.9.3", {"start": v(58, 52) * mm, "end": v(58, 47) * mm});
            skPoint(sketch, "E3.11.9.4", {"position": v(60.5, 49.5) * mm});
            skLineSegment(sketch, "E3.11.10.0", {"start": v(63, 57.5) * mm, "end": v(58, 57.5) * mm});
            skLineSegment(sketch, "E3.11.10.1", {"start": v(63, 57.5) * mm, "end": v(63, 52.5) * mm});
            skLineSegment(sketch, "E3.11.10.2", {"start": v(63, 52.5) * mm, "end": v(58, 52.5) * mm});
            skLineSegment(sketch, "E3.11.10.3", {"start": v(58, 57.5) * mm, "end": v(58, 52.5) * mm});
            skPoint(sketch, "E3.11.10.4", {"position": v(60.5, 55) * mm});
            skLineSegment(sketch, "E3.11.11.0", {"start": v(63, 63) * mm, "end": v(58, 63) * mm});
            skLineSegment(sketch, "E3.11.11.1", {"start": v(63, 63) * mm, "end": v(63, 58) * mm});
            skLineSegment(sketch, "E3.11.11.2", {"start": v(63, 58) * mm, "end": v(58, 58) * mm});
            skLineSegment(sketch, "E3.11.11.3", {"start": v(58, 63) * mm, "end": v(58, 58) * mm});
            skPoint(sketch, "E3.11.11.4", {"position": v(60.5, 60.5) * mm});
            skLineSegment(sketch, "E3.11.12.0", {"start": v(63, 68.5) * mm, "end": v(58, 68.5) * mm});
            skLineSegment(sketch, "E3.11.12.1", {"start": v(63, 68.5) * mm, "end": v(63, 63.5) * mm});
            skLineSegment(sketch, "E3.11.12.2", {"start": v(63, 63.5) * mm, "end": v(58, 63.5) * mm});
            skLineSegment(sketch, "E3.11.12.3", {"start": v(58, 68.5) * mm, "end": v(58, 63.5) * mm});
            skPoint(sketch, "E3.11.12.4", {"position": v(60.5, 66) * mm});
            skLineSegment(sketch, "E3.11.13.0", {"start": v(63, 74) * mm, "end": v(58, 74) * mm});
            skLineSegment(sketch, "E3.11.13.1", {"start": v(63, 74) * mm, "end": v(63, 69) * mm});
            skLineSegment(sketch, "E3.11.13.2", {"start": v(63, 69) * mm, "end": v(58, 69) * mm});
            skLineSegment(sketch, "E3.11.13.3", {"start": v(58, 74) * mm, "end": v(58, 69) * mm});
            skPoint(sketch, "E3.11.13.4", {"position": v(60.5, 71.5) * mm});
            skLineSegment(sketch, "E3.11.14.0", {"start": v(63, 79.5) * mm, "end": v(58, 79.5) * mm});
            skLineSegment(sketch, "E3.11.14.1", {"start": v(63, 79.5) * mm, "end": v(63, 74.5) * mm});
            skLineSegment(sketch, "E3.11.14.2", {"start": v(63, 74.5) * mm, "end": v(58, 74.5) * mm});
            skLineSegment(sketch, "E3.11.14.3", {"start": v(58, 79.5) * mm, "end": v(58, 74.5) * mm});
            skPoint(sketch, "E3.11.14.4", {"position": v(60.5, 77) * mm});
            skLineSegment(sketch, "E3.11.15.0", {"start": v(63, 85) * mm, "end": v(58, 85) * mm});
            skLineSegment(sketch, "E3.11.15.1", {"start": v(63, 85) * mm, "end": v(63, 80) * mm});
            skLineSegment(sketch, "E3.11.15.2", {"start": v(63, 80) * mm, "end": v(58, 80) * mm});
            skLineSegment(sketch, "E3.11.15.3", {"start": v(58, 85) * mm, "end": v(58, 80) * mm});
            skPoint(sketch, "E3.11.15.4", {"position": v(60.5, 82.5) * mm});
            skLineSegment(sketch, "E3.11.16.0", {"start": v(63, 90.5) * mm, "end": v(58, 90.5) * mm});
            skLineSegment(sketch, "E3.11.16.1", {"start": v(63, 90.5) * mm, "end": v(63, 85.5) * mm});
            skLineSegment(sketch, "E3.11.16.2", {"start": v(63, 85.5) * mm, "end": v(58, 85.5) * mm});
            skLineSegment(sketch, "E3.11.16.3", {"start": v(58, 90.5) * mm, "end": v(58, 85.5) * mm});
            skPoint(sketch, "E3.11.16.4", {"position": v(60.5, 88) * mm});
            skLineSegment(sketch, "E3.11.17.0", {"start": v(63, 96) * mm, "end": v(58, 96) * mm});
            skLineSegment(sketch, "E3.11.17.1", {"start": v(63, 96) * mm, "end": v(63, 91) * mm});
            skLineSegment(sketch, "E3.11.17.2", {"start": v(63, 91) * mm, "end": v(58, 91) * mm});
            skLineSegment(sketch, "E3.11.17.3", {"start": v(58, 96) * mm, "end": v(58, 91) * mm});
            skPoint(sketch, "E3.11.17.4", {"position": v(60.5, 93.5) * mm});
            skLineSegment(sketch, "E3.11.18.0", {"start": v(63, 101.5) * mm, "end": v(58, 101.5) * mm});
            skLineSegment(sketch, "E3.11.18.1", {"start": v(63, 101.5) * mm, "end": v(63, 96.5) * mm});
            skLineSegment(sketch, "E3.11.18.2", {"start": v(63, 96.5) * mm, "end": v(58, 96.5) * mm});
            skLineSegment(sketch, "E3.11.18.3", {"start": v(58, 101.5) * mm, "end": v(58, 96.5) * mm});
            skPoint(sketch, "E3.11.18.4", {"position": v(60.5, 99) * mm});
            skLineSegment(sketch, "E3.11.19.0", {"start": v(63, 107) * mm, "end": v(58, 107) * mm});
            skLineSegment(sketch, "E3.11.19.1", {"start": v(63, 107) * mm, "end": v(63, 102) * mm});
            skLineSegment(sketch, "E3.11.19.2", {"start": v(63, 102) * mm, "end": v(58, 102) * mm});
            skLineSegment(sketch, "E3.11.19.3", {"start": v(58, 107) * mm, "end": v(58, 102) * mm});
            skPoint(sketch, "E3.11.19.4", {"position": v(60.5, 104.5) * mm});
            skLineSegment(sketch, "E3.11.20.0", {"start": v(63, 112.5) * mm, "end": v(58, 112.5) * mm});
            skLineSegment(sketch, "E3.11.20.1", {"start": v(63, 112.5) * mm, "end": v(63, 107.5) * mm});
            skLineSegment(sketch, "E3.11.20.2", {"start": v(63, 107.5) * mm, "end": v(58, 107.5) * mm});
            skLineSegment(sketch, "E3.11.20.3", {"start": v(58, 112.5) * mm, "end": v(58, 107.5) * mm});
            skPoint(sketch, "E3.11.20.4", {"position": v(60.5, 110) * mm});
            skLineSegment(sketch, "E3.11.21.0", {"start": v(63, 118) * mm, "end": v(58, 118) * mm});
            skLineSegment(sketch, "E3.11.21.1", {"start": v(63, 118) * mm, "end": v(63, 113) * mm});
            skLineSegment(sketch, "E3.11.21.2", {"start": v(63, 113) * mm, "end": v(58, 113) * mm});
            skLineSegment(sketch, "E3.11.21.3", {"start": v(58, 118) * mm, "end": v(58, 113) * mm});
            skPoint(sketch, "E3.11.21.4", {"position": v(60.5, 115.5) * mm});
            skLineSegment(sketch, "E3.11.22.0", {"start": v(63, 123.5) * mm, "end": v(58, 123.5) * mm});
            skLineSegment(sketch, "E3.11.22.1", {"start": v(63, 123.5) * mm, "end": v(63, 118.5) * mm});
            skLineSegment(sketch, "E3.11.22.2", {"start": v(63, 118.5) * mm, "end": v(58, 118.5) * mm});
            skLineSegment(sketch, "E3.11.22.3", {"start": v(58, 123.5) * mm, "end": v(58, 118.5) * mm});
            skPoint(sketch, "E3.11.22.4", {"position": v(60.5, 121) * mm});
            skLineSegment(sketch, "E3.11.23.0", {"start": v(63, 129) * mm, "end": v(58, 129) * mm});
            skLineSegment(sketch, "E3.11.23.1", {"start": v(63, 129) * mm, "end": v(63, 124) * mm});
            skLineSegment(sketch, "E3.11.23.2", {"start": v(63, 124) * mm, "end": v(58, 124) * mm});
            skLineSegment(sketch, "E3.11.23.3", {"start": v(58, 129) * mm, "end": v(58, 124) * mm});
            skPoint(sketch, "E3.11.23.4", {"position": v(60.5, 126.5) * mm});
            skLineSegment(sketch, "E3.11.24.0", {"start": v(63, 134.5) * mm, "end": v(58, 134.5) * mm});
            skLineSegment(sketch, "E3.11.24.1", {"start": v(63, 134.5) * mm, "end": v(63, 129.5) * mm});
            skLineSegment(sketch, "E3.11.24.2", {"start": v(63, 129.5) * mm, "end": v(58, 129.5) * mm});
            skLineSegment(sketch, "E3.11.24.3", {"start": v(58, 134.5) * mm, "end": v(58, 129.5) * mm});
            skPoint(sketch, "E3.11.24.4", {"position": v(60.5, 132) * mm});
            skLineSegment(sketch, "E3.12.0.0", {"start": v(68.5, 2.5) * mm, "end": v(63.5, 2.5) * mm});
            skLineSegment(sketch, "E3.12.0.1", {"start": v(68.5, 2.5) * mm, "end": v(68.5, -2.5) * mm});
            skLineSegment(sketch, "E3.12.0.2", {"start": v(68.5, -2.5) * mm, "end": v(63.5, -2.5) * mm});
            skLineSegment(sketch, "E3.12.0.3", {"start": v(63.5, 2.5) * mm, "end": v(63.5, -2.5) * mm});
            skPoint(sketch, "E3.12.0.4", {"position": v(66, 0) * mm});
            skLineSegment(sketch, "E3.12.1.0", {"start": v(68.5, 8) * mm, "end": v(63.5, 8) * mm});
            skLineSegment(sketch, "E3.12.1.1", {"start": v(68.5, 8) * mm, "end": v(68.5, 3) * mm});
            skLineSegment(sketch, "E3.12.1.2", {"start": v(68.5, 3) * mm, "end": v(63.5, 3) * mm});
            skLineSegment(sketch, "E3.12.1.3", {"start": v(63.5, 8) * mm, "end": v(63.5, 3) * mm});
            skPoint(sketch, "E3.12.1.4", {"position": v(66, 5.5) * mm});
            skLineSegment(sketch, "E3.12.2.0", {"start": v(68.5, 13.5) * mm, "end": v(63.5, 13.5) * mm});
            skLineSegment(sketch, "E3.12.2.1", {"start": v(68.5, 13.5) * mm, "end": v(68.5, 8.5) * mm});
            skLineSegment(sketch, "E3.12.2.2", {"start": v(68.5, 8.5) * mm, "end": v(63.5, 8.5) * mm});
            skLineSegment(sketch, "E3.12.2.3", {"start": v(63.5, 13.5) * mm, "end": v(63.5, 8.5) * mm});
            skPoint(sketch, "E3.12.2.4", {"position": v(66, 11) * mm});
            skLineSegment(sketch, "E3.12.3.0", {"start": v(68.5, 19) * mm, "end": v(63.5, 19) * mm});
            skLineSegment(sketch, "E3.12.3.1", {"start": v(68.5, 19) * mm, "end": v(68.5, 14) * mm});
            skLineSegment(sketch, "E3.12.3.2", {"start": v(68.5, 14) * mm, "end": v(63.5, 14) * mm});
            skLineSegment(sketch, "E3.12.3.3", {"start": v(63.5, 19) * mm, "end": v(63.5, 14) * mm});
            skPoint(sketch, "E3.12.3.4", {"position": v(66, 16.5) * mm});
            skLineSegment(sketch, "E3.12.4.0", {"start": v(68.5, 24.5) * mm, "end": v(63.5, 24.5) * mm});
            skLineSegment(sketch, "E3.12.4.1", {"start": v(68.5, 24.5) * mm, "end": v(68.5, 19.5) * mm});
            skLineSegment(sketch, "E3.12.4.2", {"start": v(68.5, 19.5) * mm, "end": v(63.5, 19.5) * mm});
            skLineSegment(sketch, "E3.12.4.3", {"start": v(63.5, 24.5) * mm, "end": v(63.5, 19.5) * mm});
            skPoint(sketch, "E3.12.4.4", {"position": v(66, 22) * mm});
            skLineSegment(sketch, "E3.12.5.0", {"start": v(68.5, 30) * mm, "end": v(63.5, 30) * mm});
            skLineSegment(sketch, "E3.12.5.1", {"start": v(68.5, 30) * mm, "end": v(68.5, 25) * mm});
            skLineSegment(sketch, "E3.12.5.2", {"start": v(68.5, 25) * mm, "end": v(63.5, 25) * mm});
            skLineSegment(sketch, "E3.12.5.3", {"start": v(63.5, 30) * mm, "end": v(63.5, 25) * mm});
            skPoint(sketch, "E3.12.5.4", {"position": v(66, 27.5) * mm});
            skLineSegment(sketch, "E3.12.6.0", {"start": v(68.5, 35.5) * mm, "end": v(63.5, 35.5) * mm});
            skLineSegment(sketch, "E3.12.6.1", {"start": v(68.5, 35.5) * mm, "end": v(68.5, 30.5) * mm});
            skLineSegment(sketch, "E3.12.6.2", {"start": v(68.5, 30.5) * mm, "end": v(63.5, 30.5) * mm});
            skLineSegment(sketch, "E3.12.6.3", {"start": v(63.5, 35.5) * mm, "end": v(63.5, 30.5) * mm});
            skPoint(sketch, "E3.12.6.4", {"position": v(66, 33) * mm});
            skLineSegment(sketch, "E3.12.7.0", {"start": v(68.5, 41) * mm, "end": v(63.5, 41) * mm});
            skLineSegment(sketch, "E3.12.7.1", {"start": v(68.5, 41) * mm, "end": v(68.5, 36) * mm});
            skLineSegment(sketch, "E3.12.7.2", {"start": v(68.5, 36) * mm, "end": v(63.5, 36) * mm});
            skLineSegment(sketch, "E3.12.7.3", {"start": v(63.5, 41) * mm, "end": v(63.5, 36) * mm});
            skPoint(sketch, "E3.12.7.4", {"position": v(66, 38.5) * mm});
            skLineSegment(sketch, "E3.12.8.0", {"start": v(68.5, 46.5) * mm, "end": v(63.5, 46.5) * mm});
            skLineSegment(sketch, "E3.12.8.1", {"start": v(68.5, 46.5) * mm, "end": v(68.5, 41.5) * mm});
            skLineSegment(sketch, "E3.12.8.2", {"start": v(68.5, 41.5) * mm, "end": v(63.5, 41.5) * mm});
            skLineSegment(sketch, "E3.12.8.3", {"start": v(63.5, 46.5) * mm, "end": v(63.5, 41.5) * mm});
            skPoint(sketch, "E3.12.8.4", {"position": v(66, 44) * mm});
            skLineSegment(sketch, "E3.12.9.0", {"start": v(68.5, 52) * mm, "end": v(63.5, 52) * mm});
            skLineSegment(sketch, "E3.12.9.1", {"start": v(68.5, 52) * mm, "end": v(68.5, 47) * mm});
            skLineSegment(sketch, "E3.12.9.2", {"start": v(68.5, 47) * mm, "end": v(63.5, 47) * mm});
            skLineSegment(sketch, "E3.12.9.3", {"start": v(63.5, 52) * mm, "end": v(63.5, 47) * mm});
            skPoint(sketch, "E3.12.9.4", {"position": v(66, 49.5) * mm});
            skLineSegment(sketch, "E3.12.10.0", {"start": v(68.5, 57.5) * mm, "end": v(63.5, 57.5) * mm});
            skLineSegment(sketch, "E3.12.10.1", {"start": v(68.5, 57.5) * mm, "end": v(68.5, 52.5) * mm});
            skLineSegment(sketch, "E3.12.10.2", {"start": v(68.5, 52.5) * mm, "end": v(63.5, 52.5) * mm});
            skLineSegment(sketch, "E3.12.10.3", {"start": v(63.5, 57.5) * mm, "end": v(63.5, 52.5) * mm});
            skPoint(sketch, "E3.12.10.4", {"position": v(66, 55) * mm});
            skLineSegment(sketch, "E3.12.11.0", {"start": v(68.5, 63) * mm, "end": v(63.5, 63) * mm});
            skLineSegment(sketch, "E3.12.11.1", {"start": v(68.5, 63) * mm, "end": v(68.5, 58) * mm});
            skLineSegment(sketch, "E3.12.11.2", {"start": v(68.5, 58) * mm, "end": v(63.5, 58) * mm});
            skLineSegment(sketch, "E3.12.11.3", {"start": v(63.5, 63) * mm, "end": v(63.5, 58) * mm});
            skPoint(sketch, "E3.12.11.4", {"position": v(66, 60.5) * mm});
            skLineSegment(sketch, "E3.12.12.0", {"start": v(68.5, 68.5) * mm, "end": v(63.5, 68.5) * mm});
            skLineSegment(sketch, "E3.12.12.1", {"start": v(68.5, 68.5) * mm, "end": v(68.5, 63.5) * mm});
            skLineSegment(sketch, "E3.12.12.2", {"start": v(68.5, 63.5) * mm, "end": v(63.5, 63.5) * mm});
            skLineSegment(sketch, "E3.12.12.3", {"start": v(63.5, 68.5) * mm, "end": v(63.5, 63.5) * mm});
            skPoint(sketch, "E3.12.12.4", {"position": v(66, 66) * mm});
            skLineSegment(sketch, "E3.12.13.0", {"start": v(68.5, 74) * mm, "end": v(63.5, 74) * mm});
            skLineSegment(sketch, "E3.12.13.1", {"start": v(68.5, 74) * mm, "end": v(68.5, 69) * mm});
            skLineSegment(sketch, "E3.12.13.2", {"start": v(68.5, 69) * mm, "end": v(63.5, 69) * mm});
            skLineSegment(sketch, "E3.12.13.3", {"start": v(63.5, 74) * mm, "end": v(63.5, 69) * mm});
            skPoint(sketch, "E3.12.13.4", {"position": v(66, 71.5) * mm});
            skLineSegment(sketch, "E3.12.14.0", {"start": v(68.5, 79.5) * mm, "end": v(63.5, 79.5) * mm});
            skLineSegment(sketch, "E3.12.14.1", {"start": v(68.5, 79.5) * mm, "end": v(68.5, 74.5) * mm});
            skLineSegment(sketch, "E3.12.14.2", {"start": v(68.5, 74.5) * mm, "end": v(63.5, 74.5) * mm});
            skLineSegment(sketch, "E3.12.14.3", {"start": v(63.5, 79.5) * mm, "end": v(63.5, 74.5) * mm});
            skPoint(sketch, "E3.12.14.4", {"position": v(66, 77) * mm});
            skLineSegment(sketch, "E3.12.15.0", {"start": v(68.5, 85) * mm, "end": v(63.5, 85) * mm});
            skLineSegment(sketch, "E3.12.15.1", {"start": v(68.5, 85) * mm, "end": v(68.5, 80) * mm});
            skLineSegment(sketch, "E3.12.15.2", {"start": v(68.5, 80) * mm, "end": v(63.5, 80) * mm});
            skLineSegment(sketch, "E3.12.15.3", {"start": v(63.5, 85) * mm, "end": v(63.5, 80) * mm});
            skPoint(sketch, "E3.12.15.4", {"position": v(66, 82.5) * mm});
            skLineSegment(sketch, "E3.12.16.0", {"start": v(68.5, 90.5) * mm, "end": v(63.5, 90.5) * mm});
            skLineSegment(sketch, "E3.12.16.1", {"start": v(68.5, 90.5) * mm, "end": v(68.5, 85.5) * mm});
            skLineSegment(sketch, "E3.12.16.2", {"start": v(68.5, 85.5) * mm, "end": v(63.5, 85.5) * mm});
            skLineSegment(sketch, "E3.12.16.3", {"start": v(63.5, 90.5) * mm, "end": v(63.5, 85.5) * mm});
            skPoint(sketch, "E3.12.16.4", {"position": v(66, 88) * mm});
            skLineSegment(sketch, "E3.12.17.0", {"start": v(68.5, 96) * mm, "end": v(63.5, 96) * mm});
            skLineSegment(sketch, "E3.12.17.1", {"start": v(68.5, 96) * mm, "end": v(68.5, 91) * mm});
            skLineSegment(sketch, "E3.12.17.2", {"start": v(68.5, 91) * mm, "end": v(63.5, 91) * mm});
            skLineSegment(sketch, "E3.12.17.3", {"start": v(63.5, 96) * mm, "end": v(63.5, 91) * mm});
            skPoint(sketch, "E3.12.17.4", {"position": v(66, 93.5) * mm});
            skLineSegment(sketch, "E3.12.18.0", {"start": v(68.5, 101.5) * mm, "end": v(63.5, 101.5) * mm});
            skLineSegment(sketch, "E3.12.18.1", {"start": v(68.5, 101.5) * mm, "end": v(68.5, 96.5) * mm});
            skLineSegment(sketch, "E3.12.18.2", {"start": v(68.5, 96.5) * mm, "end": v(63.5, 96.5) * mm});
            skLineSegment(sketch, "E3.12.18.3", {"start": v(63.5, 101.5) * mm, "end": v(63.5, 96.5) * mm});
            skPoint(sketch, "E3.12.18.4", {"position": v(66, 99) * mm});
            skLineSegment(sketch, "E3.12.19.0", {"start": v(68.5, 107) * mm, "end": v(63.5, 107) * mm});
            skLineSegment(sketch, "E3.12.19.1", {"start": v(68.5, 107) * mm, "end": v(68.5, 102) * mm});
            skLineSegment(sketch, "E3.12.19.2", {"start": v(68.5, 102) * mm, "end": v(63.5, 102) * mm});
            skLineSegment(sketch, "E3.12.19.3", {"start": v(63.5, 107) * mm, "end": v(63.5, 102) * mm});
            skPoint(sketch, "E3.12.19.4", {"position": v(66, 104.5) * mm});
            skLineSegment(sketch, "E3.12.20.0", {"start": v(68.5, 112.5) * mm, "end": v(63.5, 112.5) * mm});
            skLineSegment(sketch, "E3.12.20.1", {"start": v(68.5, 112.5) * mm, "end": v(68.5, 107.5) * mm});
            skLineSegment(sketch, "E3.12.20.2", {"start": v(68.5, 107.5) * mm, "end": v(63.5, 107.5) * mm});
            skLineSegment(sketch, "E3.12.20.3", {"start": v(63.5, 112.5) * mm, "end": v(63.5, 107.5) * mm});
            skPoint(sketch, "E3.12.20.4", {"position": v(66, 110) * mm});
            skLineSegment(sketch, "E3.12.21.0", {"start": v(68.5, 118) * mm, "end": v(63.5, 118) * mm});
            skLineSegment(sketch, "E3.12.21.1", {"start": v(68.5, 118) * mm, "end": v(68.5, 113) * mm});
            skLineSegment(sketch, "E3.12.21.2", {"start": v(68.5, 113) * mm, "end": v(63.5, 113) * mm});
            skLineSegment(sketch, "E3.12.21.3", {"start": v(63.5, 118) * mm, "end": v(63.5, 113) * mm});
            skPoint(sketch, "E3.12.21.4", {"position": v(66, 115.5) * mm});
            skLineSegment(sketch, "E3.12.22.0", {"start": v(68.5, 123.5) * mm, "end": v(63.5, 123.5) * mm});
            skLineSegment(sketch, "E3.12.22.1", {"start": v(68.5, 123.5) * mm, "end": v(68.5, 118.5) * mm});
            skLineSegment(sketch, "E3.12.22.2", {"start": v(68.5, 118.5) * mm, "end": v(63.5, 118.5) * mm});
            skLineSegment(sketch, "E3.12.22.3", {"start": v(63.5, 123.5) * mm, "end": v(63.5, 118.5) * mm});
            skPoint(sketch, "E3.12.22.4", {"position": v(66, 121) * mm});
            skLineSegment(sketch, "E3.12.23.0", {"start": v(68.5, 129) * mm, "end": v(63.5, 129) * mm});
            skLineSegment(sketch, "E3.12.23.1", {"start": v(68.5, 129) * mm, "end": v(68.5, 124) * mm});
            skLineSegment(sketch, "E3.12.23.2", {"start": v(68.5, 124) * mm, "end": v(63.5, 124) * mm});
            skLineSegment(sketch, "E3.12.23.3", {"start": v(63.5, 129) * mm, "end": v(63.5, 124) * mm});
            skPoint(sketch, "E3.12.23.4", {"position": v(66, 126.5) * mm});
            skLineSegment(sketch, "E3.12.24.0", {"start": v(68.5, 134.5) * mm, "end": v(63.5, 134.5) * mm});
            skLineSegment(sketch, "E3.12.24.1", {"start": v(68.5, 134.5) * mm, "end": v(68.5, 129.5) * mm});
            skLineSegment(sketch, "E3.12.24.2", {"start": v(68.5, 129.5) * mm, "end": v(63.5, 129.5) * mm});
            skLineSegment(sketch, "E3.12.24.3", {"start": v(63.5, 134.5) * mm, "end": v(63.5, 129.5) * mm});
            skPoint(sketch, "E3.12.24.4", {"position": v(66, 132) * mm});
            skLineSegment(sketch, "E3.13.0.0", {"start": v(74, 2.5) * mm, "end": v(69, 2.5) * mm});
            skLineSegment(sketch, "E3.13.0.1", {"start": v(74, 2.5) * mm, "end": v(74, -2.5) * mm});
            skLineSegment(sketch, "E3.13.0.2", {"start": v(74, -2.5) * mm, "end": v(69, -2.5) * mm});
            skLineSegment(sketch, "E3.13.0.3", {"start": v(69, 2.5) * mm, "end": v(69, -2.5) * mm});
            skPoint(sketch, "E3.13.0.4", {"position": v(71.5, 0) * mm});
            skLineSegment(sketch, "E3.13.1.0", {"start": v(74, 8) * mm, "end": v(69, 8) * mm});
            skLineSegment(sketch, "E3.13.1.1", {"start": v(74, 8) * mm, "end": v(74, 3) * mm});
            skLineSegment(sketch, "E3.13.1.2", {"start": v(74, 3) * mm, "end": v(69, 3) * mm});
            skLineSegment(sketch, "E3.13.1.3", {"start": v(69, 8) * mm, "end": v(69, 3) * mm});
            skPoint(sketch, "E3.13.1.4", {"position": v(71.5, 5.5) * mm});
            skLineSegment(sketch, "E3.13.2.0", {"start": v(74, 13.5) * mm, "end": v(69, 13.5) * mm});
            skLineSegment(sketch, "E3.13.2.1", {"start": v(74, 13.5) * mm, "end": v(74, 8.5) * mm});
            skLineSegment(sketch, "E3.13.2.2", {"start": v(74, 8.5) * mm, "end": v(69, 8.5) * mm});
            skLineSegment(sketch, "E3.13.2.3", {"start": v(69, 13.5) * mm, "end": v(69, 8.5) * mm});
            skPoint(sketch, "E3.13.2.4", {"position": v(71.5, 11) * mm});
            skLineSegment(sketch, "E3.13.3.0", {"start": v(74, 19) * mm, "end": v(69, 19) * mm});
            skLineSegment(sketch, "E3.13.3.1", {"start": v(74, 19) * mm, "end": v(74, 14) * mm});
            skLineSegment(sketch, "E3.13.3.2", {"start": v(74, 14) * mm, "end": v(69, 14) * mm});
            skLineSegment(sketch, "E3.13.3.3", {"start": v(69, 19) * mm, "end": v(69, 14) * mm});
            skPoint(sketch, "E3.13.3.4", {"position": v(71.5, 16.5) * mm});
            skLineSegment(sketch, "E3.13.4.0", {"start": v(74, 24.5) * mm, "end": v(69, 24.5) * mm});
            skLineSegment(sketch, "E3.13.4.1", {"start": v(74, 24.5) * mm, "end": v(74, 19.5) * mm});
            skLineSegment(sketch, "E3.13.4.2", {"start": v(74, 19.5) * mm, "end": v(69, 19.5) * mm});
            skLineSegment(sketch, "E3.13.4.3", {"start": v(69, 24.5) * mm, "end": v(69, 19.5) * mm});
            skPoint(sketch, "E3.13.4.4", {"position": v(71.5, 22) * mm});
            skLineSegment(sketch, "E3.13.5.0", {"start": v(74, 30) * mm, "end": v(69, 30) * mm});
            skLineSegment(sketch, "E3.13.5.1", {"start": v(74, 30) * mm, "end": v(74, 25) * mm});
            skLineSegment(sketch, "E3.13.5.2", {"start": v(74, 25) * mm, "end": v(69, 25) * mm});
            skLineSegment(sketch, "E3.13.5.3", {"start": v(69, 30) * mm, "end": v(69, 25) * mm});
            skPoint(sketch, "E3.13.5.4", {"position": v(71.5, 27.5) * mm});
            skLineSegment(sketch, "E3.13.6.0", {"start": v(74, 35.5) * mm, "end": v(69, 35.5) * mm});
            skLineSegment(sketch, "E3.13.6.1", {"start": v(74, 35.5) * mm, "end": v(74, 30.5) * mm});
            skLineSegment(sketch, "E3.13.6.2", {"start": v(74, 30.5) * mm, "end": v(69, 30.5) * mm});
            skLineSegment(sketch, "E3.13.6.3", {"start": v(69, 35.5) * mm, "end": v(69, 30.5) * mm});
            skPoint(sketch, "E3.13.6.4", {"position": v(71.5, 33) * mm});
            skLineSegment(sketch, "E3.13.7.0", {"start": v(74, 41) * mm, "end": v(69, 41) * mm});
            skLineSegment(sketch, "E3.13.7.1", {"start": v(74, 41) * mm, "end": v(74, 36) * mm});
            skLineSegment(sketch, "E3.13.7.2", {"start": v(74, 36) * mm, "end": v(69, 36) * mm});
            skLineSegment(sketch, "E3.13.7.3", {"start": v(69, 41) * mm, "end": v(69, 36) * mm});
            skPoint(sketch, "E3.13.7.4", {"position": v(71.5, 38.5) * mm});
            skLineSegment(sketch, "E3.13.8.0", {"start": v(74, 46.5) * mm, "end": v(69, 46.5) * mm});
            skLineSegment(sketch, "E3.13.8.1", {"start": v(74, 46.5) * mm, "end": v(74, 41.5) * mm});
            skLineSegment(sketch, "E3.13.8.2", {"start": v(74, 41.5) * mm, "end": v(69, 41.5) * mm});
            skLineSegment(sketch, "E3.13.8.3", {"start": v(69, 46.5) * mm, "end": v(69, 41.5) * mm});
            skPoint(sketch, "E3.13.8.4", {"position": v(71.5, 44) * mm});
            skLineSegment(sketch, "E3.13.9.0", {"start": v(74, 52) * mm, "end": v(69, 52) * mm});
            skLineSegment(sketch, "E3.13.9.1", {"start": v(74, 52) * mm, "end": v(74, 47) * mm});
            skLineSegment(sketch, "E3.13.9.2", {"start": v(74, 47) * mm, "end": v(69, 47) * mm});
            skLineSegment(sketch, "E3.13.9.3", {"start": v(69, 52) * mm, "end": v(69, 47) * mm});
            skPoint(sketch, "E3.13.9.4", {"position": v(71.5, 49.5) * mm});
            skLineSegment(sketch, "E3.13.10.0", {"start": v(74, 57.5) * mm, "end": v(69, 57.5) * mm});
            skLineSegment(sketch, "E3.13.10.1", {"start": v(74, 57.5) * mm, "end": v(74, 52.5) * mm});
            skLineSegment(sketch, "E3.13.10.2", {"start": v(74, 52.5) * mm, "end": v(69, 52.5) * mm});
            skLineSegment(sketch, "E3.13.10.3", {"start": v(69, 57.5) * mm, "end": v(69, 52.5) * mm});
            skPoint(sketch, "E3.13.10.4", {"position": v(71.5, 55) * mm});
            skLineSegment(sketch, "E3.13.11.0", {"start": v(74, 63) * mm, "end": v(69, 63) * mm});
            skLineSegment(sketch, "E3.13.11.1", {"start": v(74, 63) * mm, "end": v(74, 58) * mm});
            skLineSegment(sketch, "E3.13.11.2", {"start": v(74, 58) * mm, "end": v(69, 58) * mm});
            skLineSegment(sketch, "E3.13.11.3", {"start": v(69, 63) * mm, "end": v(69, 58) * mm});
            skPoint(sketch, "E3.13.11.4", {"position": v(71.5, 60.5) * mm});
            skLineSegment(sketch, "E3.13.12.0", {"start": v(74, 68.5) * mm, "end": v(69, 68.5) * mm});
            skLineSegment(sketch, "E3.13.12.1", {"start": v(74, 68.5) * mm, "end": v(74, 63.5) * mm});
            skLineSegment(sketch, "E3.13.12.2", {"start": v(74, 63.5) * mm, "end": v(69, 63.5) * mm});
            skLineSegment(sketch, "E3.13.12.3", {"start": v(69, 68.5) * mm, "end": v(69, 63.5) * mm});
            skPoint(sketch, "E3.13.12.4", {"position": v(71.5, 66) * mm});
            skLineSegment(sketch, "E3.13.13.0", {"start": v(74, 74) * mm, "end": v(69, 74) * mm});
            skLineSegment(sketch, "E3.13.13.1", {"start": v(74, 74) * mm, "end": v(74, 69) * mm});
            skLineSegment(sketch, "E3.13.13.2", {"start": v(74, 69) * mm, "end": v(69, 69) * mm});
            skLineSegment(sketch, "E3.13.13.3", {"start": v(69, 74) * mm, "end": v(69, 69) * mm});
            skPoint(sketch, "E3.13.13.4", {"position": v(71.5, 71.5) * mm});
            skLineSegment(sketch, "E3.13.14.0", {"start": v(74, 79.5) * mm, "end": v(69, 79.5) * mm});
            skLineSegment(sketch, "E3.13.14.1", {"start": v(74, 79.5) * mm, "end": v(74, 74.5) * mm});
            skLineSegment(sketch, "E3.13.14.2", {"start": v(74, 74.5) * mm, "end": v(69, 74.5) * mm});
            skLineSegment(sketch, "E3.13.14.3", {"start": v(69, 79.5) * mm, "end": v(69, 74.5) * mm});
            skPoint(sketch, "E3.13.14.4", {"position": v(71.5, 77) * mm});
            skLineSegment(sketch, "E3.13.15.0", {"start": v(74, 85) * mm, "end": v(69, 85) * mm});
            skLineSegment(sketch, "E3.13.15.1", {"start": v(74, 85) * mm, "end": v(74, 80) * mm});
            skLineSegment(sketch, "E3.13.15.2", {"start": v(74, 80) * mm, "end": v(69, 80) * mm});
            skLineSegment(sketch, "E3.13.15.3", {"start": v(69, 85) * mm, "end": v(69, 80) * mm});
            skPoint(sketch, "E3.13.15.4", {"position": v(71.5, 82.5) * mm});
            skLineSegment(sketch, "E3.13.16.0", {"start": v(74, 90.5) * mm, "end": v(69, 90.5) * mm});
            skLineSegment(sketch, "E3.13.16.1", {"start": v(74, 90.5) * mm, "end": v(74, 85.5) * mm});
            skLineSegment(sketch, "E3.13.16.2", {"start": v(74, 85.5) * mm, "end": v(69, 85.5) * mm});
            skLineSegment(sketch, "E3.13.16.3", {"start": v(69, 90.5) * mm, "end": v(69, 85.5) * mm});
            skPoint(sketch, "E3.13.16.4", {"position": v(71.5, 88) * mm});
            skLineSegment(sketch, "E3.13.17.0", {"start": v(74, 96) * mm, "end": v(69, 96) * mm});
            skLineSegment(sketch, "E3.13.17.1", {"start": v(74, 96) * mm, "end": v(74, 91) * mm});
            skLineSegment(sketch, "E3.13.17.2", {"start": v(74, 91) * mm, "end": v(69, 91) * mm});
            skLineSegment(sketch, "E3.13.17.3", {"start": v(69, 96) * mm, "end": v(69, 91) * mm});
            skPoint(sketch, "E3.13.17.4", {"position": v(71.5, 93.5) * mm});
            skLineSegment(sketch, "E3.13.18.0", {"start": v(74, 101.5) * mm, "end": v(69, 101.5) * mm});
            skLineSegment(sketch, "E3.13.18.1", {"start": v(74, 101.5) * mm, "end": v(74, 96.5) * mm});
            skLineSegment(sketch, "E3.13.18.2", {"start": v(74, 96.5) * mm, "end": v(69, 96.5) * mm});
            skLineSegment(sketch, "E3.13.18.3", {"start": v(69, 101.5) * mm, "end": v(69, 96.5) * mm});
            skPoint(sketch, "E3.13.18.4", {"position": v(71.5, 99) * mm});
            skLineSegment(sketch, "E3.13.19.0", {"start": v(74, 107) * mm, "end": v(69, 107) * mm});
            skLineSegment(sketch, "E3.13.19.1", {"start": v(74, 107) * mm, "end": v(74, 102) * mm});
            skLineSegment(sketch, "E3.13.19.2", {"start": v(74, 102) * mm, "end": v(69, 102) * mm});
            skLineSegment(sketch, "E3.13.19.3", {"start": v(69, 107) * mm, "end": v(69, 102) * mm});
            skPoint(sketch, "E3.13.19.4", {"position": v(71.5, 104.5) * mm});
            skLineSegment(sketch, "E3.13.20.0", {"start": v(74, 112.5) * mm, "end": v(69, 112.5) * mm});
            skLineSegment(sketch, "E3.13.20.1", {"start": v(74, 112.5) * mm, "end": v(74, 107.5) * mm});
            skLineSegment(sketch, "E3.13.20.2", {"start": v(74, 107.5) * mm, "end": v(69, 107.5) * mm});
            skLineSegment(sketch, "E3.13.20.3", {"start": v(69, 112.5) * mm, "end": v(69, 107.5) * mm});
            skPoint(sketch, "E3.13.20.4", {"position": v(71.5, 110) * mm});
            skLineSegment(sketch, "E3.13.21.0", {"start": v(74, 118) * mm, "end": v(69, 118) * mm});
            skLineSegment(sketch, "E3.13.21.1", {"start": v(74, 118) * mm, "end": v(74, 113) * mm});
            skLineSegment(sketch, "E3.13.21.2", {"start": v(74, 113) * mm, "end": v(69, 113) * mm});
            skLineSegment(sketch, "E3.13.21.3", {"start": v(69, 118) * mm, "end": v(69, 113) * mm});
            skPoint(sketch, "E3.13.21.4", {"position": v(71.5, 115.5) * mm});
            skLineSegment(sketch, "E3.13.22.0", {"start": v(74, 123.5) * mm, "end": v(69, 123.5) * mm});
            skLineSegment(sketch, "E3.13.22.1", {"start": v(74, 123.5) * mm, "end": v(74, 118.5) * mm});
            skLineSegment(sketch, "E3.13.22.2", {"start": v(74, 118.5) * mm, "end": v(69, 118.5) * mm});
            skLineSegment(sketch, "E3.13.22.3", {"start": v(69, 123.5) * mm, "end": v(69, 118.5) * mm});
            skPoint(sketch, "E3.13.22.4", {"position": v(71.5, 121) * mm});
            skLineSegment(sketch, "E3.13.23.0", {"start": v(74, 129) * mm, "end": v(69, 129) * mm});
            skLineSegment(sketch, "E3.13.23.1", {"start": v(74, 129) * mm, "end": v(74, 124) * mm});
            skLineSegment(sketch, "E3.13.23.2", {"start": v(74, 124) * mm, "end": v(69, 124) * mm});
            skLineSegment(sketch, "E3.13.23.3", {"start": v(69, 129) * mm, "end": v(69, 124) * mm});
            skPoint(sketch, "E3.13.23.4", {"position": v(71.5, 126.5) * mm});
            skLineSegment(sketch, "E3.13.24.0", {"start": v(74, 134.5) * mm, "end": v(69, 134.5) * mm});
            skLineSegment(sketch, "E3.13.24.1", {"start": v(74, 134.5) * mm, "end": v(74, 129.5) * mm});
            skLineSegment(sketch, "E3.13.24.2", {"start": v(74, 129.5) * mm, "end": v(69, 129.5) * mm});
            skLineSegment(sketch, "E3.13.24.3", {"start": v(69, 134.5) * mm, "end": v(69, 129.5) * mm});
            skPoint(sketch, "E3.13.24.4", {"position": v(71.5, 132) * mm});
            skLineSegment(sketch, "E3.14.0.0", {"start": v(79.5, 2.5) * mm, "end": v(74.5, 2.5) * mm});
            skLineSegment(sketch, "E3.14.0.1", {"start": v(79.5, 2.5) * mm, "end": v(79.5, -2.5) * mm});
            skLineSegment(sketch, "E3.14.0.2", {"start": v(79.5, -2.5) * mm, "end": v(74.5, -2.5) * mm});
            skLineSegment(sketch, "E3.14.0.3", {"start": v(74.5, 2.5) * mm, "end": v(74.5, -2.5) * mm});
            skPoint(sketch, "E3.14.0.4", {"position": v(77, 0) * mm});
            skLineSegment(sketch, "E3.14.1.0", {"start": v(79.5, 8) * mm, "end": v(74.5, 8) * mm});
            skLineSegment(sketch, "E3.14.1.1", {"start": v(79.5, 8) * mm, "end": v(79.5, 3) * mm});
            skLineSegment(sketch, "E3.14.1.2", {"start": v(79.5, 3) * mm, "end": v(74.5, 3) * mm});
            skLineSegment(sketch, "E3.14.1.3", {"start": v(74.5, 8) * mm, "end": v(74.5, 3) * mm});
            skPoint(sketch, "E3.14.1.4", {"position": v(77, 5.5) * mm});
            skLineSegment(sketch, "E3.14.2.0", {"start": v(79.5, 13.5) * mm, "end": v(74.5, 13.5) * mm});
            skLineSegment(sketch, "E3.14.2.1", {"start": v(79.5, 13.5) * mm, "end": v(79.5, 8.5) * mm});
            skLineSegment(sketch, "E3.14.2.2", {"start": v(79.5, 8.5) * mm, "end": v(74.5, 8.5) * mm});
            skLineSegment(sketch, "E3.14.2.3", {"start": v(74.5, 13.5) * mm, "end": v(74.5, 8.5) * mm});
            skPoint(sketch, "E3.14.2.4", {"position": v(77, 11) * mm});
            skLineSegment(sketch, "E3.14.3.0", {"start": v(79.5, 19) * mm, "end": v(74.5, 19) * mm});
            skLineSegment(sketch, "E3.14.3.1", {"start": v(79.5, 19) * mm, "end": v(79.5, 14) * mm});
            skLineSegment(sketch, "E3.14.3.2", {"start": v(79.5, 14) * mm, "end": v(74.5, 14) * mm});
            skLineSegment(sketch, "E3.14.3.3", {"start": v(74.5, 19) * mm, "end": v(74.5, 14) * mm});
            skPoint(sketch, "E3.14.3.4", {"position": v(77, 16.5) * mm});
            skLineSegment(sketch, "E3.14.4.0", {"start": v(79.5, 24.5) * mm, "end": v(74.5, 24.5) * mm});
            skLineSegment(sketch, "E3.14.4.1", {"start": v(79.5, 24.5) * mm, "end": v(79.5, 19.5) * mm});
            skLineSegment(sketch, "E3.14.4.2", {"start": v(79.5, 19.5) * mm, "end": v(74.5, 19.5) * mm});
            skLineSegment(sketch, "E3.14.4.3", {"start": v(74.5, 24.5) * mm, "end": v(74.5, 19.5) * mm});
            skPoint(sketch, "E3.14.4.4", {"position": v(77, 22) * mm});
            skLineSegment(sketch, "E3.14.5.0", {"start": v(79.5, 30) * mm, "end": v(74.5, 30) * mm});
            skLineSegment(sketch, "E3.14.5.1", {"start": v(79.5, 30) * mm, "end": v(79.5, 25) * mm});
            skLineSegment(sketch, "E3.14.5.2", {"start": v(79.5, 25) * mm, "end": v(74.5, 25) * mm});
            skLineSegment(sketch, "E3.14.5.3", {"start": v(74.5, 30) * mm, "end": v(74.5, 25) * mm});
            skPoint(sketch, "E3.14.5.4", {"position": v(77, 27.5) * mm});
            skLineSegment(sketch, "E3.14.6.0", {"start": v(79.5, 35.5) * mm, "end": v(74.5, 35.5) * mm});
            skLineSegment(sketch, "E3.14.6.1", {"start": v(79.5, 35.5) * mm, "end": v(79.5, 30.5) * mm});
            skLineSegment(sketch, "E3.14.6.2", {"start": v(79.5, 30.5) * mm, "end": v(74.5, 30.5) * mm});
            skLineSegment(sketch, "E3.14.6.3", {"start": v(74.5, 35.5) * mm, "end": v(74.5, 30.5) * mm});
            skPoint(sketch, "E3.14.6.4", {"position": v(77, 33) * mm});
            skLineSegment(sketch, "E3.14.7.0", {"start": v(79.5, 41) * mm, "end": v(74.5, 41) * mm});
            skLineSegment(sketch, "E3.14.7.1", {"start": v(79.5, 41) * mm, "end": v(79.5, 36) * mm});
            skLineSegment(sketch, "E3.14.7.2", {"start": v(79.5, 36) * mm, "end": v(74.5, 36) * mm});
            skLineSegment(sketch, "E3.14.7.3", {"start": v(74.5, 41) * mm, "end": v(74.5, 36) * mm});
            skPoint(sketch, "E3.14.7.4", {"position": v(77, 38.5) * mm});
            skLineSegment(sketch, "E3.14.8.0", {"start": v(79.5, 46.5) * mm, "end": v(74.5, 46.5) * mm});
            skLineSegment(sketch, "E3.14.8.1", {"start": v(79.5, 46.5) * mm, "end": v(79.5, 41.5) * mm});
            skLineSegment(sketch, "E3.14.8.2", {"start": v(79.5, 41.5) * mm, "end": v(74.5, 41.5) * mm});
            skLineSegment(sketch, "E3.14.8.3", {"start": v(74.5, 46.5) * mm, "end": v(74.5, 41.5) * mm});
            skPoint(sketch, "E3.14.8.4", {"position": v(77, 44) * mm});
            skLineSegment(sketch, "E3.14.9.0", {"start": v(79.5, 52) * mm, "end": v(74.5, 52) * mm});
            skLineSegment(sketch, "E3.14.9.1", {"start": v(79.5, 52) * mm, "end": v(79.5, 47) * mm});
            skLineSegment(sketch, "E3.14.9.2", {"start": v(79.5, 47) * mm, "end": v(74.5, 47) * mm});
            skLineSegment(sketch, "E3.14.9.3", {"start": v(74.5, 52) * mm, "end": v(74.5, 47) * mm});
            skPoint(sketch, "E3.14.9.4", {"position": v(77, 49.5) * mm});
            skLineSegment(sketch, "E3.14.10.0", {"start": v(79.5, 57.5) * mm, "end": v(74.5, 57.5) * mm});
            skLineSegment(sketch, "E3.14.10.1", {"start": v(79.5, 57.5) * mm, "end": v(79.5, 52.5) * mm});
            skLineSegment(sketch, "E3.14.10.2", {"start": v(79.5, 52.5) * mm, "end": v(74.5, 52.5) * mm});
            skLineSegment(sketch, "E3.14.10.3", {"start": v(74.5, 57.5) * mm, "end": v(74.5, 52.5) * mm});
            skPoint(sketch, "E3.14.10.4", {"position": v(77, 55) * mm});
            skLineSegment(sketch, "E3.14.11.0", {"start": v(79.5, 63) * mm, "end": v(74.5, 63) * mm});
            skLineSegment(sketch, "E3.14.11.1", {"start": v(79.5, 63) * mm, "end": v(79.5, 58) * mm});
            skLineSegment(sketch, "E3.14.11.2", {"start": v(79.5, 58) * mm, "end": v(74.5, 58) * mm});
            skLineSegment(sketch, "E3.14.11.3", {"start": v(74.5, 63) * mm, "end": v(74.5, 58) * mm});
            skPoint(sketch, "E3.14.11.4", {"position": v(77, 60.5) * mm});
            skLineSegment(sketch, "E3.14.12.0", {"start": v(79.5, 68.5) * mm, "end": v(74.5, 68.5) * mm});
            skLineSegment(sketch, "E3.14.12.1", {"start": v(79.5, 68.5) * mm, "end": v(79.5, 63.5) * mm});
            skLineSegment(sketch, "E3.14.12.2", {"start": v(79.5, 63.5) * mm, "end": v(74.5, 63.5) * mm});
            skLineSegment(sketch, "E3.14.12.3", {"start": v(74.5, 68.5) * mm, "end": v(74.5, 63.5) * mm});
            skPoint(sketch, "E3.14.12.4", {"position": v(77, 66) * mm});
            skLineSegment(sketch, "E3.14.13.0", {"start": v(79.5, 74) * mm, "end": v(74.5, 74) * mm});
            skLineSegment(sketch, "E3.14.13.1", {"start": v(79.5, 74) * mm, "end": v(79.5, 69) * mm});
            skLineSegment(sketch, "E3.14.13.2", {"start": v(79.5, 69) * mm, "end": v(74.5, 69) * mm});
            skLineSegment(sketch, "E3.14.13.3", {"start": v(74.5, 74) * mm, "end": v(74.5, 69) * mm});
            skPoint(sketch, "E3.14.13.4", {"position": v(77, 71.5) * mm});
            skLineSegment(sketch, "E3.14.14.0", {"start": v(79.5, 79.5) * mm, "end": v(74.5, 79.5) * mm});
            skLineSegment(sketch, "E3.14.14.1", {"start": v(79.5, 79.5) * mm, "end": v(79.5, 74.5) * mm});
            skLineSegment(sketch, "E3.14.14.2", {"start": v(79.5, 74.5) * mm, "end": v(74.5, 74.5) * mm});
            skLineSegment(sketch, "E3.14.14.3", {"start": v(74.5, 79.5) * mm, "end": v(74.5, 74.5) * mm});
            skPoint(sketch, "E3.14.14.4", {"position": v(77, 77) * mm});
            skLineSegment(sketch, "E3.14.15.0", {"start": v(79.5, 85) * mm, "end": v(74.5, 85) * mm});
            skLineSegment(sketch, "E3.14.15.1", {"start": v(79.5, 85) * mm, "end": v(79.5, 80) * mm});
            skLineSegment(sketch, "E3.14.15.2", {"start": v(79.5, 80) * mm, "end": v(74.5, 80) * mm});
            skLineSegment(sketch, "E3.14.15.3", {"start": v(74.5, 85) * mm, "end": v(74.5, 80) * mm});
            skPoint(sketch, "E3.14.15.4", {"position": v(77, 82.5) * mm});
            skLineSegment(sketch, "E3.14.16.0", {"start": v(79.5, 90.5) * mm, "end": v(74.5, 90.5) * mm});
            skLineSegment(sketch, "E3.14.16.1", {"start": v(79.5, 90.5) * mm, "end": v(79.5, 85.5) * mm});
            skLineSegment(sketch, "E3.14.16.2", {"start": v(79.5, 85.5) * mm, "end": v(74.5, 85.5) * mm});
            skLineSegment(sketch, "E3.14.16.3", {"start": v(74.5, 90.5) * mm, "end": v(74.5, 85.5) * mm});
            skPoint(sketch, "E3.14.16.4", {"position": v(77, 88) * mm});
            skLineSegment(sketch, "E3.14.17.0", {"start": v(79.5, 96) * mm, "end": v(74.5, 96) * mm});
            skLineSegment(sketch, "E3.14.17.1", {"start": v(79.5, 96) * mm, "end": v(79.5, 91) * mm});
            skLineSegment(sketch, "E3.14.17.2", {"start": v(79.5, 91) * mm, "end": v(74.5, 91) * mm});
            skLineSegment(sketch, "E3.14.17.3", {"start": v(74.5, 96) * mm, "end": v(74.5, 91) * mm});
            skPoint(sketch, "E3.14.17.4", {"position": v(77, 93.5) * mm});
            skLineSegment(sketch, "E3.14.18.0", {"start": v(79.5, 101.5) * mm, "end": v(74.5, 101.5) * mm});
            skLineSegment(sketch, "E3.14.18.1", {"start": v(79.5, 101.5) * mm, "end": v(79.5, 96.5) * mm});
            skLineSegment(sketch, "E3.14.18.2", {"start": v(79.5, 96.5) * mm, "end": v(74.5, 96.5) * mm});
            skLineSegment(sketch, "E3.14.18.3", {"start": v(74.5, 101.5) * mm, "end": v(74.5, 96.5) * mm});
            skPoint(sketch, "E3.14.18.4", {"position": v(77, 99) * mm});
            skLineSegment(sketch, "E3.14.19.0", {"start": v(79.5, 107) * mm, "end": v(74.5, 107) * mm});
            skLineSegment(sketch, "E3.14.19.1", {"start": v(79.5, 107) * mm, "end": v(79.5, 102) * mm});
            skLineSegment(sketch, "E3.14.19.2", {"start": v(79.5, 102) * mm, "end": v(74.5, 102) * mm});
            skLineSegment(sketch, "E3.14.19.3", {"start": v(74.5, 107) * mm, "end": v(74.5, 102) * mm});
            skPoint(sketch, "E3.14.19.4", {"position": v(77, 104.5) * mm});
            skLineSegment(sketch, "E3.14.20.0", {"start": v(79.5, 112.5) * mm, "end": v(74.5, 112.5) * mm});
            skLineSegment(sketch, "E3.14.20.1", {"start": v(79.5, 112.5) * mm, "end": v(79.5, 107.5) * mm});
            skLineSegment(sketch, "E3.14.20.2", {"start": v(79.5, 107.5) * mm, "end": v(74.5, 107.5) * mm});
            skLineSegment(sketch, "E3.14.20.3", {"start": v(74.5, 112.5) * mm, "end": v(74.5, 107.5) * mm});
            skPoint(sketch, "E3.14.20.4", {"position": v(77, 110) * mm});
            skLineSegment(sketch, "E3.14.21.0", {"start": v(79.5, 118) * mm, "end": v(74.5, 118) * mm});
            skLineSegment(sketch, "E3.14.21.1", {"start": v(79.5, 118) * mm, "end": v(79.5, 113) * mm});
            skLineSegment(sketch, "E3.14.21.2", {"start": v(79.5, 113) * mm, "end": v(74.5, 113) * mm});
            skLineSegment(sketch, "E3.14.21.3", {"start": v(74.5, 118) * mm, "end": v(74.5, 113) * mm});
            skPoint(sketch, "E3.14.21.4", {"position": v(77, 115.5) * mm});
            skLineSegment(sketch, "E3.14.22.0", {"start": v(79.5, 123.5) * mm, "end": v(74.5, 123.5) * mm});
            skLineSegment(sketch, "E3.14.22.1", {"start": v(79.5, 123.5) * mm, "end": v(79.5, 118.5) * mm});
            skLineSegment(sketch, "E3.14.22.2", {"start": v(79.5, 118.5) * mm, "end": v(74.5, 118.5) * mm});
            skLineSegment(sketch, "E3.14.22.3", {"start": v(74.5, 123.5) * mm, "end": v(74.5, 118.5) * mm});
            skPoint(sketch, "E3.14.22.4", {"position": v(77, 121) * mm});
            skLineSegment(sketch, "E3.14.23.0", {"start": v(79.5, 129) * mm, "end": v(74.5, 129) * mm});
            skLineSegment(sketch, "E3.14.23.1", {"start": v(79.5, 129) * mm, "end": v(79.5, 124) * mm});
            skLineSegment(sketch, "E3.14.23.2", {"start": v(79.5, 124) * mm, "end": v(74.5, 124) * mm});
            skLineSegment(sketch, "E3.14.23.3", {"start": v(74.5, 129) * mm, "end": v(74.5, 124) * mm});
            skPoint(sketch, "E3.14.23.4", {"position": v(77, 126.5) * mm});
            skLineSegment(sketch, "E3.14.24.0", {"start": v(79.5, 134.5) * mm, "end": v(74.5, 134.5) * mm});
            skLineSegment(sketch, "E3.14.24.1", {"start": v(79.5, 134.5) * mm, "end": v(79.5, 129.5) * mm});
            skLineSegment(sketch, "E3.14.24.2", {"start": v(79.5, 129.5) * mm, "end": v(74.5, 129.5) * mm});
            skLineSegment(sketch, "E3.14.24.3", {"start": v(74.5, 134.5) * mm, "end": v(74.5, 129.5) * mm});
            skPoint(sketch, "E3.14.24.4", {"position": v(77, 132) * mm});
            skLineSegment(sketch, "E3.15.0.0", {"start": v(85, 2.5) * mm, "end": v(80, 2.5) * mm});
            skLineSegment(sketch, "E3.15.0.1", {"start": v(85, 2.5) * mm, "end": v(85, -2.5) * mm});
            skLineSegment(sketch, "E3.15.0.2", {"start": v(85, -2.5) * mm, "end": v(80, -2.5) * mm});
            skLineSegment(sketch, "E3.15.0.3", {"start": v(80, 2.5) * mm, "end": v(80, -2.5) * mm});
            skPoint(sketch, "E3.15.0.4", {"position": v(82.5, 0) * mm});
            skLineSegment(sketch, "E3.15.1.0", {"start": v(85, 8) * mm, "end": v(80, 8) * mm});
            skLineSegment(sketch, "E3.15.1.1", {"start": v(85, 8) * mm, "end": v(85, 3) * mm});
            skLineSegment(sketch, "E3.15.1.2", {"start": v(85, 3) * mm, "end": v(80, 3) * mm});
            skLineSegment(sketch, "E3.15.1.3", {"start": v(80, 8) * mm, "end": v(80, 3) * mm});
            skPoint(sketch, "E3.15.1.4", {"position": v(82.5, 5.5) * mm});
            skLineSegment(sketch, "E3.15.2.0", {"start": v(85, 13.5) * mm, "end": v(80, 13.5) * mm});
            skLineSegment(sketch, "E3.15.2.1", {"start": v(85, 13.5) * mm, "end": v(85, 8.5) * mm});
            skLineSegment(sketch, "E3.15.2.2", {"start": v(85, 8.5) * mm, "end": v(80, 8.5) * mm});
            skLineSegment(sketch, "E3.15.2.3", {"start": v(80, 13.5) * mm, "end": v(80, 8.5) * mm});
            skPoint(sketch, "E3.15.2.4", {"position": v(82.5, 11) * mm});
            skLineSegment(sketch, "E3.15.3.0", {"start": v(85, 19) * mm, "end": v(80, 19) * mm});
            skLineSegment(sketch, "E3.15.3.1", {"start": v(85, 19) * mm, "end": v(85, 14) * mm});
            skLineSegment(sketch, "E3.15.3.2", {"start": v(85, 14) * mm, "end": v(80, 14) * mm});
            skLineSegment(sketch, "E3.15.3.3", {"start": v(80, 19) * mm, "end": v(80, 14) * mm});
            skPoint(sketch, "E3.15.3.4", {"position": v(82.5, 16.5) * mm});
            skLineSegment(sketch, "E3.15.4.0", {"start": v(85, 24.5) * mm, "end": v(80, 24.5) * mm});
            skLineSegment(sketch, "E3.15.4.1", {"start": v(85, 24.5) * mm, "end": v(85, 19.5) * mm});
            skLineSegment(sketch, "E3.15.4.2", {"start": v(85, 19.5) * mm, "end": v(80, 19.5) * mm});
            skLineSegment(sketch, "E3.15.4.3", {"start": v(80, 24.5) * mm, "end": v(80, 19.5) * mm});
            skPoint(sketch, "E3.15.4.4", {"position": v(82.5, 22) * mm});
            skLineSegment(sketch, "E3.15.5.0", {"start": v(85, 30) * mm, "end": v(80, 30) * mm});
            skLineSegment(sketch, "E3.15.5.1", {"start": v(85, 30) * mm, "end": v(85, 25) * mm});
            skLineSegment(sketch, "E3.15.5.2", {"start": v(85, 25) * mm, "end": v(80, 25) * mm});
            skLineSegment(sketch, "E3.15.5.3", {"start": v(80, 30) * mm, "end": v(80, 25) * mm});
            skPoint(sketch, "E3.15.5.4", {"position": v(82.5, 27.5) * mm});
            skLineSegment(sketch, "E3.15.6.0", {"start": v(85, 35.5) * mm, "end": v(80, 35.5) * mm});
            skLineSegment(sketch, "E3.15.6.1", {"start": v(85, 35.5) * mm, "end": v(85, 30.5) * mm});
            skLineSegment(sketch, "E3.15.6.2", {"start": v(85, 30.5) * mm, "end": v(80, 30.5) * mm});
            skLineSegment(sketch, "E3.15.6.3", {"start": v(80, 35.5) * mm, "end": v(80, 30.5) * mm});
            skPoint(sketch, "E3.15.6.4", {"position": v(82.5, 33) * mm});
            skLineSegment(sketch, "E3.15.7.0", {"start": v(85, 41) * mm, "end": v(80, 41) * mm});
            skLineSegment(sketch, "E3.15.7.1", {"start": v(85, 41) * mm, "end": v(85, 36) * mm});
            skLineSegment(sketch, "E3.15.7.2", {"start": v(85, 36) * mm, "end": v(80, 36) * mm});
            skLineSegment(sketch, "E3.15.7.3", {"start": v(80, 41) * mm, "end": v(80, 36) * mm});
            skPoint(sketch, "E3.15.7.4", {"position": v(82.5, 38.5) * mm});
            skLineSegment(sketch, "E3.15.8.0", {"start": v(85, 46.5) * mm, "end": v(80, 46.5) * mm});
            skLineSegment(sketch, "E3.15.8.1", {"start": v(85, 46.5) * mm, "end": v(85, 41.5) * mm});
            skLineSegment(sketch, "E3.15.8.2", {"start": v(85, 41.5) * mm, "end": v(80, 41.5) * mm});
            skLineSegment(sketch, "E3.15.8.3", {"start": v(80, 46.5) * mm, "end": v(80, 41.5) * mm});
            skPoint(sketch, "E3.15.8.4", {"position": v(82.5, 44) * mm});
            skLineSegment(sketch, "E3.15.9.0", {"start": v(85, 52) * mm, "end": v(80, 52) * mm});
            skLineSegment(sketch, "E3.15.9.1", {"start": v(85, 52) * mm, "end": v(85, 47) * mm});
            skLineSegment(sketch, "E3.15.9.2", {"start": v(85, 47) * mm, "end": v(80, 47) * mm});
            skLineSegment(sketch, "E3.15.9.3", {"start": v(80, 52) * mm, "end": v(80, 47) * mm});
            skPoint(sketch, "E3.15.9.4", {"position": v(82.5, 49.5) * mm});
            skLineSegment(sketch, "E3.15.10.0", {"start": v(85, 57.5) * mm, "end": v(80, 57.5) * mm});
            skLineSegment(sketch, "E3.15.10.1", {"start": v(85, 57.5) * mm, "end": v(85, 52.5) * mm});
            skLineSegment(sketch, "E3.15.10.2", {"start": v(85, 52.5) * mm, "end": v(80, 52.5) * mm});
            skLineSegment(sketch, "E3.15.10.3", {"start": v(80, 57.5) * mm, "end": v(80, 52.5) * mm});
            skPoint(sketch, "E3.15.10.4", {"position": v(82.5, 55) * mm});
            skLineSegment(sketch, "E3.15.11.0", {"start": v(85, 63) * mm, "end": v(80, 63) * mm});
            skLineSegment(sketch, "E3.15.11.1", {"start": v(85, 63) * mm, "end": v(85, 58) * mm});
            skLineSegment(sketch, "E3.15.11.2", {"start": v(85, 58) * mm, "end": v(80, 58) * mm});
            skLineSegment(sketch, "E3.15.11.3", {"start": v(80, 63) * mm, "end": v(80, 58) * mm});
            skPoint(sketch, "E3.15.11.4", {"position": v(82.5, 60.5) * mm});
            skLineSegment(sketch, "E3.15.12.0", {"start": v(85, 68.5) * mm, "end": v(80, 68.5) * mm});
            skLineSegment(sketch, "E3.15.12.1", {"start": v(85, 68.5) * mm, "end": v(85, 63.5) * mm});
            skLineSegment(sketch, "E3.15.12.2", {"start": v(85, 63.5) * mm, "end": v(80, 63.5) * mm});
            skLineSegment(sketch, "E3.15.12.3", {"start": v(80, 68.5) * mm, "end": v(80, 63.5) * mm});
            skPoint(sketch, "E3.15.12.4", {"position": v(82.5, 66) * mm});
            skLineSegment(sketch, "E3.15.13.0", {"start": v(85, 74) * mm, "end": v(80, 74) * mm});
            skLineSegment(sketch, "E3.15.13.1", {"start": v(85, 74) * mm, "end": v(85, 69) * mm});
            skLineSegment(sketch, "E3.15.13.2", {"start": v(85, 69) * mm, "end": v(80, 69) * mm});
            skLineSegment(sketch, "E3.15.13.3", {"start": v(80, 74) * mm, "end": v(80, 69) * mm});
            skPoint(sketch, "E3.15.13.4", {"position": v(82.5, 71.5) * mm});
            skLineSegment(sketch, "E3.15.14.0", {"start": v(85, 79.5) * mm, "end": v(80, 79.5) * mm});
            skLineSegment(sketch, "E3.15.14.1", {"start": v(85, 79.5) * mm, "end": v(85, 74.5) * mm});
            skLineSegment(sketch, "E3.15.14.2", {"start": v(85, 74.5) * mm, "end": v(80, 74.5) * mm});
            skLineSegment(sketch, "E3.15.14.3", {"start": v(80, 79.5) * mm, "end": v(80, 74.5) * mm});
            skPoint(sketch, "E3.15.14.4", {"position": v(82.5, 77) * mm});
            skLineSegment(sketch, "E3.15.15.0", {"start": v(85, 85) * mm, "end": v(80, 85) * mm});
            skLineSegment(sketch, "E3.15.15.1", {"start": v(85, 85) * mm, "end": v(85, 80) * mm});
            skLineSegment(sketch, "E3.15.15.2", {"start": v(85, 80) * mm, "end": v(80, 80) * mm});
            skLineSegment(sketch, "E3.15.15.3", {"start": v(80, 85) * mm, "end": v(80, 80) * mm});
            skPoint(sketch, "E3.15.15.4", {"position": v(82.5, 82.5) * mm});
            skLineSegment(sketch, "E3.15.16.0", {"start": v(85, 90.5) * mm, "end": v(80, 90.5) * mm});
            skLineSegment(sketch, "E3.15.16.1", {"start": v(85, 90.5) * mm, "end": v(85, 85.5) * mm});
            skLineSegment(sketch, "E3.15.16.2", {"start": v(85, 85.5) * mm, "end": v(80, 85.5) * mm});
            skLineSegment(sketch, "E3.15.16.3", {"start": v(80, 90.5) * mm, "end": v(80, 85.5) * mm});
            skPoint(sketch, "E3.15.16.4", {"position": v(82.5, 88) * mm});
            skLineSegment(sketch, "E3.15.17.0", {"start": v(85, 96) * mm, "end": v(80, 96) * mm});
            skLineSegment(sketch, "E3.15.17.1", {"start": v(85, 96) * mm, "end": v(85, 91) * mm});
            skLineSegment(sketch, "E3.15.17.2", {"start": v(85, 91) * mm, "end": v(80, 91) * mm});
            skLineSegment(sketch, "E3.15.17.3", {"start": v(80, 96) * mm, "end": v(80, 91) * mm});
            skPoint(sketch, "E3.15.17.4", {"position": v(82.5, 93.5) * mm});
            skLineSegment(sketch, "E3.15.18.0", {"start": v(85, 101.5) * mm, "end": v(80, 101.5) * mm});
            skLineSegment(sketch, "E3.15.18.1", {"start": v(85, 101.5) * mm, "end": v(85, 96.5) * mm});
            skLineSegment(sketch, "E3.15.18.2", {"start": v(85, 96.5) * mm, "end": v(80, 96.5) * mm});
            skLineSegment(sketch, "E3.15.18.3", {"start": v(80, 101.5) * mm, "end": v(80, 96.5) * mm});
            skPoint(sketch, "E3.15.18.4", {"position": v(82.5, 99) * mm});
            skLineSegment(sketch, "E3.15.19.0", {"start": v(85, 107) * mm, "end": v(80, 107) * mm});
            skLineSegment(sketch, "E3.15.19.1", {"start": v(85, 107) * mm, "end": v(85, 102) * mm});
            skLineSegment(sketch, "E3.15.19.2", {"start": v(85, 102) * mm, "end": v(80, 102) * mm});
            skLineSegment(sketch, "E3.15.19.3", {"start": v(80, 107) * mm, "end": v(80, 102) * mm});
            skPoint(sketch, "E3.15.19.4", {"position": v(82.5, 104.5) * mm});
            skLineSegment(sketch, "E3.15.20.0", {"start": v(85, 112.5) * mm, "end": v(80, 112.5) * mm});
            skLineSegment(sketch, "E3.15.20.1", {"start": v(85, 112.5) * mm, "end": v(85, 107.5) * mm});
            skLineSegment(sketch, "E3.15.20.2", {"start": v(85, 107.5) * mm, "end": v(80, 107.5) * mm});
            skLineSegment(sketch, "E3.15.20.3", {"start": v(80, 112.5) * mm, "end": v(80, 107.5) * mm});
            skPoint(sketch, "E3.15.20.4", {"position": v(82.5, 110) * mm});
            skLineSegment(sketch, "E3.15.21.0", {"start": v(85, 118) * mm, "end": v(80, 118) * mm});
            skLineSegment(sketch, "E3.15.21.1", {"start": v(85, 118) * mm, "end": v(85, 113) * mm});
            skLineSegment(sketch, "E3.15.21.2", {"start": v(85, 113) * mm, "end": v(80, 113) * mm});
            skLineSegment(sketch, "E3.15.21.3", {"start": v(80, 118) * mm, "end": v(80, 113) * mm});
            skPoint(sketch, "E3.15.21.4", {"position": v(82.5, 115.5) * mm});
            skLineSegment(sketch, "E3.15.22.0", {"start": v(85, 123.5) * mm, "end": v(80, 123.5) * mm});
            skLineSegment(sketch, "E3.15.22.1", {"start": v(85, 123.5) * mm, "end": v(85, 118.5) * mm});
            skLineSegment(sketch, "E3.15.22.2", {"start": v(85, 118.5) * mm, "end": v(80, 118.5) * mm});
            skLineSegment(sketch, "E3.15.22.3", {"start": v(80, 123.5) * mm, "end": v(80, 118.5) * mm});
            skPoint(sketch, "E3.15.22.4", {"position": v(82.5, 121) * mm});
            skLineSegment(sketch, "E3.15.23.0", {"start": v(85, 129) * mm, "end": v(80, 129) * mm});
            skLineSegment(sketch, "E3.15.23.1", {"start": v(85, 129) * mm, "end": v(85, 124) * mm});
            skLineSegment(sketch, "E3.15.23.2", {"start": v(85, 124) * mm, "end": v(80, 124) * mm});
            skLineSegment(sketch, "E3.15.23.3", {"start": v(80, 129) * mm, "end": v(80, 124) * mm});
            skPoint(sketch, "E3.15.23.4", {"position": v(82.5, 126.5) * mm});
            skLineSegment(sketch, "E3.15.24.0", {"start": v(85, 134.5) * mm, "end": v(80, 134.5) * mm});
            skLineSegment(sketch, "E3.15.24.1", {"start": v(85, 134.5) * mm, "end": v(85, 129.5) * mm});
            skLineSegment(sketch, "E3.15.24.2", {"start": v(85, 129.5) * mm, "end": v(80, 129.5) * mm});
            skLineSegment(sketch, "E3.15.24.3", {"start": v(80, 134.5) * mm, "end": v(80, 129.5) * mm});
            skPoint(sketch, "E3.15.24.4", {"position": v(82.5, 132) * mm});
            skLineSegment(sketch, "E3.16.0.0", {"start": v(90.5, 2.5) * mm, "end": v(85.5, 2.5) * mm});
            skLineSegment(sketch, "E3.16.0.1", {"start": v(90.5, 2.5) * mm, "end": v(90.5, -2.5) * mm});
            skLineSegment(sketch, "E3.16.0.2", {"start": v(90.5, -2.5) * mm, "end": v(85.5, -2.5) * mm});
            skLineSegment(sketch, "E3.16.0.3", {"start": v(85.5, 2.5) * mm, "end": v(85.5, -2.5) * mm});
            skPoint(sketch, "E3.16.0.4", {"position": v(88, 0) * mm});
            skLineSegment(sketch, "E3.16.1.0", {"start": v(90.5, 8) * mm, "end": v(85.5, 8) * mm});
            skLineSegment(sketch, "E3.16.1.1", {"start": v(90.5, 8) * mm, "end": v(90.5, 3) * mm});
            skLineSegment(sketch, "E3.16.1.2", {"start": v(90.5, 3) * mm, "end": v(85.5, 3) * mm});
            skLineSegment(sketch, "E3.16.1.3", {"start": v(85.5, 8) * mm, "end": v(85.5, 3) * mm});
            skPoint(sketch, "E3.16.1.4", {"position": v(88, 5.5) * mm});
            skLineSegment(sketch, "E3.16.2.0", {"start": v(90.5, 13.5) * mm, "end": v(85.5, 13.5) * mm});
            skLineSegment(sketch, "E3.16.2.1", {"start": v(90.5, 13.5) * mm, "end": v(90.5, 8.5) * mm});
            skLineSegment(sketch, "E3.16.2.2", {"start": v(90.5, 8.5) * mm, "end": v(85.5, 8.5) * mm});
            skLineSegment(sketch, "E3.16.2.3", {"start": v(85.5, 13.5) * mm, "end": v(85.5, 8.5) * mm});
            skPoint(sketch, "E3.16.2.4", {"position": v(88, 11) * mm});
            skLineSegment(sketch, "E3.16.3.0", {"start": v(90.5, 19) * mm, "end": v(85.5, 19) * mm});
            skLineSegment(sketch, "E3.16.3.1", {"start": v(90.5, 19) * mm, "end": v(90.5, 14) * mm});
            skLineSegment(sketch, "E3.16.3.2", {"start": v(90.5, 14) * mm, "end": v(85.5, 14) * mm});
            skLineSegment(sketch, "E3.16.3.3", {"start": v(85.5, 19) * mm, "end": v(85.5, 14) * mm});
            skPoint(sketch, "E3.16.3.4", {"position": v(88, 16.5) * mm});
            skLineSegment(sketch, "E3.16.4.0", {"start": v(90.5, 24.5) * mm, "end": v(85.5, 24.5) * mm});
            skLineSegment(sketch, "E3.16.4.1", {"start": v(90.5, 24.5) * mm, "end": v(90.5, 19.5) * mm});
            skLineSegment(sketch, "E3.16.4.2", {"start": v(90.5, 19.5) * mm, "end": v(85.5, 19.5) * mm});
            skLineSegment(sketch, "E3.16.4.3", {"start": v(85.5, 24.5) * mm, "end": v(85.5, 19.5) * mm});
            skPoint(sketch, "E3.16.4.4", {"position": v(88, 22) * mm});
            skLineSegment(sketch, "E3.16.5.0", {"start": v(90.5, 30) * mm, "end": v(85.5, 30) * mm});
            skLineSegment(sketch, "E3.16.5.1", {"start": v(90.5, 30) * mm, "end": v(90.5, 25) * mm});
            skLineSegment(sketch, "E3.16.5.2", {"start": v(90.5, 25) * mm, "end": v(85.5, 25) * mm});
            skLineSegment(sketch, "E3.16.5.3", {"start": v(85.5, 30) * mm, "end": v(85.5, 25) * mm});
            skPoint(sketch, "E3.16.5.4", {"position": v(88, 27.5) * mm});
            skLineSegment(sketch, "E3.16.6.0", {"start": v(90.5, 35.5) * mm, "end": v(85.5, 35.5) * mm});
            skLineSegment(sketch, "E3.16.6.1", {"start": v(90.5, 35.5) * mm, "end": v(90.5, 30.5) * mm});
            skLineSegment(sketch, "E3.16.6.2", {"start": v(90.5, 30.5) * mm, "end": v(85.5, 30.5) * mm});
            skLineSegment(sketch, "E3.16.6.3", {"start": v(85.5, 35.5) * mm, "end": v(85.5, 30.5) * mm});
            skPoint(sketch, "E3.16.6.4", {"position": v(88, 33) * mm});
            skLineSegment(sketch, "E3.16.7.0", {"start": v(90.5, 41) * mm, "end": v(85.5, 41) * mm});
            skLineSegment(sketch, "E3.16.7.1", {"start": v(90.5, 41) * mm, "end": v(90.5, 36) * mm});
            skLineSegment(sketch, "E3.16.7.2", {"start": v(90.5, 36) * mm, "end": v(85.5, 36) * mm});
            skLineSegment(sketch, "E3.16.7.3", {"start": v(85.5, 41) * mm, "end": v(85.5, 36) * mm});
            skPoint(sketch, "E3.16.7.4", {"position": v(88, 38.5) * mm});
            skLineSegment(sketch, "E3.16.8.0", {"start": v(90.5, 46.5) * mm, "end": v(85.5, 46.5) * mm});
            skLineSegment(sketch, "E3.16.8.1", {"start": v(90.5, 46.5) * mm, "end": v(90.5, 41.5) * mm});
            skLineSegment(sketch, "E3.16.8.2", {"start": v(90.5, 41.5) * mm, "end": v(85.5, 41.5) * mm});
            skLineSegment(sketch, "E3.16.8.3", {"start": v(85.5, 46.5) * mm, "end": v(85.5, 41.5) * mm});
            skPoint(sketch, "E3.16.8.4", {"position": v(88, 44) * mm});
            skLineSegment(sketch, "E3.16.9.0", {"start": v(90.5, 52) * mm, "end": v(85.5, 52) * mm});
            skLineSegment(sketch, "E3.16.9.1", {"start": v(90.5, 52) * mm, "end": v(90.5, 47) * mm});
            skLineSegment(sketch, "E3.16.9.2", {"start": v(90.5, 47) * mm, "end": v(85.5, 47) * mm});
            skLineSegment(sketch, "E3.16.9.3", {"start": v(85.5, 52) * mm, "end": v(85.5, 47) * mm});
            skPoint(sketch, "E3.16.9.4", {"position": v(88, 49.5) * mm});
            skLineSegment(sketch, "E3.16.10.0", {"start": v(90.5, 57.5) * mm, "end": v(85.5, 57.5) * mm});
            skLineSegment(sketch, "E3.16.10.1", {"start": v(90.5, 57.5) * mm, "end": v(90.5, 52.5) * mm});
            skLineSegment(sketch, "E3.16.10.2", {"start": v(90.5, 52.5) * mm, "end": v(85.5, 52.5) * mm});
            skLineSegment(sketch, "E3.16.10.3", {"start": v(85.5, 57.5) * mm, "end": v(85.5, 52.5) * mm});
            skPoint(sketch, "E3.16.10.4", {"position": v(88, 55) * mm});
            skLineSegment(sketch, "E3.16.11.0", {"start": v(90.5, 63) * mm, "end": v(85.5, 63) * mm});
            skLineSegment(sketch, "E3.16.11.1", {"start": v(90.5, 63) * mm, "end": v(90.5, 58) * mm});
            skLineSegment(sketch, "E3.16.11.2", {"start": v(90.5, 58) * mm, "end": v(85.5, 58) * mm});
            skLineSegment(sketch, "E3.16.11.3", {"start": v(85.5, 63) * mm, "end": v(85.5, 58) * mm});
            skPoint(sketch, "E3.16.11.4", {"position": v(88, 60.5) * mm});
            skLineSegment(sketch, "E3.16.12.0", {"start": v(90.5, 68.5) * mm, "end": v(85.5, 68.5) * mm});
            skLineSegment(sketch, "E3.16.12.1", {"start": v(90.5, 68.5) * mm, "end": v(90.5, 63.5) * mm});
            skLineSegment(sketch, "E3.16.12.2", {"start": v(90.5, 63.5) * mm, "end": v(85.5, 63.5) * mm});
            skLineSegment(sketch, "E3.16.12.3", {"start": v(85.5, 68.5) * mm, "end": v(85.5, 63.5) * mm});
            skPoint(sketch, "E3.16.12.4", {"position": v(88, 66) * mm});
            skLineSegment(sketch, "E3.16.13.0", {"start": v(90.5, 74) * mm, "end": v(85.5, 74) * mm});
            skLineSegment(sketch, "E3.16.13.1", {"start": v(90.5, 74) * mm, "end": v(90.5, 69) * mm});
            skLineSegment(sketch, "E3.16.13.2", {"start": v(90.5, 69) * mm, "end": v(85.5, 69) * mm});
            skLineSegment(sketch, "E3.16.13.3", {"start": v(85.5, 74) * mm, "end": v(85.5, 69) * mm});
            skPoint(sketch, "E3.16.13.4", {"position": v(88, 71.5) * mm});
            skLineSegment(sketch, "E3.16.14.0", {"start": v(90.5, 79.5) * mm, "end": v(85.5, 79.5) * mm});
            skLineSegment(sketch, "E3.16.14.1", {"start": v(90.5, 79.5) * mm, "end": v(90.5, 74.5) * mm});
            skLineSegment(sketch, "E3.16.14.2", {"start": v(90.5, 74.5) * mm, "end": v(85.5, 74.5) * mm});
            skLineSegment(sketch, "E3.16.14.3", {"start": v(85.5, 79.5) * mm, "end": v(85.5, 74.5) * mm});
            skPoint(sketch, "E3.16.14.4", {"position": v(88, 77) * mm});
            skLineSegment(sketch, "E3.16.15.0", {"start": v(90.5, 85) * mm, "end": v(85.5, 85) * mm});
            skLineSegment(sketch, "E3.16.15.1", {"start": v(90.5, 85) * mm, "end": v(90.5, 80) * mm});
            skLineSegment(sketch, "E3.16.15.2", {"start": v(90.5, 80) * mm, "end": v(85.5, 80) * mm});
            skLineSegment(sketch, "E3.16.15.3", {"start": v(85.5, 85) * mm, "end": v(85.5, 80) * mm});
            skPoint(sketch, "E3.16.15.4", {"position": v(88, 82.5) * mm});
            skLineSegment(sketch, "E3.16.16.0", {"start": v(90.5, 90.5) * mm, "end": v(85.5, 90.5) * mm});
            skLineSegment(sketch, "E3.16.16.1", {"start": v(90.5, 90.5) * mm, "end": v(90.5, 85.5) * mm});
            skLineSegment(sketch, "E3.16.16.2", {"start": v(90.5, 85.5) * mm, "end": v(85.5, 85.5) * mm});
            skLineSegment(sketch, "E3.16.16.3", {"start": v(85.5, 90.5) * mm, "end": v(85.5, 85.5) * mm});
            skPoint(sketch, "E3.16.16.4", {"position": v(88, 88) * mm});
            skLineSegment(sketch, "E3.16.17.0", {"start": v(90.5, 96) * mm, "end": v(85.5, 96) * mm});
            skLineSegment(sketch, "E3.16.17.1", {"start": v(90.5, 96) * mm, "end": v(90.5, 91) * mm});
            skLineSegment(sketch, "E3.16.17.2", {"start": v(90.5, 91) * mm, "end": v(85.5, 91) * mm});
            skLineSegment(sketch, "E3.16.17.3", {"start": v(85.5, 96) * mm, "end": v(85.5, 91) * mm});
            skPoint(sketch, "E3.16.17.4", {"position": v(88, 93.5) * mm});
            skLineSegment(sketch, "E3.16.18.0", {"start": v(90.5, 101.5) * mm, "end": v(85.5, 101.5) * mm});
            skLineSegment(sketch, "E3.16.18.1", {"start": v(90.5, 101.5) * mm, "end": v(90.5, 96.5) * mm});
            skLineSegment(sketch, "E3.16.18.2", {"start": v(90.5, 96.5) * mm, "end": v(85.5, 96.5) * mm});
            skLineSegment(sketch, "E3.16.18.3", {"start": v(85.5, 101.5) * mm, "end": v(85.5, 96.5) * mm});
            skPoint(sketch, "E3.16.18.4", {"position": v(88, 99) * mm});
            skLineSegment(sketch, "E3.16.19.0", {"start": v(90.5, 107) * mm, "end": v(85.5, 107) * mm});
            skLineSegment(sketch, "E3.16.19.1", {"start": v(90.5, 107) * mm, "end": v(90.5, 102) * mm});
            skLineSegment(sketch, "E3.16.19.2", {"start": v(90.5, 102) * mm, "end": v(85.5, 102) * mm});
            skLineSegment(sketch, "E3.16.19.3", {"start": v(85.5, 107) * mm, "end": v(85.5, 102) * mm});
            skPoint(sketch, "E3.16.19.4", {"position": v(88, 104.5) * mm});
            skLineSegment(sketch, "E3.16.20.0", {"start": v(90.5, 112.5) * mm, "end": v(85.5, 112.5) * mm});
            skLineSegment(sketch, "E3.16.20.1", {"start": v(90.5, 112.5) * mm, "end": v(90.5, 107.5) * mm});
            skLineSegment(sketch, "E3.16.20.2", {"start": v(90.5, 107.5) * mm, "end": v(85.5, 107.5) * mm});
            skLineSegment(sketch, "E3.16.20.3", {"start": v(85.5, 112.5) * mm, "end": v(85.5, 107.5) * mm});
            skPoint(sketch, "E3.16.20.4", {"position": v(88, 110) * mm});
            skLineSegment(sketch, "E3.16.21.0", {"start": v(90.5, 118) * mm, "end": v(85.5, 118) * mm});
            skLineSegment(sketch, "E3.16.21.1", {"start": v(90.5, 118) * mm, "end": v(90.5, 113) * mm});
            skLineSegment(sketch, "E3.16.21.2", {"start": v(90.5, 113) * mm, "end": v(85.5, 113) * mm});
            skLineSegment(sketch, "E3.16.21.3", {"start": v(85.5, 118) * mm, "end": v(85.5, 113) * mm});
            skPoint(sketch, "E3.16.21.4", {"position": v(88, 115.5) * mm});
            skLineSegment(sketch, "E3.16.22.0", {"start": v(90.5, 123.5) * mm, "end": v(85.5, 123.5) * mm});
            skLineSegment(sketch, "E3.16.22.1", {"start": v(90.5, 123.5) * mm, "end": v(90.5, 118.5) * mm});
            skLineSegment(sketch, "E3.16.22.2", {"start": v(90.5, 118.5) * mm, "end": v(85.5, 118.5) * mm});
            skLineSegment(sketch, "E3.16.22.3", {"start": v(85.5, 123.5) * mm, "end": v(85.5, 118.5) * mm});
            skPoint(sketch, "E3.16.22.4", {"position": v(88, 121) * mm});
            skLineSegment(sketch, "E3.16.23.0", {"start": v(90.5, 129) * mm, "end": v(85.5, 129) * mm});
            skLineSegment(sketch, "E3.16.23.1", {"start": v(90.5, 129) * mm, "end": v(90.5, 124) * mm});
            skLineSegment(sketch, "E3.16.23.2", {"start": v(90.5, 124) * mm, "end": v(85.5, 124) * mm});
            skLineSegment(sketch, "E3.16.23.3", {"start": v(85.5, 129) * mm, "end": v(85.5, 124) * mm});
            skPoint(sketch, "E3.16.23.4", {"position": v(88, 126.5) * mm});
            skLineSegment(sketch, "E3.16.24.0", {"start": v(90.5, 134.5) * mm, "end": v(85.5, 134.5) * mm});
            skLineSegment(sketch, "E3.16.24.1", {"start": v(90.5, 134.5) * mm, "end": v(90.5, 129.5) * mm});
            skLineSegment(sketch, "E3.16.24.2", {"start": v(90.5, 129.5) * mm, "end": v(85.5, 129.5) * mm});
            skLineSegment(sketch, "E3.16.24.3", {"start": v(85.5, 134.5) * mm, "end": v(85.5, 129.5) * mm});
            skPoint(sketch, "E3.16.24.4", {"position": v(88, 132) * mm});
            skLineSegment(sketch, "E3.17.0.0", {"start": v(96, 2.5) * mm, "end": v(91, 2.5) * mm});
            skLineSegment(sketch, "E3.17.0.1", {"start": v(96, 2.5) * mm, "end": v(96, -2.5) * mm});
            skLineSegment(sketch, "E3.17.0.2", {"start": v(96, -2.5) * mm, "end": v(91, -2.5) * mm});
            skLineSegment(sketch, "E3.17.0.3", {"start": v(91, 2.5) * mm, "end": v(91, -2.5) * mm});
            skPoint(sketch, "E3.17.0.4", {"position": v(93.5, 0) * mm});
            skLineSegment(sketch, "E3.17.1.0", {"start": v(96, 8) * mm, "end": v(91, 8) * mm});
            skLineSegment(sketch, "E3.17.1.1", {"start": v(96, 8) * mm, "end": v(96, 3) * mm});
            skLineSegment(sketch, "E3.17.1.2", {"start": v(96, 3) * mm, "end": v(91, 3) * mm});
            skLineSegment(sketch, "E3.17.1.3", {"start": v(91, 8) * mm, "end": v(91, 3) * mm});
            skPoint(sketch, "E3.17.1.4", {"position": v(93.5, 5.5) * mm});
            skLineSegment(sketch, "E3.17.2.0", {"start": v(96, 13.5) * mm, "end": v(91, 13.5) * mm});
            skLineSegment(sketch, "E3.17.2.1", {"start": v(96, 13.5) * mm, "end": v(96, 8.5) * mm});
            skLineSegment(sketch, "E3.17.2.2", {"start": v(96, 8.5) * mm, "end": v(91, 8.5) * mm});
            skLineSegment(sketch, "E3.17.2.3", {"start": v(91, 13.5) * mm, "end": v(91, 8.5) * mm});
            skPoint(sketch, "E3.17.2.4", {"position": v(93.5, 11) * mm});
            skLineSegment(sketch, "E3.17.3.0", {"start": v(96, 19) * mm, "end": v(91, 19) * mm});
            skLineSegment(sketch, "E3.17.3.1", {"start": v(96, 19) * mm, "end": v(96, 14) * mm});
            skLineSegment(sketch, "E3.17.3.2", {"start": v(96, 14) * mm, "end": v(91, 14) * mm});
            skLineSegment(sketch, "E3.17.3.3", {"start": v(91, 19) * mm, "end": v(91, 14) * mm});
            skPoint(sketch, "E3.17.3.4", {"position": v(93.5, 16.5) * mm});
            skLineSegment(sketch, "E3.17.4.0", {"start": v(96, 24.5) * mm, "end": v(91, 24.5) * mm});
            skLineSegment(sketch, "E3.17.4.1", {"start": v(96, 24.5) * mm, "end": v(96, 19.5) * mm});
            skLineSegment(sketch, "E3.17.4.2", {"start": v(96, 19.5) * mm, "end": v(91, 19.5) * mm});
            skLineSegment(sketch, "E3.17.4.3", {"start": v(91, 24.5) * mm, "end": v(91, 19.5) * mm});
            skPoint(sketch, "E3.17.4.4", {"position": v(93.5, 22) * mm});
            skLineSegment(sketch, "E3.17.5.0", {"start": v(96, 30) * mm, "end": v(91, 30) * mm});
            skLineSegment(sketch, "E3.17.5.1", {"start": v(96, 30) * mm, "end": v(96, 25) * mm});
            skLineSegment(sketch, "E3.17.5.2", {"start": v(96, 25) * mm, "end": v(91, 25) * mm});
            skLineSegment(sketch, "E3.17.5.3", {"start": v(91, 30) * mm, "end": v(91, 25) * mm});
            skPoint(sketch, "E3.17.5.4", {"position": v(93.5, 27.5) * mm});
            skLineSegment(sketch, "E3.17.6.0", {"start": v(96, 35.5) * mm, "end": v(91, 35.5) * mm});
            skLineSegment(sketch, "E3.17.6.1", {"start": v(96, 35.5) * mm, "end": v(96, 30.5) * mm});
            skLineSegment(sketch, "E3.17.6.2", {"start": v(96, 30.5) * mm, "end": v(91, 30.5) * mm});
            skLineSegment(sketch, "E3.17.6.3", {"start": v(91, 35.5) * mm, "end": v(91, 30.5) * mm});
            skPoint(sketch, "E3.17.6.4", {"position": v(93.5, 33) * mm});
            skLineSegment(sketch, "E3.17.7.0", {"start": v(96, 41) * mm, "end": v(91, 41) * mm});
            skLineSegment(sketch, "E3.17.7.1", {"start": v(96, 41) * mm, "end": v(96, 36) * mm});
            skLineSegment(sketch, "E3.17.7.2", {"start": v(96, 36) * mm, "end": v(91, 36) * mm});
            skLineSegment(sketch, "E3.17.7.3", {"start": v(91, 41) * mm, "end": v(91, 36) * mm});
            skPoint(sketch, "E3.17.7.4", {"position": v(93.5, 38.5) * mm});
            skLineSegment(sketch, "E3.17.8.0", {"start": v(96, 46.5) * mm, "end": v(91, 46.5) * mm});
            skLineSegment(sketch, "E3.17.8.1", {"start": v(96, 46.5) * mm, "end": v(96, 41.5) * mm});
            skLineSegment(sketch, "E3.17.8.2", {"start": v(96, 41.5) * mm, "end": v(91, 41.5) * mm});
            skLineSegment(sketch, "E3.17.8.3", {"start": v(91, 46.5) * mm, "end": v(91, 41.5) * mm});
            skPoint(sketch, "E3.17.8.4", {"position": v(93.5, 44) * mm});
            skLineSegment(sketch, "E3.17.9.0", {"start": v(96, 52) * mm, "end": v(91, 52) * mm});
            skLineSegment(sketch, "E3.17.9.1", {"start": v(96, 52) * mm, "end": v(96, 47) * mm});
            skLineSegment(sketch, "E3.17.9.2", {"start": v(96, 47) * mm, "end": v(91, 47) * mm});
            skLineSegment(sketch, "E3.17.9.3", {"start": v(91, 52) * mm, "end": v(91, 47) * mm});
            skPoint(sketch, "E3.17.9.4", {"position": v(93.5, 49.5) * mm});
            skLineSegment(sketch, "E3.17.10.0", {"start": v(96, 57.5) * mm, "end": v(91, 57.5) * mm});
            skLineSegment(sketch, "E3.17.10.1", {"start": v(96, 57.5) * mm, "end": v(96, 52.5) * mm});
            skLineSegment(sketch, "E3.17.10.2", {"start": v(96, 52.5) * mm, "end": v(91, 52.5) * mm});
            skLineSegment(sketch, "E3.17.10.3", {"start": v(91, 57.5) * mm, "end": v(91, 52.5) * mm});
            skPoint(sketch, "E3.17.10.4", {"position": v(93.5, 55) * mm});
            skLineSegment(sketch, "E3.17.11.0", {"start": v(96, 63) * mm, "end": v(91, 63) * mm});
            skLineSegment(sketch, "E3.17.11.1", {"start": v(96, 63) * mm, "end": v(96, 58) * mm});
            skLineSegment(sketch, "E3.17.11.2", {"start": v(96, 58) * mm, "end": v(91, 58) * mm});
            skLineSegment(sketch, "E3.17.11.3", {"start": v(91, 63) * mm, "end": v(91, 58) * mm});
            skPoint(sketch, "E3.17.11.4", {"position": v(93.5, 60.5) * mm});
            skLineSegment(sketch, "E3.17.12.0", {"start": v(96, 68.5) * mm, "end": v(91, 68.5) * mm});
            skLineSegment(sketch, "E3.17.12.1", {"start": v(96, 68.5) * mm, "end": v(96, 63.5) * mm});
            skLineSegment(sketch, "E3.17.12.2", {"start": v(96, 63.5) * mm, "end": v(91, 63.5) * mm});
            skLineSegment(sketch, "E3.17.12.3", {"start": v(91, 68.5) * mm, "end": v(91, 63.5) * mm});
            skPoint(sketch, "E3.17.12.4", {"position": v(93.5, 66) * mm});
            skLineSegment(sketch, "E3.17.13.0", {"start": v(96, 74) * mm, "end": v(91, 74) * mm});
            skLineSegment(sketch, "E3.17.13.1", {"start": v(96, 74) * mm, "end": v(96, 69) * mm});
            skLineSegment(sketch, "E3.17.13.2", {"start": v(96, 69) * mm, "end": v(91, 69) * mm});
            skLineSegment(sketch, "E3.17.13.3", {"start": v(91, 74) * mm, "end": v(91, 69) * mm});
            skPoint(sketch, "E3.17.13.4", {"position": v(93.5, 71.5) * mm});
            skLineSegment(sketch, "E3.17.14.0", {"start": v(96, 79.5) * mm, "end": v(91, 79.5) * mm});
            skLineSegment(sketch, "E3.17.14.1", {"start": v(96, 79.5) * mm, "end": v(96, 74.5) * mm});
            skLineSegment(sketch, "E3.17.14.2", {"start": v(96, 74.5) * mm, "end": v(91, 74.5) * mm});
            skLineSegment(sketch, "E3.17.14.3", {"start": v(91, 79.5) * mm, "end": v(91, 74.5) * mm});
            skPoint(sketch, "E3.17.14.4", {"position": v(93.5, 77) * mm});
            skLineSegment(sketch, "E3.17.15.0", {"start": v(96, 85) * mm, "end": v(91, 85) * mm});
            skLineSegment(sketch, "E3.17.15.1", {"start": v(96, 85) * mm, "end": v(96, 80) * mm});
            skLineSegment(sketch, "E3.17.15.2", {"start": v(96, 80) * mm, "end": v(91, 80) * mm});
            skLineSegment(sketch, "E3.17.15.3", {"start": v(91, 85) * mm, "end": v(91, 80) * mm});
            skPoint(sketch, "E3.17.15.4", {"position": v(93.5, 82.5) * mm});
            skLineSegment(sketch, "E3.17.16.0", {"start": v(96, 90.5) * mm, "end": v(91, 90.5) * mm});
            skLineSegment(sketch, "E3.17.16.1", {"start": v(96, 90.5) * mm, "end": v(96, 85.5) * mm});
            skLineSegment(sketch, "E3.17.16.2", {"start": v(96, 85.5) * mm, "end": v(91, 85.5) * mm});
            skLineSegment(sketch, "E3.17.16.3", {"start": v(91, 90.5) * mm, "end": v(91, 85.5) * mm});
            skPoint(sketch, "E3.17.16.4", {"position": v(93.5, 88) * mm});
            skLineSegment(sketch, "E3.17.17.0", {"start": v(96, 96) * mm, "end": v(91, 96) * mm});
            skLineSegment(sketch, "E3.17.17.1", {"start": v(96, 96) * mm, "end": v(96, 91) * mm});
            skLineSegment(sketch, "E3.17.17.2", {"start": v(96, 91) * mm, "end": v(91, 91) * mm});
            skLineSegment(sketch, "E3.17.17.3", {"start": v(91, 96) * mm, "end": v(91, 91) * mm});
            skPoint(sketch, "E3.17.17.4", {"position": v(93.5, 93.5) * mm});
            skLineSegment(sketch, "E3.17.18.0", {"start": v(96, 101.5) * mm, "end": v(91, 101.5) * mm});
            skLineSegment(sketch, "E3.17.18.1", {"start": v(96, 101.5) * mm, "end": v(96, 96.5) * mm});
            skLineSegment(sketch, "E3.17.18.2", {"start": v(96, 96.5) * mm, "end": v(91, 96.5) * mm});
            skLineSegment(sketch, "E3.17.18.3", {"start": v(91, 101.5) * mm, "end": v(91, 96.5) * mm});
            skPoint(sketch, "E3.17.18.4", {"position": v(93.5, 99) * mm});
            skLineSegment(sketch, "E3.17.19.0", {"start": v(96, 107) * mm, "end": v(91, 107) * mm});
            skLineSegment(sketch, "E3.17.19.1", {"start": v(96, 107) * mm, "end": v(96, 102) * mm});
            skLineSegment(sketch, "E3.17.19.2", {"start": v(96, 102) * mm, "end": v(91, 102) * mm});
            skLineSegment(sketch, "E3.17.19.3", {"start": v(91, 107) * mm, "end": v(91, 102) * mm});
            skPoint(sketch, "E3.17.19.4", {"position": v(93.5, 104.5) * mm});
            skLineSegment(sketch, "E3.17.20.0", {"start": v(96, 112.5) * mm, "end": v(91, 112.5) * mm});
            skLineSegment(sketch, "E3.17.20.1", {"start": v(96, 112.5) * mm, "end": v(96, 107.5) * mm});
            skLineSegment(sketch, "E3.17.20.2", {"start": v(96, 107.5) * mm, "end": v(91, 107.5) * mm});
            skLineSegment(sketch, "E3.17.20.3", {"start": v(91, 112.5) * mm, "end": v(91, 107.5) * mm});
            skPoint(sketch, "E3.17.20.4", {"position": v(93.5, 110) * mm});
            skLineSegment(sketch, "E3.17.21.0", {"start": v(96, 118) * mm, "end": v(91, 118) * mm});
            skLineSegment(sketch, "E3.17.21.1", {"start": v(96, 118) * mm, "end": v(96, 113) * mm});
            skLineSegment(sketch, "E3.17.21.2", {"start": v(96, 113) * mm, "end": v(91, 113) * mm});
            skLineSegment(sketch, "E3.17.21.3", {"start": v(91, 118) * mm, "end": v(91, 113) * mm});
            skPoint(sketch, "E3.17.21.4", {"position": v(93.5, 115.5) * mm});
            skLineSegment(sketch, "E3.17.22.0", {"start": v(96, 123.5) * mm, "end": v(91, 123.5) * mm});
            skLineSegment(sketch, "E3.17.22.1", {"start": v(96, 123.5) * mm, "end": v(96, 118.5) * mm});
            skLineSegment(sketch, "E3.17.22.2", {"start": v(96, 118.5) * mm, "end": v(91, 118.5) * mm});
            skLineSegment(sketch, "E3.17.22.3", {"start": v(91, 123.5) * mm, "end": v(91, 118.5) * mm});
            skPoint(sketch, "E3.17.22.4", {"position": v(93.5, 121) * mm});
            skLineSegment(sketch, "E3.17.23.0", {"start": v(96, 129) * mm, "end": v(91, 129) * mm});
            skLineSegment(sketch, "E3.17.23.1", {"start": v(96, 129) * mm, "end": v(96, 124) * mm});
            skLineSegment(sketch, "E3.17.23.2", {"start": v(96, 124) * mm, "end": v(91, 124) * mm});
            skLineSegment(sketch, "E3.17.23.3", {"start": v(91, 129) * mm, "end": v(91, 124) * mm});
            skPoint(sketch, "E3.17.23.4", {"position": v(93.5, 126.5) * mm});
            skLineSegment(sketch, "E3.17.24.0", {"start": v(96, 134.5) * mm, "end": v(91, 134.5) * mm});
            skLineSegment(sketch, "E3.17.24.1", {"start": v(96, 134.5) * mm, "end": v(96, 129.5) * mm});
            skLineSegment(sketch, "E3.17.24.2", {"start": v(96, 129.5) * mm, "end": v(91, 129.5) * mm});
            skLineSegment(sketch, "E3.17.24.3", {"start": v(91, 134.5) * mm, "end": v(91, 129.5) * mm});
            skPoint(sketch, "E3.17.24.4", {"position": v(93.5, 132) * mm});
            skLineSegment(sketch, "E3.18.0.0", {"start": v(101.5, 2.5) * mm, "end": v(96.5, 2.5) * mm});
            skLineSegment(sketch, "E3.18.0.1", {"start": v(101.5, 2.5) * mm, "end": v(101.5, -2.5) * mm});
            skLineSegment(sketch, "E3.18.0.2", {"start": v(101.5, -2.5) * mm, "end": v(96.5, -2.5) * mm});
            skLineSegment(sketch, "E3.18.0.3", {"start": v(96.5, 2.5) * mm, "end": v(96.5, -2.5) * mm});
            skPoint(sketch, "E3.18.0.4", {"position": v(99, 0) * mm});
            skLineSegment(sketch, "E3.18.1.0", {"start": v(101.5, 8) * mm, "end": v(96.5, 8) * mm});
            skLineSegment(sketch, "E3.18.1.1", {"start": v(101.5, 8) * mm, "end": v(101.5, 3) * mm});
            skLineSegment(sketch, "E3.18.1.2", {"start": v(101.5, 3) * mm, "end": v(96.5, 3) * mm});
            skLineSegment(sketch, "E3.18.1.3", {"start": v(96.5, 8) * mm, "end": v(96.5, 3) * mm});
            skPoint(sketch, "E3.18.1.4", {"position": v(99, 5.5) * mm});
            skLineSegment(sketch, "E3.18.2.0", {"start": v(101.5, 13.5) * mm, "end": v(96.5, 13.5) * mm});
            skLineSegment(sketch, "E3.18.2.1", {"start": v(101.5, 13.5) * mm, "end": v(101.5, 8.5) * mm});
            skLineSegment(sketch, "E3.18.2.2", {"start": v(101.5, 8.5) * mm, "end": v(96.5, 8.5) * mm});
            skLineSegment(sketch, "E3.18.2.3", {"start": v(96.5, 13.5) * mm, "end": v(96.5, 8.5) * mm});
            skPoint(sketch, "E3.18.2.4", {"position": v(99, 11) * mm});
            skLineSegment(sketch, "E3.18.3.0", {"start": v(101.5, 19) * mm, "end": v(96.5, 19) * mm});
            skLineSegment(sketch, "E3.18.3.1", {"start": v(101.5, 19) * mm, "end": v(101.5, 14) * mm});
            skLineSegment(sketch, "E3.18.3.2", {"start": v(101.5, 14) * mm, "end": v(96.5, 14) * mm});
            skLineSegment(sketch, "E3.18.3.3", {"start": v(96.5, 19) * mm, "end": v(96.5, 14) * mm});
            skPoint(sketch, "E3.18.3.4", {"position": v(99, 16.5) * mm});
            skLineSegment(sketch, "E3.18.4.0", {"start": v(101.5, 24.5) * mm, "end": v(96.5, 24.5) * mm});
            skLineSegment(sketch, "E3.18.4.1", {"start": v(101.5, 24.5) * mm, "end": v(101.5, 19.5) * mm});
            skLineSegment(sketch, "E3.18.4.2", {"start": v(101.5, 19.5) * mm, "end": v(96.5, 19.5) * mm});
            skLineSegment(sketch, "E3.18.4.3", {"start": v(96.5, 24.5) * mm, "end": v(96.5, 19.5) * mm});
            skPoint(sketch, "E3.18.4.4", {"position": v(99, 22) * mm});
            skLineSegment(sketch, "E3.18.5.0", {"start": v(101.5, 30) * mm, "end": v(96.5, 30) * mm});
            skLineSegment(sketch, "E3.18.5.1", {"start": v(101.5, 30) * mm, "end": v(101.5, 25) * mm});
            skLineSegment(sketch, "E3.18.5.2", {"start": v(101.5, 25) * mm, "end": v(96.5, 25) * mm});
            skLineSegment(sketch, "E3.18.5.3", {"start": v(96.5, 30) * mm, "end": v(96.5, 25) * mm});
            skPoint(sketch, "E3.18.5.4", {"position": v(99, 27.5) * mm});
            skLineSegment(sketch, "E3.18.6.0", {"start": v(101.5, 35.5) * mm, "end": v(96.5, 35.5) * mm});
            skLineSegment(sketch, "E3.18.6.1", {"start": v(101.5, 35.5) * mm, "end": v(101.5, 30.5) * mm});
            skLineSegment(sketch, "E3.18.6.2", {"start": v(101.5, 30.5) * mm, "end": v(96.5, 30.5) * mm});
            skLineSegment(sketch, "E3.18.6.3", {"start": v(96.5, 35.5) * mm, "end": v(96.5, 30.5) * mm});
            skPoint(sketch, "E3.18.6.4", {"position": v(99, 33) * mm});
            skLineSegment(sketch, "E3.18.7.0", {"start": v(101.5, 41) * mm, "end": v(96.5, 41) * mm});
            skLineSegment(sketch, "E3.18.7.1", {"start": v(101.5, 41) * mm, "end": v(101.5, 36) * mm});
            skLineSegment(sketch, "E3.18.7.2", {"start": v(101.5, 36) * mm, "end": v(96.5, 36) * mm});
            skLineSegment(sketch, "E3.18.7.3", {"start": v(96.5, 41) * mm, "end": v(96.5, 36) * mm});
            skPoint(sketch, "E3.18.7.4", {"position": v(99, 38.5) * mm});
            skLineSegment(sketch, "E3.18.8.0", {"start": v(101.5, 46.5) * mm, "end": v(96.5, 46.5) * mm});
            skLineSegment(sketch, "E3.18.8.1", {"start": v(101.5, 46.5) * mm, "end": v(101.5, 41.5) * mm});
            skLineSegment(sketch, "E3.18.8.2", {"start": v(101.5, 41.5) * mm, "end": v(96.5, 41.5) * mm});
            skLineSegment(sketch, "E3.18.8.3", {"start": v(96.5, 46.5) * mm, "end": v(96.5, 41.5) * mm});
            skPoint(sketch, "E3.18.8.4", {"position": v(99, 44) * mm});
            skLineSegment(sketch, "E3.18.9.0", {"start": v(101.5, 52) * mm, "end": v(96.5, 52) * mm});
            skLineSegment(sketch, "E3.18.9.1", {"start": v(101.5, 52) * mm, "end": v(101.5, 47) * mm});
            skLineSegment(sketch, "E3.18.9.2", {"start": v(101.5, 47) * mm, "end": v(96.5, 47) * mm});
            skLineSegment(sketch, "E3.18.9.3", {"start": v(96.5, 52) * mm, "end": v(96.5, 47) * mm});
            skPoint(sketch, "E3.18.9.4", {"position": v(99, 49.5) * mm});
            skLineSegment(sketch, "E3.18.10.0", {"start": v(101.5, 57.5) * mm, "end": v(96.5, 57.5) * mm});
            skLineSegment(sketch, "E3.18.10.1", {"start": v(101.5, 57.5) * mm, "end": v(101.5, 52.5) * mm});
            skLineSegment(sketch, "E3.18.10.2", {"start": v(101.5, 52.5) * mm, "end": v(96.5, 52.5) * mm});
            skLineSegment(sketch, "E3.18.10.3", {"start": v(96.5, 57.5) * mm, "end": v(96.5, 52.5) * mm});
            skPoint(sketch, "E3.18.10.4", {"position": v(99, 55) * mm});
            skLineSegment(sketch, "E3.18.11.0", {"start": v(101.5, 63) * mm, "end": v(96.5, 63) * mm});
            skLineSegment(sketch, "E3.18.11.1", {"start": v(101.5, 63) * mm, "end": v(101.5, 58) * mm});
            skLineSegment(sketch, "E3.18.11.2", {"start": v(101.5, 58) * mm, "end": v(96.5, 58) * mm});
            skLineSegment(sketch, "E3.18.11.3", {"start": v(96.5, 63) * mm, "end": v(96.5, 58) * mm});
            skPoint(sketch, "E3.18.11.4", {"position": v(99, 60.5) * mm});
            skLineSegment(sketch, "E3.18.12.0", {"start": v(101.5, 68.5) * mm, "end": v(96.5, 68.5) * mm});
            skLineSegment(sketch, "E3.18.12.1", {"start": v(101.5, 68.5) * mm, "end": v(101.5, 63.5) * mm});
            skLineSegment(sketch, "E3.18.12.2", {"start": v(101.5, 63.5) * mm, "end": v(96.5, 63.5) * mm});
            skLineSegment(sketch, "E3.18.12.3", {"start": v(96.5, 68.5) * mm, "end": v(96.5, 63.5) * mm});
            skPoint(sketch, "E3.18.12.4", {"position": v(99, 66) * mm});
            skLineSegment(sketch, "E3.18.13.0", {"start": v(101.5, 74) * mm, "end": v(96.5, 74) * mm});
            skLineSegment(sketch, "E3.18.13.1", {"start": v(101.5, 74) * mm, "end": v(101.5, 69) * mm});
            skLineSegment(sketch, "E3.18.13.2", {"start": v(101.5, 69) * mm, "end": v(96.5, 69) * mm});
            skLineSegment(sketch, "E3.18.13.3", {"start": v(96.5, 74) * mm, "end": v(96.5, 69) * mm});
            skPoint(sketch, "E3.18.13.4", {"position": v(99, 71.5) * mm});
            skLineSegment(sketch, "E3.18.14.0", {"start": v(101.5, 79.5) * mm, "end": v(96.5, 79.5) * mm});
            skLineSegment(sketch, "E3.18.14.1", {"start": v(101.5, 79.5) * mm, "end": v(101.5, 74.5) * mm});
            skLineSegment(sketch, "E3.18.14.2", {"start": v(101.5, 74.5) * mm, "end": v(96.5, 74.5) * mm});
            skLineSegment(sketch, "E3.18.14.3", {"start": v(96.5, 79.5) * mm, "end": v(96.5, 74.5) * mm});
            skPoint(sketch, "E3.18.14.4", {"position": v(99, 77) * mm});
            skLineSegment(sketch, "E3.18.15.0", {"start": v(101.5, 85) * mm, "end": v(96.5, 85) * mm});
            skLineSegment(sketch, "E3.18.15.1", {"start": v(101.5, 85) * mm, "end": v(101.5, 80) * mm});
            skLineSegment(sketch, "E3.18.15.2", {"start": v(101.5, 80) * mm, "end": v(96.5, 80) * mm});
            skLineSegment(sketch, "E3.18.15.3", {"start": v(96.5, 85) * mm, "end": v(96.5, 80) * mm});
            skPoint(sketch, "E3.18.15.4", {"position": v(99, 82.5) * mm});
            skLineSegment(sketch, "E3.18.16.0", {"start": v(101.5, 90.5) * mm, "end": v(96.5, 90.5) * mm});
            skLineSegment(sketch, "E3.18.16.1", {"start": v(101.5, 90.5) * mm, "end": v(101.5, 85.5) * mm});
            skLineSegment(sketch, "E3.18.16.2", {"start": v(101.5, 85.5) * mm, "end": v(96.5, 85.5) * mm});
            skLineSegment(sketch, "E3.18.16.3", {"start": v(96.5, 90.5) * mm, "end": v(96.5, 85.5) * mm});
            skPoint(sketch, "E3.18.16.4", {"position": v(99, 88) * mm});
            skLineSegment(sketch, "E3.18.17.0", {"start": v(101.5, 96) * mm, "end": v(96.5, 96) * mm});
            skLineSegment(sketch, "E3.18.17.1", {"start": v(101.5, 96) * mm, "end": v(101.5, 91) * mm});
            skLineSegment(sketch, "E3.18.17.2", {"start": v(101.5, 91) * mm, "end": v(96.5, 91) * mm});
            skLineSegment(sketch, "E3.18.17.3", {"start": v(96.5, 96) * mm, "end": v(96.5, 91) * mm});
            skPoint(sketch, "E3.18.17.4", {"position": v(99, 93.5) * mm});
            skLineSegment(sketch, "E3.18.18.0", {"start": v(101.5, 101.5) * mm, "end": v(96.5, 101.5) * mm});
            skLineSegment(sketch, "E3.18.18.1", {"start": v(101.5, 101.5) * mm, "end": v(101.5, 96.5) * mm});
            skLineSegment(sketch, "E3.18.18.2", {"start": v(101.5, 96.5) * mm, "end": v(96.5, 96.5) * mm});
            skLineSegment(sketch, "E3.18.18.3", {"start": v(96.5, 101.5) * mm, "end": v(96.5, 96.5) * mm});
            skPoint(sketch, "E3.18.18.4", {"position": v(99, 99) * mm});
            skLineSegment(sketch, "E3.18.19.0", {"start": v(101.5, 107) * mm, "end": v(96.5, 107) * mm});
            skLineSegment(sketch, "E3.18.19.1", {"start": v(101.5, 107) * mm, "end": v(101.5, 102) * mm});
            skLineSegment(sketch, "E3.18.19.2", {"start": v(101.5, 102) * mm, "end": v(96.5, 102) * mm});
            skLineSegment(sketch, "E3.18.19.3", {"start": v(96.5, 107) * mm, "end": v(96.5, 102) * mm});
            skPoint(sketch, "E3.18.19.4", {"position": v(99, 104.5) * mm});
            skLineSegment(sketch, "E3.18.20.0", {"start": v(101.5, 112.5) * mm, "end": v(96.5, 112.5) * mm});
            skLineSegment(sketch, "E3.18.20.1", {"start": v(101.5, 112.5) * mm, "end": v(101.5, 107.5) * mm});
            skLineSegment(sketch, "E3.18.20.2", {"start": v(101.5, 107.5) * mm, "end": v(96.5, 107.5) * mm});
            skLineSegment(sketch, "E3.18.20.3", {"start": v(96.5, 112.5) * mm, "end": v(96.5, 107.5) * mm});
            skPoint(sketch, "E3.18.20.4", {"position": v(99, 110) * mm});
            skLineSegment(sketch, "E3.18.21.0", {"start": v(101.5, 118) * mm, "end": v(96.5, 118) * mm});
            skLineSegment(sketch, "E3.18.21.1", {"start": v(101.5, 118) * mm, "end": v(101.5, 113) * mm});
            skLineSegment(sketch, "E3.18.21.2", {"start": v(101.5, 113) * mm, "end": v(96.5, 113) * mm});
            skLineSegment(sketch, "E3.18.21.3", {"start": v(96.5, 118) * mm, "end": v(96.5, 113) * mm});
            skPoint(sketch, "E3.18.21.4", {"position": v(99, 115.5) * mm});
            skLineSegment(sketch, "E3.18.22.0", {"start": v(101.5, 123.5) * mm, "end": v(96.5, 123.5) * mm});
            skLineSegment(sketch, "E3.18.22.1", {"start": v(101.5, 123.5) * mm, "end": v(101.5, 118.5) * mm});
            skLineSegment(sketch, "E3.18.22.2", {"start": v(101.5, 118.5) * mm, "end": v(96.5, 118.5) * mm});
            skLineSegment(sketch, "E3.18.22.3", {"start": v(96.5, 123.5) * mm, "end": v(96.5, 118.5) * mm});
            skPoint(sketch, "E3.18.22.4", {"position": v(99, 121) * mm});
            skLineSegment(sketch, "E3.18.23.0", {"start": v(101.5, 129) * mm, "end": v(96.5, 129) * mm});
            skLineSegment(sketch, "E3.18.23.1", {"start": v(101.5, 129) * mm, "end": v(101.5, 124) * mm});
            skLineSegment(sketch, "E3.18.23.2", {"start": v(101.5, 124) * mm, "end": v(96.5, 124) * mm});
            skLineSegment(sketch, "E3.18.23.3", {"start": v(96.5, 129) * mm, "end": v(96.5, 124) * mm});
            skPoint(sketch, "E3.18.23.4", {"position": v(99, 126.5) * mm});
            skLineSegment(sketch, "E3.18.24.0", {"start": v(101.5, 134.5) * mm, "end": v(96.5, 134.5) * mm});
            skLineSegment(sketch, "E3.18.24.1", {"start": v(101.5, 134.5) * mm, "end": v(101.5, 129.5) * mm});
            skLineSegment(sketch, "E3.18.24.2", {"start": v(101.5, 129.5) * mm, "end": v(96.5, 129.5) * mm});
            skLineSegment(sketch, "E3.18.24.3", {"start": v(96.5, 134.5) * mm, "end": v(96.5, 129.5) * mm});
            skPoint(sketch, "E3.18.24.4", {"position": v(99, 132) * mm});
            skLineSegment(sketch, "E3.19.0.0", {"start": v(107, 2.5) * mm, "end": v(102, 2.5) * mm});
            skLineSegment(sketch, "E3.19.0.1", {"start": v(107, 2.5) * mm, "end": v(107, -2.5) * mm});
            skLineSegment(sketch, "E3.19.0.2", {"start": v(107, -2.5) * mm, "end": v(102, -2.5) * mm});
            skLineSegment(sketch, "E3.19.0.3", {"start": v(102, 2.5) * mm, "end": v(102, -2.5) * mm});
            skPoint(sketch, "E3.19.0.4", {"position": v(104.5, 0) * mm});
            skLineSegment(sketch, "E3.19.1.0", {"start": v(107, 8) * mm, "end": v(102, 8) * mm});
            skLineSegment(sketch, "E3.19.1.1", {"start": v(107, 8) * mm, "end": v(107, 3) * mm});
            skLineSegment(sketch, "E3.19.1.2", {"start": v(107, 3) * mm, "end": v(102, 3) * mm});
            skLineSegment(sketch, "E3.19.1.3", {"start": v(102, 8) * mm, "end": v(102, 3) * mm});
            skPoint(sketch, "E3.19.1.4", {"position": v(104.5, 5.5) * mm});
            skLineSegment(sketch, "E3.19.2.0", {"start": v(107, 13.5) * mm, "end": v(102, 13.5) * mm});
            skLineSegment(sketch, "E3.19.2.1", {"start": v(107, 13.5) * mm, "end": v(107, 8.5) * mm});
            skLineSegment(sketch, "E3.19.2.2", {"start": v(107, 8.5) * mm, "end": v(102, 8.5) * mm});
            skLineSegment(sketch, "E3.19.2.3", {"start": v(102, 13.5) * mm, "end": v(102, 8.5) * mm});
            skPoint(sketch, "E3.19.2.4", {"position": v(104.5, 11) * mm});
            skLineSegment(sketch, "E3.19.3.0", {"start": v(107, 19) * mm, "end": v(102, 19) * mm});
            skLineSegment(sketch, "E3.19.3.1", {"start": v(107, 19) * mm, "end": v(107, 14) * mm});
            skLineSegment(sketch, "E3.19.3.2", {"start": v(107, 14) * mm, "end": v(102, 14) * mm});
            skLineSegment(sketch, "E3.19.3.3", {"start": v(102, 19) * mm, "end": v(102, 14) * mm});
            skPoint(sketch, "E3.19.3.4", {"position": v(104.5, 16.5) * mm});
            skLineSegment(sketch, "E3.19.4.0", {"start": v(107, 24.5) * mm, "end": v(102, 24.5) * mm});
            skLineSegment(sketch, "E3.19.4.1", {"start": v(107, 24.5) * mm, "end": v(107, 19.5) * mm});
            skLineSegment(sketch, "E3.19.4.2", {"start": v(107, 19.5) * mm, "end": v(102, 19.5) * mm});
            skLineSegment(sketch, "E3.19.4.3", {"start": v(102, 24.5) * mm, "end": v(102, 19.5) * mm});
            skPoint(sketch, "E3.19.4.4", {"position": v(104.5, 22) * mm});
            skLineSegment(sketch, "E3.19.5.0", {"start": v(107, 30) * mm, "end": v(102, 30) * mm});
            skLineSegment(sketch, "E3.19.5.1", {"start": v(107, 30) * mm, "end": v(107, 25) * mm});
            skLineSegment(sketch, "E3.19.5.2", {"start": v(107, 25) * mm, "end": v(102, 25) * mm});
            skLineSegment(sketch, "E3.19.5.3", {"start": v(102, 30) * mm, "end": v(102, 25) * mm});
            skPoint(sketch, "E3.19.5.4", {"position": v(104.5, 27.5) * mm});
            skLineSegment(sketch, "E3.19.6.0", {"start": v(107, 35.5) * mm, "end": v(102, 35.5) * mm});
            skLineSegment(sketch, "E3.19.6.1", {"start": v(107, 35.5) * mm, "end": v(107, 30.5) * mm});
            skLineSegment(sketch, "E3.19.6.2", {"start": v(107, 30.5) * mm, "end": v(102, 30.5) * mm});
            skLineSegment(sketch, "E3.19.6.3", {"start": v(102, 35.5) * mm, "end": v(102, 30.5) * mm});
            skPoint(sketch, "E3.19.6.4", {"position": v(104.5, 33) * mm});
            skLineSegment(sketch, "E3.19.7.0", {"start": v(107, 41) * mm, "end": v(102, 41) * mm});
            skLineSegment(sketch, "E3.19.7.1", {"start": v(107, 41) * mm, "end": v(107, 36) * mm});
            skLineSegment(sketch, "E3.19.7.2", {"start": v(107, 36) * mm, "end": v(102, 36) * mm});
            skLineSegment(sketch, "E3.19.7.3", {"start": v(102, 41) * mm, "end": v(102, 36) * mm});
            skPoint(sketch, "E3.19.7.4", {"position": v(104.5, 38.5) * mm});
            skLineSegment(sketch, "E3.19.8.0", {"start": v(107, 46.5) * mm, "end": v(102, 46.5) * mm});
            skLineSegment(sketch, "E3.19.8.1", {"start": v(107, 46.5) * mm, "end": v(107, 41.5) * mm});
            skLineSegment(sketch, "E3.19.8.2", {"start": v(107, 41.5) * mm, "end": v(102, 41.5) * mm});
            skLineSegment(sketch, "E3.19.8.3", {"start": v(102, 46.5) * mm, "end": v(102, 41.5) * mm});
            skPoint(sketch, "E3.19.8.4", {"position": v(104.5, 44) * mm});
            skLineSegment(sketch, "E3.19.9.0", {"start": v(107, 52) * mm, "end": v(102, 52) * mm});
            skLineSegment(sketch, "E3.19.9.1", {"start": v(107, 52) * mm, "end": v(107, 47) * mm});
            skLineSegment(sketch, "E3.19.9.2", {"start": v(107, 47) * mm, "end": v(102, 47) * mm});
            skLineSegment(sketch, "E3.19.9.3", {"start": v(102, 52) * mm, "end": v(102, 47) * mm});
            skPoint(sketch, "E3.19.9.4", {"position": v(104.5, 49.5) * mm});
            skLineSegment(sketch, "E3.19.10.0", {"start": v(107, 57.5) * mm, "end": v(102, 57.5) * mm});
            skLineSegment(sketch, "E3.19.10.1", {"start": v(107, 57.5) * mm, "end": v(107, 52.5) * mm});
            skLineSegment(sketch, "E3.19.10.2", {"start": v(107, 52.5) * mm, "end": v(102, 52.5) * mm});
            skLineSegment(sketch, "E3.19.10.3", {"start": v(102, 57.5) * mm, "end": v(102, 52.5) * mm});
            skPoint(sketch, "E3.19.10.4", {"position": v(104.5, 55) * mm});
            skLineSegment(sketch, "E3.19.11.0", {"start": v(107, 63) * mm, "end": v(102, 63) * mm});
            skLineSegment(sketch, "E3.19.11.1", {"start": v(107, 63) * mm, "end": v(107, 58) * mm});
            skLineSegment(sketch, "E3.19.11.2", {"start": v(107, 58) * mm, "end": v(102, 58) * mm});
            skLineSegment(sketch, "E3.19.11.3", {"start": v(102, 63) * mm, "end": v(102, 58) * mm});
            skPoint(sketch, "E3.19.11.4", {"position": v(104.5, 60.5) * mm});
            skLineSegment(sketch, "E3.19.12.0", {"start": v(107, 68.5) * mm, "end": v(102, 68.5) * mm});
            skLineSegment(sketch, "E3.19.12.1", {"start": v(107, 68.5) * mm, "end": v(107, 63.5) * mm});
            skLineSegment(sketch, "E3.19.12.2", {"start": v(107, 63.5) * mm, "end": v(102, 63.5) * mm});
            skLineSegment(sketch, "E3.19.12.3", {"start": v(102, 68.5) * mm, "end": v(102, 63.5) * mm});
            skPoint(sketch, "E3.19.12.4", {"position": v(104.5, 66) * mm});
            skLineSegment(sketch, "E3.19.13.0", {"start": v(107, 74) * mm, "end": v(102, 74) * mm});
            skLineSegment(sketch, "E3.19.13.1", {"start": v(107, 74) * mm, "end": v(107, 69) * mm});
            skLineSegment(sketch, "E3.19.13.2", {"start": v(107, 69) * mm, "end": v(102, 69) * mm});
            skLineSegment(sketch, "E3.19.13.3", {"start": v(102, 74) * mm, "end": v(102, 69) * mm});
            skPoint(sketch, "E3.19.13.4", {"position": v(104.5, 71.5) * mm});
            skLineSegment(sketch, "E3.19.14.0", {"start": v(107, 79.5) * mm, "end": v(102, 79.5) * mm});
            skLineSegment(sketch, "E3.19.14.1", {"start": v(107, 79.5) * mm, "end": v(107, 74.5) * mm});
            skLineSegment(sketch, "E3.19.14.2", {"start": v(107, 74.5) * mm, "end": v(102, 74.5) * mm});
            skLineSegment(sketch, "E3.19.14.3", {"start": v(102, 79.5) * mm, "end": v(102, 74.5) * mm});
            skPoint(sketch, "E3.19.14.4", {"position": v(104.5, 77) * mm});
            skLineSegment(sketch, "E3.19.15.0", {"start": v(107, 85) * mm, "end": v(102, 85) * mm});
            skLineSegment(sketch, "E3.19.15.1", {"start": v(107, 85) * mm, "end": v(107, 80) * mm});
            skLineSegment(sketch, "E3.19.15.2", {"start": v(107, 80) * mm, "end": v(102, 80) * mm});
            skLineSegment(sketch, "E3.19.15.3", {"start": v(102, 85) * mm, "end": v(102, 80) * mm});
            skPoint(sketch, "E3.19.15.4", {"position": v(104.5, 82.5) * mm});
            skLineSegment(sketch, "E3.19.16.0", {"start": v(107, 90.5) * mm, "end": v(102, 90.5) * mm});
            skLineSegment(sketch, "E3.19.16.1", {"start": v(107, 90.5) * mm, "end": v(107, 85.5) * mm});
            skLineSegment(sketch, "E3.19.16.2", {"start": v(107, 85.5) * mm, "end": v(102, 85.5) * mm});
            skLineSegment(sketch, "E3.19.16.3", {"start": v(102, 90.5) * mm, "end": v(102, 85.5) * mm});
            skPoint(sketch, "E3.19.16.4", {"position": v(104.5, 88) * mm});
            skLineSegment(sketch, "E3.19.17.0", {"start": v(107, 96) * mm, "end": v(102, 96) * mm});
            skLineSegment(sketch, "E3.19.17.1", {"start": v(107, 96) * mm, "end": v(107, 91) * mm});
            skLineSegment(sketch, "E3.19.17.2", {"start": v(107, 91) * mm, "end": v(102, 91) * mm});
            skLineSegment(sketch, "E3.19.17.3", {"start": v(102, 96) * mm, "end": v(102, 91) * mm});
            skPoint(sketch, "E3.19.17.4", {"position": v(104.5, 93.5) * mm});
            skLineSegment(sketch, "E3.19.18.0", {"start": v(107, 101.5) * mm, "end": v(102, 101.5) * mm});
            skLineSegment(sketch, "E3.19.18.1", {"start": v(107, 101.5) * mm, "end": v(107, 96.5) * mm});
            skLineSegment(sketch, "E3.19.18.2", {"start": v(107, 96.5) * mm, "end": v(102, 96.5) * mm});
            skLineSegment(sketch, "E3.19.18.3", {"start": v(102, 101.5) * mm, "end": v(102, 96.5) * mm});
            skPoint(sketch, "E3.19.18.4", {"position": v(104.5, 99) * mm});
            skLineSegment(sketch, "E3.19.19.0", {"start": v(107, 107) * mm, "end": v(102, 107) * mm});
            skLineSegment(sketch, "E3.19.19.1", {"start": v(107, 107) * mm, "end": v(107, 102) * mm});
            skLineSegment(sketch, "E3.19.19.2", {"start": v(107, 102) * mm, "end": v(102, 102) * mm});
            skLineSegment(sketch, "E3.19.19.3", {"start": v(102, 107) * mm, "end": v(102, 102) * mm});
            skPoint(sketch, "E3.19.19.4", {"position": v(104.5, 104.5) * mm});
            skLineSegment(sketch, "E3.19.20.0", {"start": v(107, 112.5) * mm, "end": v(102, 112.5) * mm});
            skLineSegment(sketch, "E3.19.20.1", {"start": v(107, 112.5) * mm, "end": v(107, 107.5) * mm});
            skLineSegment(sketch, "E3.19.20.2", {"start": v(107, 107.5) * mm, "end": v(102, 107.5) * mm});
            skLineSegment(sketch, "E3.19.20.3", {"start": v(102, 112.5) * mm, "end": v(102, 107.5) * mm});
            skPoint(sketch, "E3.19.20.4", {"position": v(104.5, 110) * mm});
            skLineSegment(sketch, "E3.19.21.0", {"start": v(107, 118) * mm, "end": v(102, 118) * mm});
            skLineSegment(sketch, "E3.19.21.1", {"start": v(107, 118) * mm, "end": v(107, 113) * mm});
            skLineSegment(sketch, "E3.19.21.2", {"start": v(107, 113) * mm, "end": v(102, 113) * mm});
            skLineSegment(sketch, "E3.19.21.3", {"start": v(102, 118) * mm, "end": v(102, 113) * mm});
            skPoint(sketch, "E3.19.21.4", {"position": v(104.5, 115.5) * mm});
            skLineSegment(sketch, "E3.19.22.0", {"start": v(107, 123.5) * mm, "end": v(102, 123.5) * mm});
            skLineSegment(sketch, "E3.19.22.1", {"start": v(107, 123.5) * mm, "end": v(107, 118.5) * mm});
            skLineSegment(sketch, "E3.19.22.2", {"start": v(107, 118.5) * mm, "end": v(102, 118.5) * mm});
            skLineSegment(sketch, "E3.19.22.3", {"start": v(102, 123.5) * mm, "end": v(102, 118.5) * mm});
            skPoint(sketch, "E3.19.22.4", {"position": v(104.5, 121) * mm});
            skLineSegment(sketch, "E3.19.23.0", {"start": v(107, 129) * mm, "end": v(102, 129) * mm});
            skLineSegment(sketch, "E3.19.23.1", {"start": v(107, 129) * mm, "end": v(107, 124) * mm});
            skLineSegment(sketch, "E3.19.23.2", {"start": v(107, 124) * mm, "end": v(102, 124) * mm});
            skLineSegment(sketch, "E3.19.23.3", {"start": v(102, 129) * mm, "end": v(102, 124) * mm});
            skPoint(sketch, "E3.19.23.4", {"position": v(104.5, 126.5) * mm});
            skLineSegment(sketch, "E3.19.24.0", {"start": v(107, 134.5) * mm, "end": v(102, 134.5) * mm});
            skLineSegment(sketch, "E3.19.24.1", {"start": v(107, 134.5) * mm, "end": v(107, 129.5) * mm});
            skLineSegment(sketch, "E3.19.24.2", {"start": v(107, 129.5) * mm, "end": v(102, 129.5) * mm});
            skLineSegment(sketch, "E3.19.24.3", {"start": v(102, 134.5) * mm, "end": v(102, 129.5) * mm});
            skPoint(sketch, "E3.19.24.4", {"position": v(104.5, 132) * mm});
            skLineSegment(sketch, "E3.20.0.0", {"start": v(112.5, 2.5) * mm, "end": v(107.5, 2.5) * mm});
            skLineSegment(sketch, "E3.20.0.1", {"start": v(112.5, 2.5) * mm, "end": v(112.5, -2.5) * mm});
            skLineSegment(sketch, "E3.20.0.2", {"start": v(112.5, -2.5) * mm, "end": v(107.5, -2.5) * mm});
            skLineSegment(sketch, "E3.20.0.3", {"start": v(107.5, 2.5) * mm, "end": v(107.5, -2.5) * mm});
            skPoint(sketch, "E3.20.0.4", {"position": v(110, 0) * mm});
            skLineSegment(sketch, "E3.20.1.0", {"start": v(112.5, 8) * mm, "end": v(107.5, 8) * mm});
            skLineSegment(sketch, "E3.20.1.1", {"start": v(112.5, 8) * mm, "end": v(112.5, 3) * mm});
            skLineSegment(sketch, "E3.20.1.2", {"start": v(112.5, 3) * mm, "end": v(107.5, 3) * mm});
            skLineSegment(sketch, "E3.20.1.3", {"start": v(107.5, 8) * mm, "end": v(107.5, 3) * mm});
            skPoint(sketch, "E3.20.1.4", {"position": v(110, 5.5) * mm});
            skLineSegment(sketch, "E3.20.2.0", {"start": v(112.5, 13.5) * mm, "end": v(107.5, 13.5) * mm});
            skLineSegment(sketch, "E3.20.2.1", {"start": v(112.5, 13.5) * mm, "end": v(112.5, 8.5) * mm});
            skLineSegment(sketch, "E3.20.2.2", {"start": v(112.5, 8.5) * mm, "end": v(107.5, 8.5) * mm});
            skLineSegment(sketch, "E3.20.2.3", {"start": v(107.5, 13.5) * mm, "end": v(107.5, 8.5) * mm});
            skPoint(sketch, "E3.20.2.4", {"position": v(110, 11) * mm});
            skLineSegment(sketch, "E3.20.3.0", {"start": v(112.5, 19) * mm, "end": v(107.5, 19) * mm});
            skLineSegment(sketch, "E3.20.3.1", {"start": v(112.5, 19) * mm, "end": v(112.5, 14) * mm});
            skLineSegment(sketch, "E3.20.3.2", {"start": v(112.5, 14) * mm, "end": v(107.5, 14) * mm});
            skLineSegment(sketch, "E3.20.3.3", {"start": v(107.5, 19) * mm, "end": v(107.5, 14) * mm});
            skPoint(sketch, "E3.20.3.4", {"position": v(110, 16.5) * mm});
            skLineSegment(sketch, "E3.20.4.0", {"start": v(112.5, 24.5) * mm, "end": v(107.5, 24.5) * mm});
            skLineSegment(sketch, "E3.20.4.1", {"start": v(112.5, 24.5) * mm, "end": v(112.5, 19.5) * mm});
            skLineSegment(sketch, "E3.20.4.2", {"start": v(112.5, 19.5) * mm, "end": v(107.5, 19.5) * mm});
            skLineSegment(sketch, "E3.20.4.3", {"start": v(107.5, 24.5) * mm, "end": v(107.5, 19.5) * mm});
            skPoint(sketch, "E3.20.4.4", {"position": v(110, 22) * mm});
            skLineSegment(sketch, "E3.20.5.0", {"start": v(112.5, 30) * mm, "end": v(107.5, 30) * mm});
            skLineSegment(sketch, "E3.20.5.1", {"start": v(112.5, 30) * mm, "end": v(112.5, 25) * mm});
            skLineSegment(sketch, "E3.20.5.2", {"start": v(112.5, 25) * mm, "end": v(107.5, 25) * mm});
            skLineSegment(sketch, "E3.20.5.3", {"start": v(107.5, 30) * mm, "end": v(107.5, 25) * mm});
            skPoint(sketch, "E3.20.5.4", {"position": v(110, 27.5) * mm});
            skLineSegment(sketch, "E3.20.6.0", {"start": v(112.5, 35.5) * mm, "end": v(107.5, 35.5) * mm});
            skLineSegment(sketch, "E3.20.6.1", {"start": v(112.5, 35.5) * mm, "end": v(112.5, 30.5) * mm});
            skLineSegment(sketch, "E3.20.6.2", {"start": v(112.5, 30.5) * mm, "end": v(107.5, 30.5) * mm});
            skLineSegment(sketch, "E3.20.6.3", {"start": v(107.5, 35.5) * mm, "end": v(107.5, 30.5) * mm});
            skPoint(sketch, "E3.20.6.4", {"position": v(110, 33) * mm});
            skLineSegment(sketch, "E3.20.7.0", {"start": v(112.5, 41) * mm, "end": v(107.5, 41) * mm});
            skLineSegment(sketch, "E3.20.7.1", {"start": v(112.5, 41) * mm, "end": v(112.5, 36) * mm});
            skLineSegment(sketch, "E3.20.7.2", {"start": v(112.5, 36) * mm, "end": v(107.5, 36) * mm});
            skLineSegment(sketch, "E3.20.7.3", {"start": v(107.5, 41) * mm, "end": v(107.5, 36) * mm});
            skPoint(sketch, "E3.20.7.4", {"position": v(110, 38.5) * mm});
            skLineSegment(sketch, "E3.20.8.0", {"start": v(112.5, 46.5) * mm, "end": v(107.5, 46.5) * mm});
            skLineSegment(sketch, "E3.20.8.1", {"start": v(112.5, 46.5) * mm, "end": v(112.5, 41.5) * mm});
            skLineSegment(sketch, "E3.20.8.2", {"start": v(112.5, 41.5) * mm, "end": v(107.5, 41.5) * mm});
            skLineSegment(sketch, "E3.20.8.3", {"start": v(107.5, 46.5) * mm, "end": v(107.5, 41.5) * mm});
            skPoint(sketch, "E3.20.8.4", {"position": v(110, 44) * mm});
            skLineSegment(sketch, "E3.20.9.0", {"start": v(112.5, 52) * mm, "end": v(107.5, 52) * mm});
            skLineSegment(sketch, "E3.20.9.1", {"start": v(112.5, 52) * mm, "end": v(112.5, 47) * mm});
            skLineSegment(sketch, "E3.20.9.2", {"start": v(112.5, 47) * mm, "end": v(107.5, 47) * mm});
            skLineSegment(sketch, "E3.20.9.3", {"start": v(107.5, 52) * mm, "end": v(107.5, 47) * mm});
            skPoint(sketch, "E3.20.9.4", {"position": v(110, 49.5) * mm});
            skLineSegment(sketch, "E3.20.10.0", {"start": v(112.5, 57.5) * mm, "end": v(107.5, 57.5) * mm});
            skLineSegment(sketch, "E3.20.10.1", {"start": v(112.5, 57.5) * mm, "end": v(112.5, 52.5) * mm});
            skLineSegment(sketch, "E3.20.10.2", {"start": v(112.5, 52.5) * mm, "end": v(107.5, 52.5) * mm});
            skLineSegment(sketch, "E3.20.10.3", {"start": v(107.5, 57.5) * mm, "end": v(107.5, 52.5) * mm});
            skPoint(sketch, "E3.20.10.4", {"position": v(110, 55) * mm});
            skLineSegment(sketch, "E3.20.11.0", {"start": v(112.5, 63) * mm, "end": v(107.5, 63) * mm});
            skLineSegment(sketch, "E3.20.11.1", {"start": v(112.5, 63) * mm, "end": v(112.5, 58) * mm});
            skLineSegment(sketch, "E3.20.11.2", {"start": v(112.5, 58) * mm, "end": v(107.5, 58) * mm});
            skLineSegment(sketch, "E3.20.11.3", {"start": v(107.5, 63) * mm, "end": v(107.5, 58) * mm});
            skPoint(sketch, "E3.20.11.4", {"position": v(110, 60.5) * mm});
            skLineSegment(sketch, "E3.20.12.0", {"start": v(112.5, 68.5) * mm, "end": v(107.5, 68.5) * mm});
            skLineSegment(sketch, "E3.20.12.1", {"start": v(112.5, 68.5) * mm, "end": v(112.5, 63.5) * mm});
            skLineSegment(sketch, "E3.20.12.2", {"start": v(112.5, 63.5) * mm, "end": v(107.5, 63.5) * mm});
            skLineSegment(sketch, "E3.20.12.3", {"start": v(107.5, 68.5) * mm, "end": v(107.5, 63.5) * mm});
            skPoint(sketch, "E3.20.12.4", {"position": v(110, 66) * mm});
            skLineSegment(sketch, "E3.20.13.0", {"start": v(112.5, 74) * mm, "end": v(107.5, 74) * mm});
            skLineSegment(sketch, "E3.20.13.1", {"start": v(112.5, 74) * mm, "end": v(112.5, 69) * mm});
            skLineSegment(sketch, "E3.20.13.2", {"start": v(112.5, 69) * mm, "end": v(107.5, 69) * mm});
            skLineSegment(sketch, "E3.20.13.3", {"start": v(107.5, 74) * mm, "end": v(107.5, 69) * mm});
            skPoint(sketch, "E3.20.13.4", {"position": v(110, 71.5) * mm});
            skLineSegment(sketch, "E3.20.14.0", {"start": v(112.5, 79.5) * mm, "end": v(107.5, 79.5) * mm});
            skLineSegment(sketch, "E3.20.14.1", {"start": v(112.5, 79.5) * mm, "end": v(112.5, 74.5) * mm});
            skLineSegment(sketch, "E3.20.14.2", {"start": v(112.5, 74.5) * mm, "end": v(107.5, 74.5) * mm});
            skLineSegment(sketch, "E3.20.14.3", {"start": v(107.5, 79.5) * mm, "end": v(107.5, 74.5) * mm});
            skPoint(sketch, "E3.20.14.4", {"position": v(110, 77) * mm});
            skLineSegment(sketch, "E3.20.15.0", {"start": v(112.5, 85) * mm, "end": v(107.5, 85) * mm});
            skLineSegment(sketch, "E3.20.15.1", {"start": v(112.5, 85) * mm, "end": v(112.5, 80) * mm});
            skLineSegment(sketch, "E3.20.15.2", {"start": v(112.5, 80) * mm, "end": v(107.5, 80) * mm});
            skLineSegment(sketch, "E3.20.15.3", {"start": v(107.5, 85) * mm, "end": v(107.5, 80) * mm});
            skPoint(sketch, "E3.20.15.4", {"position": v(110, 82.5) * mm});
            skLineSegment(sketch, "E3.20.16.0", {"start": v(112.5, 90.5) * mm, "end": v(107.5, 90.5) * mm});
            skLineSegment(sketch, "E3.20.16.1", {"start": v(112.5, 90.5) * mm, "end": v(112.5, 85.5) * mm});
            skLineSegment(sketch, "E3.20.16.2", {"start": v(112.5, 85.5) * mm, "end": v(107.5, 85.5) * mm});
            skLineSegment(sketch, "E3.20.16.3", {"start": v(107.5, 90.5) * mm, "end": v(107.5, 85.5) * mm});
            skPoint(sketch, "E3.20.16.4", {"position": v(110, 88) * mm});
            skLineSegment(sketch, "E3.20.17.0", {"start": v(112.5, 96) * mm, "end": v(107.5, 96) * mm});
            skLineSegment(sketch, "E3.20.17.1", {"start": v(112.5, 96) * mm, "end": v(112.5, 91) * mm});
            skLineSegment(sketch, "E3.20.17.2", {"start": v(112.5, 91) * mm, "end": v(107.5, 91) * mm});
            skLineSegment(sketch, "E3.20.17.3", {"start": v(107.5, 96) * mm, "end": v(107.5, 91) * mm});
            skPoint(sketch, "E3.20.17.4", {"position": v(110, 93.5) * mm});
            skLineSegment(sketch, "E3.20.18.0", {"start": v(112.5, 101.5) * mm, "end": v(107.5, 101.5) * mm});
            skLineSegment(sketch, "E3.20.18.1", {"start": v(112.5, 101.5) * mm, "end": v(112.5, 96.5) * mm});
            skLineSegment(sketch, "E3.20.18.2", {"start": v(112.5, 96.5) * mm, "end": v(107.5, 96.5) * mm});
            skLineSegment(sketch, "E3.20.18.3", {"start": v(107.5, 101.5) * mm, "end": v(107.5, 96.5) * mm});
            skPoint(sketch, "E3.20.18.4", {"position": v(110, 99) * mm});
            skLineSegment(sketch, "E3.20.19.0", {"start": v(112.5, 107) * mm, "end": v(107.5, 107) * mm});
            skLineSegment(sketch, "E3.20.19.1", {"start": v(112.5, 107) * mm, "end": v(112.5, 102) * mm});
            skLineSegment(sketch, "E3.20.19.2", {"start": v(112.5, 102) * mm, "end": v(107.5, 102) * mm});
            skLineSegment(sketch, "E3.20.19.3", {"start": v(107.5, 107) * mm, "end": v(107.5, 102) * mm});
            skPoint(sketch, "E3.20.19.4", {"position": v(110, 104.5) * mm});
            skLineSegment(sketch, "E3.20.20.0", {"start": v(112.5, 112.5) * mm, "end": v(107.5, 112.5) * mm});
            skLineSegment(sketch, "E3.20.20.1", {"start": v(112.5, 112.5) * mm, "end": v(112.5, 107.5) * mm});
            skLineSegment(sketch, "E3.20.20.2", {"start": v(112.5, 107.5) * mm, "end": v(107.5, 107.5) * mm});
            skLineSegment(sketch, "E3.20.20.3", {"start": v(107.5, 112.5) * mm, "end": v(107.5, 107.5) * mm});
            skPoint(sketch, "E3.20.20.4", {"position": v(110, 110) * mm});
            skLineSegment(sketch, "E3.20.21.0", {"start": v(112.5, 118) * mm, "end": v(107.5, 118) * mm});
            skLineSegment(sketch, "E3.20.21.1", {"start": v(112.5, 118) * mm, "end": v(112.5, 113) * mm});
            skLineSegment(sketch, "E3.20.21.2", {"start": v(112.5, 113) * mm, "end": v(107.5, 113) * mm});
            skLineSegment(sketch, "E3.20.21.3", {"start": v(107.5, 118) * mm, "end": v(107.5, 113) * mm});
            skPoint(sketch, "E3.20.21.4", {"position": v(110, 115.5) * mm});
            skLineSegment(sketch, "E3.20.22.0", {"start": v(112.5, 123.5) * mm, "end": v(107.5, 123.5) * mm});
            skLineSegment(sketch, "E3.20.22.1", {"start": v(112.5, 123.5) * mm, "end": v(112.5, 118.5) * mm});
            skLineSegment(sketch, "E3.20.22.2", {"start": v(112.5, 118.5) * mm, "end": v(107.5, 118.5) * mm});
            skLineSegment(sketch, "E3.20.22.3", {"start": v(107.5, 123.5) * mm, "end": v(107.5, 118.5) * mm});
            skPoint(sketch, "E3.20.22.4", {"position": v(110, 121) * mm});
            skLineSegment(sketch, "E3.20.23.0", {"start": v(112.5, 129) * mm, "end": v(107.5, 129) * mm});
            skLineSegment(sketch, "E3.20.23.1", {"start": v(112.5, 129) * mm, "end": v(112.5, 124) * mm});
            skLineSegment(sketch, "E3.20.23.2", {"start": v(112.5, 124) * mm, "end": v(107.5, 124) * mm});
            skLineSegment(sketch, "E3.20.23.3", {"start": v(107.5, 129) * mm, "end": v(107.5, 124) * mm});
            skPoint(sketch, "E3.20.23.4", {"position": v(110, 126.5) * mm});
            skLineSegment(sketch, "E3.20.24.0", {"start": v(112.5, 134.5) * mm, "end": v(107.5, 134.5) * mm});
            skLineSegment(sketch, "E3.20.24.1", {"start": v(112.5, 134.5) * mm, "end": v(112.5, 129.5) * mm});
            skLineSegment(sketch, "E3.20.24.2", {"start": v(112.5, 129.5) * mm, "end": v(107.5, 129.5) * mm});
            skLineSegment(sketch, "E3.20.24.3", {"start": v(107.5, 134.5) * mm, "end": v(107.5, 129.5) * mm});
            skPoint(sketch, "E3.20.24.4", {"position": v(110, 132) * mm});
            skLineSegment(sketch, "E3.21.0.0", {"start": v(118, 2.5) * mm, "end": v(113, 2.5) * mm});
            skLineSegment(sketch, "E3.21.0.1", {"start": v(118, 2.5) * mm, "end": v(118, -2.5) * mm});
            skLineSegment(sketch, "E3.21.0.2", {"start": v(118, -2.5) * mm, "end": v(113, -2.5) * mm});
            skLineSegment(sketch, "E3.21.0.3", {"start": v(113, 2.5) * mm, "end": v(113, -2.5) * mm});
            skPoint(sketch, "E3.21.0.4", {"position": v(115.5, 0) * mm});
            skLineSegment(sketch, "E3.21.1.0", {"start": v(118, 8) * mm, "end": v(113, 8) * mm});
            skLineSegment(sketch, "E3.21.1.1", {"start": v(118, 8) * mm, "end": v(118, 3) * mm});
            skLineSegment(sketch, "E3.21.1.2", {"start": v(118, 3) * mm, "end": v(113, 3) * mm});
            skLineSegment(sketch, "E3.21.1.3", {"start": v(113, 8) * mm, "end": v(113, 3) * mm});
            skPoint(sketch, "E3.21.1.4", {"position": v(115.5, 5.5) * mm});
            skLineSegment(sketch, "E3.21.2.0", {"start": v(118, 13.5) * mm, "end": v(113, 13.5) * mm});
            skLineSegment(sketch, "E3.21.2.1", {"start": v(118, 13.5) * mm, "end": v(118, 8.5) * mm});
            skLineSegment(sketch, "E3.21.2.2", {"start": v(118, 8.5) * mm, "end": v(113, 8.5) * mm});
            skLineSegment(sketch, "E3.21.2.3", {"start": v(113, 13.5) * mm, "end": v(113, 8.5) * mm});
            skPoint(sketch, "E3.21.2.4", {"position": v(115.5, 11) * mm});
            skLineSegment(sketch, "E3.21.3.0", {"start": v(118, 19) * mm, "end": v(113, 19) * mm});
            skLineSegment(sketch, "E3.21.3.1", {"start": v(118, 19) * mm, "end": v(118, 14) * mm});
            skLineSegment(sketch, "E3.21.3.2", {"start": v(118, 14) * mm, "end": v(113, 14) * mm});
            skLineSegment(sketch, "E3.21.3.3", {"start": v(113, 19) * mm, "end": v(113, 14) * mm});
            skPoint(sketch, "E3.21.3.4", {"position": v(115.5, 16.5) * mm});
            skLineSegment(sketch, "E3.21.4.0", {"start": v(118, 24.5) * mm, "end": v(113, 24.5) * mm});
            skLineSegment(sketch, "E3.21.4.1", {"start": v(118, 24.5) * mm, "end": v(118, 19.5) * mm});
            skLineSegment(sketch, "E3.21.4.2", {"start": v(118, 19.5) * mm, "end": v(113, 19.5) * mm});
            skLineSegment(sketch, "E3.21.4.3", {"start": v(113, 24.5) * mm, "end": v(113, 19.5) * mm});
            skPoint(sketch, "E3.21.4.4", {"position": v(115.5, 22) * mm});
            skLineSegment(sketch, "E3.21.5.0", {"start": v(118, 30) * mm, "end": v(113, 30) * mm});
            skLineSegment(sketch, "E3.21.5.1", {"start": v(118, 30) * mm, "end": v(118, 25) * mm});
            skLineSegment(sketch, "E3.21.5.2", {"start": v(118, 25) * mm, "end": v(113, 25) * mm});
            skLineSegment(sketch, "E3.21.5.3", {"start": v(113, 30) * mm, "end": v(113, 25) * mm});
            skPoint(sketch, "E3.21.5.4", {"position": v(115.5, 27.5) * mm});
            skLineSegment(sketch, "E3.21.6.0", {"start": v(118, 35.5) * mm, "end": v(113, 35.5) * mm});
            skLineSegment(sketch, "E3.21.6.1", {"start": v(118, 35.5) * mm, "end": v(118, 30.5) * mm});
            skLineSegment(sketch, "E3.21.6.2", {"start": v(118, 30.5) * mm, "end": v(113, 30.5) * mm});
            skLineSegment(sketch, "E3.21.6.3", {"start": v(113, 35.5) * mm, "end": v(113, 30.5) * mm});
            skPoint(sketch, "E3.21.6.4", {"position": v(115.5, 33) * mm});
            skLineSegment(sketch, "E3.21.7.0", {"start": v(118, 41) * mm, "end": v(113, 41) * mm});
            skLineSegment(sketch, "E3.21.7.1", {"start": v(118, 41) * mm, "end": v(118, 36) * mm});
            skLineSegment(sketch, "E3.21.7.2", {"start": v(118, 36) * mm, "end": v(113, 36) * mm});
            skLineSegment(sketch, "E3.21.7.3", {"start": v(113, 41) * mm, "end": v(113, 36) * mm});
            skPoint(sketch, "E3.21.7.4", {"position": v(115.5, 38.5) * mm});
            skLineSegment(sketch, "E3.21.8.0", {"start": v(118, 46.5) * mm, "end": v(113, 46.5) * mm});
            skLineSegment(sketch, "E3.21.8.1", {"start": v(118, 46.5) * mm, "end": v(118, 41.5) * mm});
            skLineSegment(sketch, "E3.21.8.2", {"start": v(118, 41.5) * mm, "end": v(113, 41.5) * mm});
            skLineSegment(sketch, "E3.21.8.3", {"start": v(113, 46.5) * mm, "end": v(113, 41.5) * mm});
            skPoint(sketch, "E3.21.8.4", {"position": v(115.5, 44) * mm});
            skLineSegment(sketch, "E3.21.9.0", {"start": v(118, 52) * mm, "end": v(113, 52) * mm});
            skLineSegment(sketch, "E3.21.9.1", {"start": v(118, 52) * mm, "end": v(118, 47) * mm});
            skLineSegment(sketch, "E3.21.9.2", {"start": v(118, 47) * mm, "end": v(113, 47) * mm});
            skLineSegment(sketch, "E3.21.9.3", {"start": v(113, 52) * mm, "end": v(113, 47) * mm});
            skPoint(sketch, "E3.21.9.4", {"position": v(115.5, 49.5) * mm});
            skLineSegment(sketch, "E3.21.10.0", {"start": v(118, 57.5) * mm, "end": v(113, 57.5) * mm});
            skLineSegment(sketch, "E3.21.10.1", {"start": v(118, 57.5) * mm, "end": v(118, 52.5) * mm});
            skLineSegment(sketch, "E3.21.10.2", {"start": v(118, 52.5) * mm, "end": v(113, 52.5) * mm});
            skLineSegment(sketch, "E3.21.10.3", {"start": v(113, 57.5) * mm, "end": v(113, 52.5) * mm});
            skPoint(sketch, "E3.21.10.4", {"position": v(115.5, 55) * mm});
            skLineSegment(sketch, "E3.21.11.0", {"start": v(118, 63) * mm, "end": v(113, 63) * mm});
            skLineSegment(sketch, "E3.21.11.1", {"start": v(118, 63) * mm, "end": v(118, 58) * mm});
            skLineSegment(sketch, "E3.21.11.2", {"start": v(118, 58) * mm, "end": v(113, 58) * mm});
            skLineSegment(sketch, "E3.21.11.3", {"start": v(113, 63) * mm, "end": v(113, 58) * mm});
            skPoint(sketch, "E3.21.11.4", {"position": v(115.5, 60.5) * mm});
            skLineSegment(sketch, "E3.21.12.0", {"start": v(118, 68.5) * mm, "end": v(113, 68.5) * mm});
            skLineSegment(sketch, "E3.21.12.1", {"start": v(118, 68.5) * mm, "end": v(118, 63.5) * mm});
            skLineSegment(sketch, "E3.21.12.2", {"start": v(118, 63.5) * mm, "end": v(113, 63.5) * mm});
            skLineSegment(sketch, "E3.21.12.3", {"start": v(113, 68.5) * mm, "end": v(113, 63.5) * mm});
            skPoint(sketch, "E3.21.12.4", {"position": v(115.5, 66) * mm});
            skLineSegment(sketch, "E3.21.13.0", {"start": v(118, 74) * mm, "end": v(113, 74) * mm});
            skLineSegment(sketch, "E3.21.13.1", {"start": v(118, 74) * mm, "end": v(118, 69) * mm});
            skLineSegment(sketch, "E3.21.13.2", {"start": v(118, 69) * mm, "end": v(113, 69) * mm});
            skLineSegment(sketch, "E3.21.13.3", {"start": v(113, 74) * mm, "end": v(113, 69) * mm});
            skPoint(sketch, "E3.21.13.4", {"position": v(115.5, 71.5) * mm});
            skLineSegment(sketch, "E3.21.14.0", {"start": v(118, 79.5) * mm, "end": v(113, 79.5) * mm});
            skLineSegment(sketch, "E3.21.14.1", {"start": v(118, 79.5) * mm, "end": v(118, 74.5) * mm});
            skLineSegment(sketch, "E3.21.14.2", {"start": v(118, 74.5) * mm, "end": v(113, 74.5) * mm});
            skLineSegment(sketch, "E3.21.14.3", {"start": v(113, 79.5) * mm, "end": v(113, 74.5) * mm});
            skPoint(sketch, "E3.21.14.4", {"position": v(115.5, 77) * mm});
            skLineSegment(sketch, "E3.21.15.0", {"start": v(118, 85) * mm, "end": v(113, 85) * mm});
            skLineSegment(sketch, "E3.21.15.1", {"start": v(118, 85) * mm, "end": v(118, 80) * mm});
            skLineSegment(sketch, "E3.21.15.2", {"start": v(118, 80) * mm, "end": v(113, 80) * mm});
            skLineSegment(sketch, "E3.21.15.3", {"start": v(113, 85) * mm, "end": v(113, 80) * mm});
            skPoint(sketch, "E3.21.15.4", {"position": v(115.5, 82.5) * mm});
            skLineSegment(sketch, "E3.21.16.0", {"start": v(118, 90.5) * mm, "end": v(113, 90.5) * mm});
            skLineSegment(sketch, "E3.21.16.1", {"start": v(118, 90.5) * mm, "end": v(118, 85.5) * mm});
            skLineSegment(sketch, "E3.21.16.2", {"start": v(118, 85.5) * mm, "end": v(113, 85.5) * mm});
            skLineSegment(sketch, "E3.21.16.3", {"start": v(113, 90.5) * mm, "end": v(113, 85.5) * mm});
            skPoint(sketch, "E3.21.16.4", {"position": v(115.5, 88) * mm});
            skLineSegment(sketch, "E3.21.17.0", {"start": v(118, 96) * mm, "end": v(113, 96) * mm});
            skLineSegment(sketch, "E3.21.17.1", {"start": v(118, 96) * mm, "end": v(118, 91) * mm});
            skLineSegment(sketch, "E3.21.17.2", {"start": v(118, 91) * mm, "end": v(113, 91) * mm});
            skLineSegment(sketch, "E3.21.17.3", {"start": v(113, 96) * mm, "end": v(113, 91) * mm});
            skPoint(sketch, "E3.21.17.4", {"position": v(115.5, 93.5) * mm});
            skLineSegment(sketch, "E3.21.18.0", {"start": v(118, 101.5) * mm, "end": v(113, 101.5) * mm});
            skLineSegment(sketch, "E3.21.18.1", {"start": v(118, 101.5) * mm, "end": v(118, 96.5) * mm});
            skLineSegment(sketch, "E3.21.18.2", {"start": v(118, 96.5) * mm, "end": v(113, 96.5) * mm});
            skLineSegment(sketch, "E3.21.18.3", {"start": v(113, 101.5) * mm, "end": v(113, 96.5) * mm});
            skPoint(sketch, "E3.21.18.4", {"position": v(115.5, 99) * mm});
            skLineSegment(sketch, "E3.21.19.0", {"start": v(118, 107) * mm, "end": v(113, 107) * mm});
            skLineSegment(sketch, "E3.21.19.1", {"start": v(118, 107) * mm, "end": v(118, 102) * mm});
            skLineSegment(sketch, "E3.21.19.2", {"start": v(118, 102) * mm, "end": v(113, 102) * mm});
            skLineSegment(sketch, "E3.21.19.3", {"start": v(113, 107) * mm, "end": v(113, 102) * mm});
            skPoint(sketch, "E3.21.19.4", {"position": v(115.5, 104.5) * mm});
            skLineSegment(sketch, "E3.21.20.0", {"start": v(118, 112.5) * mm, "end": v(113, 112.5) * mm});
            skLineSegment(sketch, "E3.21.20.1", {"start": v(118, 112.5) * mm, "end": v(118, 107.5) * mm});
            skLineSegment(sketch, "E3.21.20.2", {"start": v(118, 107.5) * mm, "end": v(113, 107.5) * mm});
            skLineSegment(sketch, "E3.21.20.3", {"start": v(113, 112.5) * mm, "end": v(113, 107.5) * mm});
            skPoint(sketch, "E3.21.20.4", {"position": v(115.5, 110) * mm});
            skLineSegment(sketch, "E3.21.21.0", {"start": v(118, 118) * mm, "end": v(113, 118) * mm});
            skLineSegment(sketch, "E3.21.21.1", {"start": v(118, 118) * mm, "end": v(118, 113) * mm});
            skLineSegment(sketch, "E3.21.21.2", {"start": v(118, 113) * mm, "end": v(113, 113) * mm});
            skLineSegment(sketch, "E3.21.21.3", {"start": v(113, 118) * mm, "end": v(113, 113) * mm});
            skPoint(sketch, "E3.21.21.4", {"position": v(115.5, 115.5) * mm});
            skLineSegment(sketch, "E3.21.22.0", {"start": v(118, 123.5) * mm, "end": v(113, 123.5) * mm});
            skLineSegment(sketch, "E3.21.22.1", {"start": v(118, 123.5) * mm, "end": v(118, 118.5) * mm});
            skLineSegment(sketch, "E3.21.22.2", {"start": v(118, 118.5) * mm, "end": v(113, 118.5) * mm});
            skLineSegment(sketch, "E3.21.22.3", {"start": v(113, 123.5) * mm, "end": v(113, 118.5) * mm});
            skPoint(sketch, "E3.21.22.4", {"position": v(115.5, 121) * mm});
            skLineSegment(sketch, "E3.21.23.0", {"start": v(118, 129) * mm, "end": v(113, 129) * mm});
            skLineSegment(sketch, "E3.21.23.1", {"start": v(118, 129) * mm, "end": v(118, 124) * mm});
            skLineSegment(sketch, "E3.21.23.2", {"start": v(118, 124) * mm, "end": v(113, 124) * mm});
            skLineSegment(sketch, "E3.21.23.3", {"start": v(113, 129) * mm, "end": v(113, 124) * mm});
            skPoint(sketch, "E3.21.23.4", {"position": v(115.5, 126.5) * mm});
            skLineSegment(sketch, "E3.21.24.0", {"start": v(118, 134.5) * mm, "end": v(113, 134.5) * mm});
            skLineSegment(sketch, "E3.21.24.1", {"start": v(118, 134.5) * mm, "end": v(118, 129.5) * mm});
            skLineSegment(sketch, "E3.21.24.2", {"start": v(118, 129.5) * mm, "end": v(113, 129.5) * mm});
            skLineSegment(sketch, "E3.21.24.3", {"start": v(113, 134.5) * mm, "end": v(113, 129.5) * mm});
            skPoint(sketch, "E3.21.24.4", {"position": v(115.5, 132) * mm});
            skLineSegment(sketch, "E3.22.0.0", {"start": v(123.5, 2.5) * mm, "end": v(118.5, 2.5) * mm});
            skLineSegment(sketch, "E3.22.0.1", {"start": v(123.5, 2.5) * mm, "end": v(123.5, -2.5) * mm});
            skLineSegment(sketch, "E3.22.0.2", {"start": v(123.5, -2.5) * mm, "end": v(118.5, -2.5) * mm});
            skLineSegment(sketch, "E3.22.0.3", {"start": v(118.5, 2.5) * mm, "end": v(118.5, -2.5) * mm});
            skPoint(sketch, "E3.22.0.4", {"position": v(121, 0) * mm});
            skLineSegment(sketch, "E3.22.1.0", {"start": v(123.5, 8) * mm, "end": v(118.5, 8) * mm});
            skLineSegment(sketch, "E3.22.1.1", {"start": v(123.5, 8) * mm, "end": v(123.5, 3) * mm});
            skLineSegment(sketch, "E3.22.1.2", {"start": v(123.5, 3) * mm, "end": v(118.5, 3) * mm});
            skLineSegment(sketch, "E3.22.1.3", {"start": v(118.5, 8) * mm, "end": v(118.5, 3) * mm});
            skPoint(sketch, "E3.22.1.4", {"position": v(121, 5.5) * mm});
            skLineSegment(sketch, "E3.22.2.0", {"start": v(123.5, 13.5) * mm, "end": v(118.5, 13.5) * mm});
            skLineSegment(sketch, "E3.22.2.1", {"start": v(123.5, 13.5) * mm, "end": v(123.5, 8.5) * mm});
            skLineSegment(sketch, "E3.22.2.2", {"start": v(123.5, 8.5) * mm, "end": v(118.5, 8.5) * mm});
            skLineSegment(sketch, "E3.22.2.3", {"start": v(118.5, 13.5) * mm, "end": v(118.5, 8.5) * mm});
            skPoint(sketch, "E3.22.2.4", {"position": v(121, 11) * mm});
            skLineSegment(sketch, "E3.22.3.0", {"start": v(123.5, 19) * mm, "end": v(118.5, 19) * mm});
            skLineSegment(sketch, "E3.22.3.1", {"start": v(123.5, 19) * mm, "end": v(123.5, 14) * mm});
            skLineSegment(sketch, "E3.22.3.2", {"start": v(123.5, 14) * mm, "end": v(118.5, 14) * mm});
            skLineSegment(sketch, "E3.22.3.3", {"start": v(118.5, 19) * mm, "end": v(118.5, 14) * mm});
            skPoint(sketch, "E3.22.3.4", {"position": v(121, 16.5) * mm});
            skLineSegment(sketch, "E3.22.4.0", {"start": v(123.5, 24.5) * mm, "end": v(118.5, 24.5) * mm});
            skLineSegment(sketch, "E3.22.4.1", {"start": v(123.5, 24.5) * mm, "end": v(123.5, 19.5) * mm});
            skLineSegment(sketch, "E3.22.4.2", {"start": v(123.5, 19.5) * mm, "end": v(118.5, 19.5) * mm});
            skLineSegment(sketch, "E3.22.4.3", {"start": v(118.5, 24.5) * mm, "end": v(118.5, 19.5) * mm});
            skPoint(sketch, "E3.22.4.4", {"position": v(121, 22) * mm});
            skLineSegment(sketch, "E3.22.5.0", {"start": v(123.5, 30) * mm, "end": v(118.5, 30) * mm});
            skLineSegment(sketch, "E3.22.5.1", {"start": v(123.5, 30) * mm, "end": v(123.5, 25) * mm});
            skLineSegment(sketch, "E3.22.5.2", {"start": v(123.5, 25) * mm, "end": v(118.5, 25) * mm});
            skLineSegment(sketch, "E3.22.5.3", {"start": v(118.5, 30) * mm, "end": v(118.5, 25) * mm});
            skPoint(sketch, "E3.22.5.4", {"position": v(121, 27.5) * mm});
            skLineSegment(sketch, "E3.22.6.0", {"start": v(123.5, 35.5) * mm, "end": v(118.5, 35.5) * mm});
            skLineSegment(sketch, "E3.22.6.1", {"start": v(123.5, 35.5) * mm, "end": v(123.5, 30.5) * mm});
            skLineSegment(sketch, "E3.22.6.2", {"start": v(123.5, 30.5) * mm, "end": v(118.5, 30.5) * mm});
            skLineSegment(sketch, "E3.22.6.3", {"start": v(118.5, 35.5) * mm, "end": v(118.5, 30.5) * mm});
            skPoint(sketch, "E3.22.6.4", {"position": v(121, 33) * mm});
            skLineSegment(sketch, "E3.22.7.0", {"start": v(123.5, 41) * mm, "end": v(118.5, 41) * mm});
            skLineSegment(sketch, "E3.22.7.1", {"start": v(123.5, 41) * mm, "end": v(123.5, 36) * mm});
            skLineSegment(sketch, "E3.22.7.2", {"start": v(123.5, 36) * mm, "end": v(118.5, 36) * mm});
            skLineSegment(sketch, "E3.22.7.3", {"start": v(118.5, 41) * mm, "end": v(118.5, 36) * mm});
            skPoint(sketch, "E3.22.7.4", {"position": v(121, 38.5) * mm});
            skLineSegment(sketch, "E3.22.8.0", {"start": v(123.5, 46.5) * mm, "end": v(118.5, 46.5) * mm});
            skLineSegment(sketch, "E3.22.8.1", {"start": v(123.5, 46.5) * mm, "end": v(123.5, 41.5) * mm});
            skLineSegment(sketch, "E3.22.8.2", {"start": v(123.5, 41.5) * mm, "end": v(118.5, 41.5) * mm});
            skLineSegment(sketch, "E3.22.8.3", {"start": v(118.5, 46.5) * mm, "end": v(118.5, 41.5) * mm});
            skPoint(sketch, "E3.22.8.4", {"position": v(121, 44) * mm});
            skLineSegment(sketch, "E3.22.9.0", {"start": v(123.5, 52) * mm, "end": v(118.5, 52) * mm});
            skLineSegment(sketch, "E3.22.9.1", {"start": v(123.5, 52) * mm, "end": v(123.5, 47) * mm});
            skLineSegment(sketch, "E3.22.9.2", {"start": v(123.5, 47) * mm, "end": v(118.5, 47) * mm});
            skLineSegment(sketch, "E3.22.9.3", {"start": v(118.5, 52) * mm, "end": v(118.5, 47) * mm});
            skPoint(sketch, "E3.22.9.4", {"position": v(121, 49.5) * mm});
            skLineSegment(sketch, "E3.22.10.0", {"start": v(123.5, 57.5) * mm, "end": v(118.5, 57.5) * mm});
            skLineSegment(sketch, "E3.22.10.1", {"start": v(123.5, 57.5) * mm, "end": v(123.5, 52.5) * mm});
            skLineSegment(sketch, "E3.22.10.2", {"start": v(123.5, 52.5) * mm, "end": v(118.5, 52.5) * mm});
            skLineSegment(sketch, "E3.22.10.3", {"start": v(118.5, 57.5) * mm, "end": v(118.5, 52.5) * mm});
            skPoint(sketch, "E3.22.10.4", {"position": v(121, 55) * mm});
            skLineSegment(sketch, "E3.22.11.0", {"start": v(123.5, 63) * mm, "end": v(118.5, 63) * mm});
            skLineSegment(sketch, "E3.22.11.1", {"start": v(123.5, 63) * mm, "end": v(123.5, 58) * mm});
            skLineSegment(sketch, "E3.22.11.2", {"start": v(123.5, 58) * mm, "end": v(118.5, 58) * mm});
            skLineSegment(sketch, "E3.22.11.3", {"start": v(118.5, 63) * mm, "end": v(118.5, 58) * mm});
            skPoint(sketch, "E3.22.11.4", {"position": v(121, 60.5) * mm});
            skLineSegment(sketch, "E3.22.12.0", {"start": v(123.5, 68.5) * mm, "end": v(118.5, 68.5) * mm});
            skLineSegment(sketch, "E3.22.12.1", {"start": v(123.5, 68.5) * mm, "end": v(123.5, 63.5) * mm});
            skLineSegment(sketch, "E3.22.12.2", {"start": v(123.5, 63.5) * mm, "end": v(118.5, 63.5) * mm});
            skLineSegment(sketch, "E3.22.12.3", {"start": v(118.5, 68.5) * mm, "end": v(118.5, 63.5) * mm});
            skPoint(sketch, "E3.22.12.4", {"position": v(121, 66) * mm});
            skLineSegment(sketch, "E3.22.13.0", {"start": v(123.5, 74) * mm, "end": v(118.5, 74) * mm});
            skLineSegment(sketch, "E3.22.13.1", {"start": v(123.5, 74) * mm, "end": v(123.5, 69) * mm});
            skLineSegment(sketch, "E3.22.13.2", {"start": v(123.5, 69) * mm, "end": v(118.5, 69) * mm});
            skLineSegment(sketch, "E3.22.13.3", {"start": v(118.5, 74) * mm, "end": v(118.5, 69) * mm});
            skPoint(sketch, "E3.22.13.4", {"position": v(121, 71.5) * mm});
            skLineSegment(sketch, "E3.22.14.0", {"start": v(123.5, 79.5) * mm, "end": v(118.5, 79.5) * mm});
            skLineSegment(sketch, "E3.22.14.1", {"start": v(123.5, 79.5) * mm, "end": v(123.5, 74.5) * mm});
            skLineSegment(sketch, "E3.22.14.2", {"start": v(123.5, 74.5) * mm, "end": v(118.5, 74.5) * mm});
            skLineSegment(sketch, "E3.22.14.3", {"start": v(118.5, 79.5) * mm, "end": v(118.5, 74.5) * mm});
            skPoint(sketch, "E3.22.14.4", {"position": v(121, 77) * mm});
            skLineSegment(sketch, "E3.22.15.0", {"start": v(123.5, 85) * mm, "end": v(118.5, 85) * mm});
            skLineSegment(sketch, "E3.22.15.1", {"start": v(123.5, 85) * mm, "end": v(123.5, 80) * mm});
            skLineSegment(sketch, "E3.22.15.2", {"start": v(123.5, 80) * mm, "end": v(118.5, 80) * mm});
            skLineSegment(sketch, "E3.22.15.3", {"start": v(118.5, 85) * mm, "end": v(118.5, 80) * mm});
            skPoint(sketch, "E3.22.15.4", {"position": v(121, 82.5) * mm});
            skLineSegment(sketch, "E3.22.16.0", {"start": v(123.5, 90.5) * mm, "end": v(118.5, 90.5) * mm});
            skLineSegment(sketch, "E3.22.16.1", {"start": v(123.5, 90.5) * mm, "end": v(123.5, 85.5) * mm});
            skLineSegment(sketch, "E3.22.16.2", {"start": v(123.5, 85.5) * mm, "end": v(118.5, 85.5) * mm});
            skLineSegment(sketch, "E3.22.16.3", {"start": v(118.5, 90.5) * mm, "end": v(118.5, 85.5) * mm});
            skPoint(sketch, "E3.22.16.4", {"position": v(121, 88) * mm});
            skLineSegment(sketch, "E3.22.17.0", {"start": v(123.5, 96) * mm, "end": v(118.5, 96) * mm});
            skLineSegment(sketch, "E3.22.17.1", {"start": v(123.5, 96) * mm, "end": v(123.5, 91) * mm});
            skLineSegment(sketch, "E3.22.17.2", {"start": v(123.5, 91) * mm, "end": v(118.5, 91) * mm});
            skLineSegment(sketch, "E3.22.17.3", {"start": v(118.5, 96) * mm, "end": v(118.5, 91) * mm});
            skPoint(sketch, "E3.22.17.4", {"position": v(121, 93.5) * mm});
            skLineSegment(sketch, "E3.22.18.0", {"start": v(123.5, 101.5) * mm, "end": v(118.5, 101.5) * mm});
            skLineSegment(sketch, "E3.22.18.1", {"start": v(123.5, 101.5) * mm, "end": v(123.5, 96.5) * mm});
            skLineSegment(sketch, "E3.22.18.2", {"start": v(123.5, 96.5) * mm, "end": v(118.5, 96.5) * mm});
            skLineSegment(sketch, "E3.22.18.3", {"start": v(118.5, 101.5) * mm, "end": v(118.5, 96.5) * mm});
            skPoint(sketch, "E3.22.18.4", {"position": v(121, 99) * mm});
            skLineSegment(sketch, "E3.22.19.0", {"start": v(123.5, 107) * mm, "end": v(118.5, 107) * mm});
            skLineSegment(sketch, "E3.22.19.1", {"start": v(123.5, 107) * mm, "end": v(123.5, 102) * mm});
            skLineSegment(sketch, "E3.22.19.2", {"start": v(123.5, 102) * mm, "end": v(118.5, 102) * mm});
            skLineSegment(sketch, "E3.22.19.3", {"start": v(118.5, 107) * mm, "end": v(118.5, 102) * mm});
            skPoint(sketch, "E3.22.19.4", {"position": v(121, 104.5) * mm});
            skLineSegment(sketch, "E3.22.20.0", {"start": v(123.5, 112.5) * mm, "end": v(118.5, 112.5) * mm});
            skLineSegment(sketch, "E3.22.20.1", {"start": v(123.5, 112.5) * mm, "end": v(123.5, 107.5) * mm});
            skLineSegment(sketch, "E3.22.20.2", {"start": v(123.5, 107.5) * mm, "end": v(118.5, 107.5) * mm});
            skLineSegment(sketch, "E3.22.20.3", {"start": v(118.5, 112.5) * mm, "end": v(118.5, 107.5) * mm});
            skPoint(sketch, "E3.22.20.4", {"position": v(121, 110) * mm});
            skLineSegment(sketch, "E3.22.21.0", {"start": v(123.5, 118) * mm, "end": v(118.5, 118) * mm});
            skLineSegment(sketch, "E3.22.21.1", {"start": v(123.5, 118) * mm, "end": v(123.5, 113) * mm});
            skLineSegment(sketch, "E3.22.21.2", {"start": v(123.5, 113) * mm, "end": v(118.5, 113) * mm});
            skLineSegment(sketch, "E3.22.21.3", {"start": v(118.5, 118) * mm, "end": v(118.5, 113) * mm});
            skPoint(sketch, "E3.22.21.4", {"position": v(121, 115.5) * mm});
            skLineSegment(sketch, "E3.22.22.0", {"start": v(123.5, 123.5) * mm, "end": v(118.5, 123.5) * mm});
            skLineSegment(sketch, "E3.22.22.1", {"start": v(123.5, 123.5) * mm, "end": v(123.5, 118.5) * mm});
            skLineSegment(sketch, "E3.22.22.2", {"start": v(123.5, 118.5) * mm, "end": v(118.5, 118.5) * mm});
            skLineSegment(sketch, "E3.22.22.3", {"start": v(118.5, 123.5) * mm, "end": v(118.5, 118.5) * mm});
            skPoint(sketch, "E3.22.22.4", {"position": v(121, 121) * mm});
            skLineSegment(sketch, "E3.22.23.0", {"start": v(123.5, 129) * mm, "end": v(118.5, 129) * mm});
            skLineSegment(sketch, "E3.22.23.1", {"start": v(123.5, 129) * mm, "end": v(123.5, 124) * mm});
            skLineSegment(sketch, "E3.22.23.2", {"start": v(123.5, 124) * mm, "end": v(118.5, 124) * mm});
            skLineSegment(sketch, "E3.22.23.3", {"start": v(118.5, 129) * mm, "end": v(118.5, 124) * mm});
            skPoint(sketch, "E3.22.23.4", {"position": v(121, 126.5) * mm});
            skLineSegment(sketch, "E3.22.24.0", {"start": v(123.5, 134.5) * mm, "end": v(118.5, 134.5) * mm});
            skLineSegment(sketch, "E3.22.24.1", {"start": v(123.5, 134.5) * mm, "end": v(123.5, 129.5) * mm});
            skLineSegment(sketch, "E3.22.24.2", {"start": v(123.5, 129.5) * mm, "end": v(118.5, 129.5) * mm});
            skLineSegment(sketch, "E3.22.24.3", {"start": v(118.5, 134.5) * mm, "end": v(118.5, 129.5) * mm});
            skPoint(sketch, "E3.22.24.4", {"position": v(121, 132) * mm});
            skLineSegment(sketch, "E3.23.0.0", {"start": v(129, 2.5) * mm, "end": v(124, 2.5) * mm});
            skLineSegment(sketch, "E3.23.0.1", {"start": v(129, 2.5) * mm, "end": v(129, -2.5) * mm});
            skLineSegment(sketch, "E3.23.0.2", {"start": v(129, -2.5) * mm, "end": v(124, -2.5) * mm});
            skLineSegment(sketch, "E3.23.0.3", {"start": v(124, 2.5) * mm, "end": v(124, -2.5) * mm});
            skPoint(sketch, "E3.23.0.4", {"position": v(126.5, 0) * mm});
            skLineSegment(sketch, "E3.23.1.0", {"start": v(129, 8) * mm, "end": v(124, 8) * mm});
            skLineSegment(sketch, "E3.23.1.1", {"start": v(129, 8) * mm, "end": v(129, 3) * mm});
            skLineSegment(sketch, "E3.23.1.2", {"start": v(129, 3) * mm, "end": v(124, 3) * mm});
            skLineSegment(sketch, "E3.23.1.3", {"start": v(124, 8) * mm, "end": v(124, 3) * mm});
            skPoint(sketch, "E3.23.1.4", {"position": v(126.5, 5.5) * mm});
            skLineSegment(sketch, "E3.23.2.0", {"start": v(129, 13.5) * mm, "end": v(124, 13.5) * mm});
            skLineSegment(sketch, "E3.23.2.1", {"start": v(129, 13.5) * mm, "end": v(129, 8.5) * mm});
            skLineSegment(sketch, "E3.23.2.2", {"start": v(129, 8.5) * mm, "end": v(124, 8.5) * mm});
            skLineSegment(sketch, "E3.23.2.3", {"start": v(124, 13.5) * mm, "end": v(124, 8.5) * mm});
            skPoint(sketch, "E3.23.2.4", {"position": v(126.5, 11) * mm});
            skLineSegment(sketch, "E3.23.3.0", {"start": v(129, 19) * mm, "end": v(124, 19) * mm});
            skLineSegment(sketch, "E3.23.3.1", {"start": v(129, 19) * mm, "end": v(129, 14) * mm});
            skLineSegment(sketch, "E3.23.3.2", {"start": v(129, 14) * mm, "end": v(124, 14) * mm});
            skLineSegment(sketch, "E3.23.3.3", {"start": v(124, 19) * mm, "end": v(124, 14) * mm});
            skPoint(sketch, "E3.23.3.4", {"position": v(126.5, 16.5) * mm});
            skLineSegment(sketch, "E3.23.4.0", {"start": v(129, 24.5) * mm, "end": v(124, 24.5) * mm});
            skLineSegment(sketch, "E3.23.4.1", {"start": v(129, 24.5) * mm, "end": v(129, 19.5) * mm});
            skLineSegment(sketch, "E3.23.4.2", {"start": v(129, 19.5) * mm, "end": v(124, 19.5) * mm});
            skLineSegment(sketch, "E3.23.4.3", {"start": v(124, 24.5) * mm, "end": v(124, 19.5) * mm});
            skPoint(sketch, "E3.23.4.4", {"position": v(126.5, 22) * mm});
            skLineSegment(sketch, "E3.23.5.0", {"start": v(129, 30) * mm, "end": v(124, 30) * mm});
            skLineSegment(sketch, "E3.23.5.1", {"start": v(129, 30) * mm, "end": v(129, 25) * mm});
            skLineSegment(sketch, "E3.23.5.2", {"start": v(129, 25) * mm, "end": v(124, 25) * mm});
            skLineSegment(sketch, "E3.23.5.3", {"start": v(124, 30) * mm, "end": v(124, 25) * mm});
            skPoint(sketch, "E3.23.5.4", {"position": v(126.5, 27.5) * mm});
            skLineSegment(sketch, "E3.23.6.0", {"start": v(129, 35.5) * mm, "end": v(124, 35.5) * mm});
            skLineSegment(sketch, "E3.23.6.1", {"start": v(129, 35.5) * mm, "end": v(129, 30.5) * mm});
            skLineSegment(sketch, "E3.23.6.2", {"start": v(129, 30.5) * mm, "end": v(124, 30.5) * mm});
            skLineSegment(sketch, "E3.23.6.3", {"start": v(124, 35.5) * mm, "end": v(124, 30.5) * mm});
            skPoint(sketch, "E3.23.6.4", {"position": v(126.5, 33) * mm});
            skLineSegment(sketch, "E3.23.7.0", {"start": v(129, 41) * mm, "end": v(124, 41) * mm});
            skLineSegment(sketch, "E3.23.7.1", {"start": v(129, 41) * mm, "end": v(129, 36) * mm});
            skLineSegment(sketch, "E3.23.7.2", {"start": v(129, 36) * mm, "end": v(124, 36) * mm});
            skLineSegment(sketch, "E3.23.7.3", {"start": v(124, 41) * mm, "end": v(124, 36) * mm});
            skPoint(sketch, "E3.23.7.4", {"position": v(126.5, 38.5) * mm});
            skLineSegment(sketch, "E3.23.8.0", {"start": v(129, 46.5) * mm, "end": v(124, 46.5) * mm});
            skLineSegment(sketch, "E3.23.8.1", {"start": v(129, 46.5) * mm, "end": v(129, 41.5) * mm});
            skLineSegment(sketch, "E3.23.8.2", {"start": v(129, 41.5) * mm, "end": v(124, 41.5) * mm});
            skLineSegment(sketch, "E3.23.8.3", {"start": v(124, 46.5) * mm, "end": v(124, 41.5) * mm});
            skPoint(sketch, "E3.23.8.4", {"position": v(126.5, 44) * mm});
            skLineSegment(sketch, "E3.23.9.0", {"start": v(129, 52) * mm, "end": v(124, 52) * mm});
            skLineSegment(sketch, "E3.23.9.1", {"start": v(129, 52) * mm, "end": v(129, 47) * mm});
            skLineSegment(sketch, "E3.23.9.2", {"start": v(129, 47) * mm, "end": v(124, 47) * mm});
            skLineSegment(sketch, "E3.23.9.3", {"start": v(124, 52) * mm, "end": v(124, 47) * mm});
            skPoint(sketch, "E3.23.9.4", {"position": v(126.5, 49.5) * mm});
            skLineSegment(sketch, "E3.23.10.0", {"start": v(129, 57.5) * mm, "end": v(124, 57.5) * mm});
            skLineSegment(sketch, "E3.23.10.1", {"start": v(129, 57.5) * mm, "end": v(129, 52.5) * mm});
            skLineSegment(sketch, "E3.23.10.2", {"start": v(129, 52.5) * mm, "end": v(124, 52.5) * mm});
            skLineSegment(sketch, "E3.23.10.3", {"start": v(124, 57.5) * mm, "end": v(124, 52.5) * mm});
            skPoint(sketch, "E3.23.10.4", {"position": v(126.5, 55) * mm});
            skLineSegment(sketch, "E3.23.11.0", {"start": v(129, 63) * mm, "end": v(124, 63) * mm});
            skLineSegment(sketch, "E3.23.11.1", {"start": v(129, 63) * mm, "end": v(129, 58) * mm});
            skLineSegment(sketch, "E3.23.11.2", {"start": v(129, 58) * mm, "end": v(124, 58) * mm});
            skLineSegment(sketch, "E3.23.11.3", {"start": v(124, 63) * mm, "end": v(124, 58) * mm});
            skPoint(sketch, "E3.23.11.4", {"position": v(126.5, 60.5) * mm});
            skLineSegment(sketch, "E3.23.12.0", {"start": v(129, 68.5) * mm, "end": v(124, 68.5) * mm});
            skLineSegment(sketch, "E3.23.12.1", {"start": v(129, 68.5) * mm, "end": v(129, 63.5) * mm});
            skLineSegment(sketch, "E3.23.12.2", {"start": v(129, 63.5) * mm, "end": v(124, 63.5) * mm});
            skLineSegment(sketch, "E3.23.12.3", {"start": v(124, 68.5) * mm, "end": v(124, 63.5) * mm});
            skPoint(sketch, "E3.23.12.4", {"position": v(126.5, 66) * mm});
            skLineSegment(sketch, "E3.23.13.0", {"start": v(129, 74) * mm, "end": v(124, 74) * mm});
            skLineSegment(sketch, "E3.23.13.1", {"start": v(129, 74) * mm, "end": v(129, 69) * mm});
            skLineSegment(sketch, "E3.23.13.2", {"start": v(129, 69) * mm, "end": v(124, 69) * mm});
            skLineSegment(sketch, "E3.23.13.3", {"start": v(124, 74) * mm, "end": v(124, 69) * mm});
            skPoint(sketch, "E3.23.13.4", {"position": v(126.5, 71.5) * mm});
            skLineSegment(sketch, "E3.23.14.0", {"start": v(129, 79.5) * mm, "end": v(124, 79.5) * mm});
            skLineSegment(sketch, "E3.23.14.1", {"start": v(129, 79.5) * mm, "end": v(129, 74.5) * mm});
            skLineSegment(sketch, "E3.23.14.2", {"start": v(129, 74.5) * mm, "end": v(124, 74.5) * mm});
            skLineSegment(sketch, "E3.23.14.3", {"start": v(124, 79.5) * mm, "end": v(124, 74.5) * mm});
            skPoint(sketch, "E3.23.14.4", {"position": v(126.5, 77) * mm});
            skLineSegment(sketch, "E3.23.15.0", {"start": v(129, 85) * mm, "end": v(124, 85) * mm});
            skLineSegment(sketch, "E3.23.15.1", {"start": v(129, 85) * mm, "end": v(129, 80) * mm});
            skLineSegment(sketch, "E3.23.15.2", {"start": v(129, 80) * mm, "end": v(124, 80) * mm});
            skLineSegment(sketch, "E3.23.15.3", {"start": v(124, 85) * mm, "end": v(124, 80) * mm});
            skPoint(sketch, "E3.23.15.4", {"position": v(126.5, 82.5) * mm});
            skLineSegment(sketch, "E3.23.16.0", {"start": v(129, 90.5) * mm, "end": v(124, 90.5) * mm});
            skLineSegment(sketch, "E3.23.16.1", {"start": v(129, 90.5) * mm, "end": v(129, 85.5) * mm});
            skLineSegment(sketch, "E3.23.16.2", {"start": v(129, 85.5) * mm, "end": v(124, 85.5) * mm});
            skLineSegment(sketch, "E3.23.16.3", {"start": v(124, 90.5) * mm, "end": v(124, 85.5) * mm});
            skPoint(sketch, "E3.23.16.4", {"position": v(126.5, 88) * mm});
            skLineSegment(sketch, "E3.23.17.0", {"start": v(129, 96) * mm, "end": v(124, 96) * mm});
            skLineSegment(sketch, "E3.23.17.1", {"start": v(129, 96) * mm, "end": v(129, 91) * mm});
            skLineSegment(sketch, "E3.23.17.2", {"start": v(129, 91) * mm, "end": v(124, 91) * mm});
            skLineSegment(sketch, "E3.23.17.3", {"start": v(124, 96) * mm, "end": v(124, 91) * mm});
            skPoint(sketch, "E3.23.17.4", {"position": v(126.5, 93.5) * mm});
            skLineSegment(sketch, "E3.23.18.0", {"start": v(129, 101.5) * mm, "end": v(124, 101.5) * mm});
            skLineSegment(sketch, "E3.23.18.1", {"start": v(129, 101.5) * mm, "end": v(129, 96.5) * mm});
            skLineSegment(sketch, "E3.23.18.2", {"start": v(129, 96.5) * mm, "end": v(124, 96.5) * mm});
            skLineSegment(sketch, "E3.23.18.3", {"start": v(124, 101.5) * mm, "end": v(124, 96.5) * mm});
            skPoint(sketch, "E3.23.18.4", {"position": v(126.5, 99) * mm});
            skLineSegment(sketch, "E3.23.19.0", {"start": v(129, 107) * mm, "end": v(124, 107) * mm});
            skLineSegment(sketch, "E3.23.19.1", {"start": v(129, 107) * mm, "end": v(129, 102) * mm});
            skLineSegment(sketch, "E3.23.19.2", {"start": v(129, 102) * mm, "end": v(124, 102) * mm});
            skLineSegment(sketch, "E3.23.19.3", {"start": v(124, 107) * mm, "end": v(124, 102) * mm});
            skPoint(sketch, "E3.23.19.4", {"position": v(126.5, 104.5) * mm});
            skLineSegment(sketch, "E3.23.20.0", {"start": v(129, 112.5) * mm, "end": v(124, 112.5) * mm});
            skLineSegment(sketch, "E3.23.20.1", {"start": v(129, 112.5) * mm, "end": v(129, 107.5) * mm});
            skLineSegment(sketch, "E3.23.20.2", {"start": v(129, 107.5) * mm, "end": v(124, 107.5) * mm});
            skLineSegment(sketch, "E3.23.20.3", {"start": v(124, 112.5) * mm, "end": v(124, 107.5) * mm});
            skPoint(sketch, "E3.23.20.4", {"position": v(126.5, 110) * mm});
            skLineSegment(sketch, "E3.23.21.0", {"start": v(129, 118) * mm, "end": v(124, 118) * mm});
            skLineSegment(sketch, "E3.23.21.1", {"start": v(129, 118) * mm, "end": v(129, 113) * mm});
            skLineSegment(sketch, "E3.23.21.2", {"start": v(129, 113) * mm, "end": v(124, 113) * mm});
            skLineSegment(sketch, "E3.23.21.3", {"start": v(124, 118) * mm, "end": v(124, 113) * mm});
            skPoint(sketch, "E3.23.21.4", {"position": v(126.5, 115.5) * mm});
            skLineSegment(sketch, "E3.23.22.0", {"start": v(129, 123.5) * mm, "end": v(124, 123.5) * mm});
            skLineSegment(sketch, "E3.23.22.1", {"start": v(129, 123.5) * mm, "end": v(129, 118.5) * mm});
            skLineSegment(sketch, "E3.23.22.2", {"start": v(129, 118.5) * mm, "end": v(124, 118.5) * mm});
            skLineSegment(sketch, "E3.23.22.3", {"start": v(124, 123.5) * mm, "end": v(124, 118.5) * mm});
            skPoint(sketch, "E3.23.22.4", {"position": v(126.5, 121) * mm});
            skLineSegment(sketch, "E3.23.23.0", {"start": v(129, 129) * mm, "end": v(124, 129) * mm});
            skLineSegment(sketch, "E3.23.23.1", {"start": v(129, 129) * mm, "end": v(129, 124) * mm});
            skLineSegment(sketch, "E3.23.23.2", {"start": v(129, 124) * mm, "end": v(124, 124) * mm});
            skLineSegment(sketch, "E3.23.23.3", {"start": v(124, 129) * mm, "end": v(124, 124) * mm});
            skPoint(sketch, "E3.23.23.4", {"position": v(126.5, 126.5) * mm});
            skLineSegment(sketch, "E3.23.24.0", {"start": v(129, 134.5) * mm, "end": v(124, 134.5) * mm});
            skLineSegment(sketch, "E3.23.24.1", {"start": v(129, 134.5) * mm, "end": v(129, 129.5) * mm});
            skLineSegment(sketch, "E3.23.24.2", {"start": v(129, 129.5) * mm, "end": v(124, 129.5) * mm});
            skLineSegment(sketch, "E3.23.24.3", {"start": v(124, 134.5) * mm, "end": v(124, 129.5) * mm});
            skPoint(sketch, "E3.23.24.4", {"position": v(126.5, 132) * mm});
            skLineSegment(sketch, "E3.24.0.0", {"start": v(134.5, 2.5) * mm, "end": v(129.5, 2.5) * mm});
            skLineSegment(sketch, "E3.24.0.1", {"start": v(134.5, 2.5) * mm, "end": v(134.5, -2.5) * mm});
            skLineSegment(sketch, "E3.24.0.2", {"start": v(134.5, -2.5) * mm, "end": v(129.5, -2.5) * mm});
            skLineSegment(sketch, "E3.24.0.3", {"start": v(129.5, 2.5) * mm, "end": v(129.5, -2.5) * mm});
            skPoint(sketch, "E3.24.0.4", {"position": v(132, 0) * mm});
            skLineSegment(sketch, "E3.24.1.0", {"start": v(134.5, 8) * mm, "end": v(129.5, 8) * mm});
            skLineSegment(sketch, "E3.24.1.1", {"start": v(134.5, 8) * mm, "end": v(134.5, 3) * mm});
            skLineSegment(sketch, "E3.24.1.2", {"start": v(134.5, 3) * mm, "end": v(129.5, 3) * mm});
            skLineSegment(sketch, "E3.24.1.3", {"start": v(129.5, 8) * mm, "end": v(129.5, 3) * mm});
            skPoint(sketch, "E3.24.1.4", {"position": v(132, 5.5) * mm});
            skLineSegment(sketch, "E3.24.2.0", {"start": v(134.5, 13.5) * mm, "end": v(129.5, 13.5) * mm});
            skLineSegment(sketch, "E3.24.2.1", {"start": v(134.5, 13.5) * mm, "end": v(134.5, 8.5) * mm});
            skLineSegment(sketch, "E3.24.2.2", {"start": v(134.5, 8.5) * mm, "end": v(129.5, 8.5) * mm});
            skLineSegment(sketch, "E3.24.2.3", {"start": v(129.5, 13.5) * mm, "end": v(129.5, 8.5) * mm});
            skPoint(sketch, "E3.24.2.4", {"position": v(132, 11) * mm});
            skLineSegment(sketch, "E3.24.3.0", {"start": v(134.5, 19) * mm, "end": v(129.5, 19) * mm});
            skLineSegment(sketch, "E3.24.3.1", {"start": v(134.5, 19) * mm, "end": v(134.5, 14) * mm});
            skLineSegment(sketch, "E3.24.3.2", {"start": v(134.5, 14) * mm, "end": v(129.5, 14) * mm});
            skLineSegment(sketch, "E3.24.3.3", {"start": v(129.5, 19) * mm, "end": v(129.5, 14) * mm});
            skPoint(sketch, "E3.24.3.4", {"position": v(132, 16.5) * mm});
            skLineSegment(sketch, "E3.24.4.0", {"start": v(134.5, 24.5) * mm, "end": v(129.5, 24.5) * mm});
            skLineSegment(sketch, "E3.24.4.1", {"start": v(134.5, 24.5) * mm, "end": v(134.5, 19.5) * mm});
            skLineSegment(sketch, "E3.24.4.2", {"start": v(134.5, 19.5) * mm, "end": v(129.5, 19.5) * mm});
            skLineSegment(sketch, "E3.24.4.3", {"start": v(129.5, 24.5) * mm, "end": v(129.5, 19.5) * mm});
            skPoint(sketch, "E3.24.4.4", {"position": v(132, 22) * mm});
            skLineSegment(sketch, "E3.24.5.0", {"start": v(134.5, 30) * mm, "end": v(129.5, 30) * mm});
            skLineSegment(sketch, "E3.24.5.1", {"start": v(134.5, 30) * mm, "end": v(134.5, 25) * mm});
            skLineSegment(sketch, "E3.24.5.2", {"start": v(134.5, 25) * mm, "end": v(129.5, 25) * mm});
            skLineSegment(sketch, "E3.24.5.3", {"start": v(129.5, 30) * mm, "end": v(129.5, 25) * mm});
            skPoint(sketch, "E3.24.5.4", {"position": v(132, 27.5) * mm});
            skLineSegment(sketch, "E3.24.6.0", {"start": v(134.5, 35.5) * mm, "end": v(129.5, 35.5) * mm});
            skLineSegment(sketch, "E3.24.6.1", {"start": v(134.5, 35.5) * mm, "end": v(134.5, 30.5) * mm});
            skLineSegment(sketch, "E3.24.6.2", {"start": v(134.5, 30.5) * mm, "end": v(129.5, 30.5) * mm});
            skLineSegment(sketch, "E3.24.6.3", {"start": v(129.5, 35.5) * mm, "end": v(129.5, 30.5) * mm});
            skPoint(sketch, "E3.24.6.4", {"position": v(132, 33) * mm});
            skLineSegment(sketch, "E3.24.7.0", {"start": v(134.5, 41) * mm, "end": v(129.5, 41) * mm});
            skLineSegment(sketch, "E3.24.7.1", {"start": v(134.5, 41) * mm, "end": v(134.5, 36) * mm});
            skLineSegment(sketch, "E3.24.7.2", {"start": v(134.5, 36) * mm, "end": v(129.5, 36) * mm});
            skLineSegment(sketch, "E3.24.7.3", {"start": v(129.5, 41) * mm, "end": v(129.5, 36) * mm});
            skPoint(sketch, "E3.24.7.4", {"position": v(132, 38.5) * mm});
            skLineSegment(sketch, "E3.24.8.0", {"start": v(134.5, 46.5) * mm, "end": v(129.5, 46.5) * mm});
            skLineSegment(sketch, "E3.24.8.1", {"start": v(134.5, 46.5) * mm, "end": v(134.5, 41.5) * mm});
            skLineSegment(sketch, "E3.24.8.2", {"start": v(134.5, 41.5) * mm, "end": v(129.5, 41.5) * mm});
            skLineSegment(sketch, "E3.24.8.3", {"start": v(129.5, 46.5) * mm, "end": v(129.5, 41.5) * mm});
            skPoint(sketch, "E3.24.8.4", {"position": v(132, 44) * mm});
            skLineSegment(sketch, "E3.24.9.0", {"start": v(134.5, 52) * mm, "end": v(129.5, 52) * mm});
            skLineSegment(sketch, "E3.24.9.1", {"start": v(134.5, 52) * mm, "end": v(134.5, 47) * mm});
            skLineSegment(sketch, "E3.24.9.2", {"start": v(134.5, 47) * mm, "end": v(129.5, 47) * mm});
            skLineSegment(sketch, "E3.24.9.3", {"start": v(129.5, 52) * mm, "end": v(129.5, 47) * mm});
            skPoint(sketch, "E3.24.9.4", {"position": v(132, 49.5) * mm});
            skLineSegment(sketch, "E3.24.10.0", {"start": v(134.5, 57.5) * mm, "end": v(129.5, 57.5) * mm});
            skLineSegment(sketch, "E3.24.10.1", {"start": v(134.5, 57.5) * mm, "end": v(134.5, 52.5) * mm});
            skLineSegment(sketch, "E3.24.10.2", {"start": v(134.5, 52.5) * mm, "end": v(129.5, 52.5) * mm});
            skLineSegment(sketch, "E3.24.10.3", {"start": v(129.5, 57.5) * mm, "end": v(129.5, 52.5) * mm});
            skPoint(sketch, "E3.24.10.4", {"position": v(132, 55) * mm});
            skLineSegment(sketch, "E3.24.11.0", {"start": v(134.5, 63) * mm, "end": v(129.5, 63) * mm});
            skLineSegment(sketch, "E3.24.11.1", {"start": v(134.5, 63) * mm, "end": v(134.5, 58) * mm});
            skLineSegment(sketch, "E3.24.11.2", {"start": v(134.5, 58) * mm, "end": v(129.5, 58) * mm});
            skLineSegment(sketch, "E3.24.11.3", {"start": v(129.5, 63) * mm, "end": v(129.5, 58) * mm});
            skPoint(sketch, "E3.24.11.4", {"position": v(132, 60.5) * mm});
            skLineSegment(sketch, "E3.24.12.0", {"start": v(134.5, 68.5) * mm, "end": v(129.5, 68.5) * mm});
            skLineSegment(sketch, "E3.24.12.1", {"start": v(134.5, 68.5) * mm, "end": v(134.5, 63.5) * mm});
            skLineSegment(sketch, "E3.24.12.2", {"start": v(134.5, 63.5) * mm, "end": v(129.5, 63.5) * mm});
            skLineSegment(sketch, "E3.24.12.3", {"start": v(129.5, 68.5) * mm, "end": v(129.5, 63.5) * mm});
            skPoint(sketch, "E3.24.12.4", {"position": v(132, 66) * mm});
            skLineSegment(sketch, "E3.24.13.0", {"start": v(134.5, 74) * mm, "end": v(129.5, 74) * mm});
            skLineSegment(sketch, "E3.24.13.1", {"start": v(134.5, 74) * mm, "end": v(134.5, 69) * mm});
            skLineSegment(sketch, "E3.24.13.2", {"start": v(134.5, 69) * mm, "end": v(129.5, 69) * mm});
            skLineSegment(sketch, "E3.24.13.3", {"start": v(129.5, 74) * mm, "end": v(129.5, 69) * mm});
            skPoint(sketch, "E3.24.13.4", {"position": v(132, 71.5) * mm});
            skLineSegment(sketch, "E3.24.14.0", {"start": v(134.5, 79.5) * mm, "end": v(129.5, 79.5) * mm});
            skLineSegment(sketch, "E3.24.14.1", {"start": v(134.5, 79.5) * mm, "end": v(134.5, 74.5) * mm});
            skLineSegment(sketch, "E3.24.14.2", {"start": v(134.5, 74.5) * mm, "end": v(129.5, 74.5) * mm});
            skLineSegment(sketch, "E3.24.14.3", {"start": v(129.5, 79.5) * mm, "end": v(129.5, 74.5) * mm});
            skPoint(sketch, "E3.24.14.4", {"position": v(132, 77) * mm});
            skLineSegment(sketch, "E3.24.15.0", {"start": v(134.5, 85) * mm, "end": v(129.5, 85) * mm});
            skLineSegment(sketch, "E3.24.15.1", {"start": v(134.5, 85) * mm, "end": v(134.5, 80) * mm});
            skLineSegment(sketch, "E3.24.15.2", {"start": v(134.5, 80) * mm, "end": v(129.5, 80) * mm});
            skLineSegment(sketch, "E3.24.15.3", {"start": v(129.5, 85) * mm, "end": v(129.5, 80) * mm});
            skPoint(sketch, "E3.24.15.4", {"position": v(132, 82.5) * mm});
            skLineSegment(sketch, "E3.24.16.0", {"start": v(134.5, 90.5) * mm, "end": v(129.5, 90.5) * mm});
            skLineSegment(sketch, "E3.24.16.1", {"start": v(134.5, 90.5) * mm, "end": v(134.5, 85.5) * mm});
            skLineSegment(sketch, "E3.24.16.2", {"start": v(134.5, 85.5) * mm, "end": v(129.5, 85.5) * mm});
            skLineSegment(sketch, "E3.24.16.3", {"start": v(129.5, 90.5) * mm, "end": v(129.5, 85.5) * mm});
            skPoint(sketch, "E3.24.16.4", {"position": v(132, 88) * mm});
            skLineSegment(sketch, "E3.24.17.0", {"start": v(134.5, 96) * mm, "end": v(129.5, 96) * mm});
            skLineSegment(sketch, "E3.24.17.1", {"start": v(134.5, 96) * mm, "end": v(134.5, 91) * mm});
            skLineSegment(sketch, "E3.24.17.2", {"start": v(134.5, 91) * mm, "end": v(129.5, 91) * mm});
            skLineSegment(sketch, "E3.24.17.3", {"start": v(129.5, 96) * mm, "end": v(129.5, 91) * mm});
            skPoint(sketch, "E3.24.17.4", {"position": v(132, 93.5) * mm});
            skLineSegment(sketch, "E3.24.18.0", {"start": v(134.5, 101.5) * mm, "end": v(129.5, 101.5) * mm});
            skLineSegment(sketch, "E3.24.18.1", {"start": v(134.5, 101.5) * mm, "end": v(134.5, 96.5) * mm});
            skLineSegment(sketch, "E3.24.18.2", {"start": v(134.5, 96.5) * mm, "end": v(129.5, 96.5) * mm});
            skLineSegment(sketch, "E3.24.18.3", {"start": v(129.5, 101.5) * mm, "end": v(129.5, 96.5) * mm});
            skPoint(sketch, "E3.24.18.4", {"position": v(132, 99) * mm});
            skLineSegment(sketch, "E3.24.19.0", {"start": v(134.5, 107) * mm, "end": v(129.5, 107) * mm});
            skLineSegment(sketch, "E3.24.19.1", {"start": v(134.5, 107) * mm, "end": v(134.5, 102) * mm});
            skLineSegment(sketch, "E3.24.19.2", {"start": v(134.5, 102) * mm, "end": v(129.5, 102) * mm});
            skLineSegment(sketch, "E3.24.19.3", {"start": v(129.5, 107) * mm, "end": v(129.5, 102) * mm});
            skPoint(sketch, "E3.24.19.4", {"position": v(132, 104.5) * mm});
            skLineSegment(sketch, "E3.24.20.0", {"start": v(134.5, 112.5) * mm, "end": v(129.5, 112.5) * mm});
            skLineSegment(sketch, "E3.24.20.1", {"start": v(134.5, 112.5) * mm, "end": v(134.5, 107.5) * mm});
            skLineSegment(sketch, "E3.24.20.2", {"start": v(134.5, 107.5) * mm, "end": v(129.5, 107.5) * mm});
            skLineSegment(sketch, "E3.24.20.3", {"start": v(129.5, 112.5) * mm, "end": v(129.5, 107.5) * mm});
            skPoint(sketch, "E3.24.20.4", {"position": v(132, 110) * mm});
            skLineSegment(sketch, "E3.24.21.0", {"start": v(134.5, 118) * mm, "end": v(129.5, 118) * mm});
            skLineSegment(sketch, "E3.24.21.1", {"start": v(134.5, 118) * mm, "end": v(134.5, 113) * mm});
            skLineSegment(sketch, "E3.24.21.2", {"start": v(134.5, 113) * mm, "end": v(129.5, 113) * mm});
            skLineSegment(sketch, "E3.24.21.3", {"start": v(129.5, 118) * mm, "end": v(129.5, 113) * mm});
            skPoint(sketch, "E3.24.21.4", {"position": v(132, 115.5) * mm});
            skLineSegment(sketch, "E3.24.22.0", {"start": v(134.5, 123.5) * mm, "end": v(129.5, 123.5) * mm});
            skLineSegment(sketch, "E3.24.22.1", {"start": v(134.5, 123.5) * mm, "end": v(134.5, 118.5) * mm});
            skLineSegment(sketch, "E3.24.22.2", {"start": v(134.5, 118.5) * mm, "end": v(129.5, 118.5) * mm});
            skLineSegment(sketch, "E3.24.22.3", {"start": v(129.5, 123.5) * mm, "end": v(129.5, 118.5) * mm});
            skPoint(sketch, "E3.24.22.4", {"position": v(132, 121) * mm});
            skLineSegment(sketch, "E3.24.23.0", {"start": v(134.5, 129) * mm, "end": v(129.5, 129) * mm});
            skLineSegment(sketch, "E3.24.23.1", {"start": v(134.5, 129) * mm, "end": v(134.5, 124) * mm});
            skLineSegment(sketch, "E3.24.23.2", {"start": v(134.5, 124) * mm, "end": v(129.5, 124) * mm});
            skLineSegment(sketch, "E3.24.23.3", {"start": v(129.5, 129) * mm, "end": v(129.5, 124) * mm});
            skPoint(sketch, "E3.24.23.4", {"position": v(132, 126.5) * mm});
            skLineSegment(sketch, "E3.24.24.0", {"start": v(134.5, 134.5) * mm, "end": v(129.5, 134.5) * mm});
            skLineSegment(sketch, "E3.24.24.1", {"start": v(134.5, 134.5) * mm, "end": v(134.5, 129.5) * mm});
            skLineSegment(sketch, "E3.24.24.2", {"start": v(134.5, 129.5) * mm, "end": v(129.5, 129.5) * mm});
            skLineSegment(sketch, "E3.24.24.3", {"start": v(129.5, 134.5) * mm, "end": v(129.5, 129.5) * mm});
            skPoint(sketch, "E3.24.24.4", {"position": v(132, 132) * mm});
            skLineSegment(sketch, "E3.direction1", {"start": v(-2.5, -2.5) * mm, "end": v(3, -2.5) * mm, "construction": true});
            skLineSegment(sketch, "E3.direction2", {"start": v(-2.5, -2.5) * mm, "end": v(-2.5, 3) * mm, "construction": true});
            skSolve(sketch);
        }
        {
            var Q0;
            Q0 = qSketchRegion(id + "F2", true);
            extrude(context, id + "F3", {"entities" : qUnion([Q0]), "operationType" : NewBodyOperationType.ADD, "depth" : 25 * mm});
        }
    });
